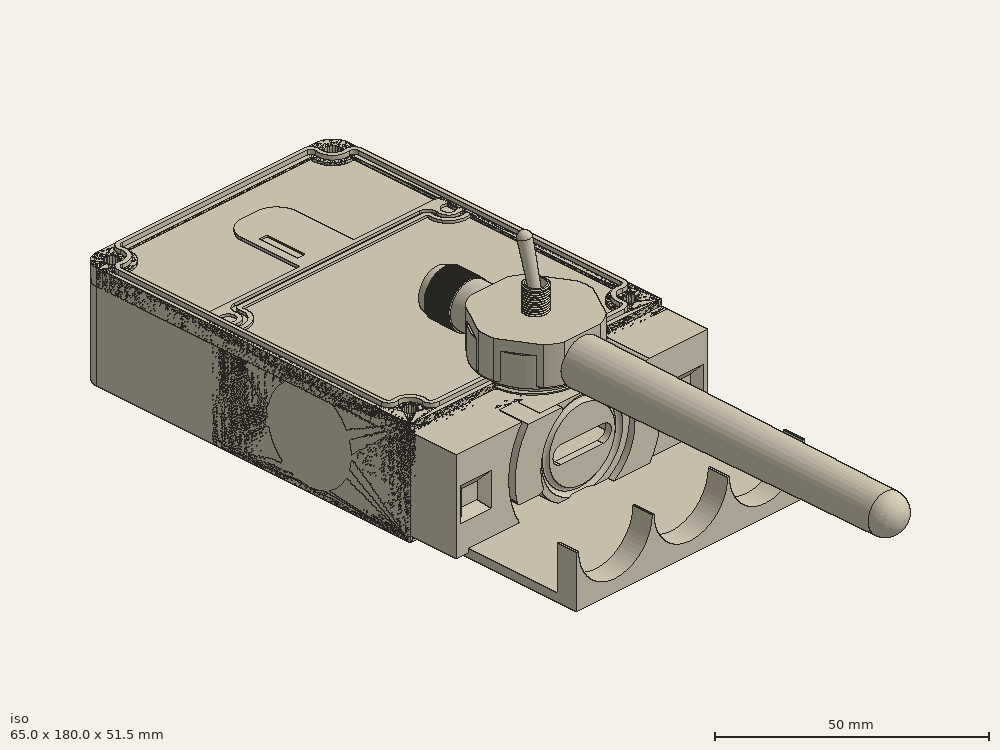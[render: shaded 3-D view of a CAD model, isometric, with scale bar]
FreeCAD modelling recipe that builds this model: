
FCSTD DOCUMENT  (FreeCAD 1.1R40006 (Git))
Label: NomadShell_0.1
License: All rights reserved
LicenseURL: https://en.wikipedia.org/wiki/All_rights_reserved
objects: Sketcher::SketchObject×62, App::FeaturePython×43, App::Point×31, Part::Feature×30, PartDesign::Pocket×26, PartDesign::Pad×24, App::Link×23, App::Part×15, PartDesign::Body×15, PartDesign::SubtractivePipe×6, PartDesign::Fillet×6, PartDesign::SubShapeBinder×5, PartDesign::Revolution×3, Part::FeaturePython×2, PartDesign::Boolean×2, PartDesign::Hole×2, App::DocumentObjectGroup×2, PartDesign::AdditivePipe×2, App::VarSet×1, PartDesign::Chamfer×1, +8 more types
note: 402 computed .brp shape members not serialized (recipe doc carries the construction recipe); baked Part::Feature solids carry a one-line shape summary decoded from their .brp

FEATURE [Part::Feature] Part__Feature064  label="18650 v1"
  Placement = pos=(-6,-63,0) rot=(0,0,1;3.14159rad)
  shape: bbox 19.48 x 65 x 19.48 mm, 40 faces (baked)
FEATURE [App::Point] Origin105
  Role = Origin
FEATURE [App::VarSet] VarSet
  Base_base_lenght = 55
  Base_battery_lenght = 85
  Base_case_thickness = 3
  Base_connecot_lug_multipl = 2
  Base_connector_bounting_box_height = 22
  Base_connector_clip = 8
  Base_connector_clip_height = 1.6
  Base_connector_external_lug = 19
  Base_connector_height_lug = 12
  Base_connector_internal_lug = 12
  Base_connector_lug_offset = 0.1
  Base_connector_lug_remaining_key = 6
  Base_connector_oring_cross_section = 2
  Base_connector_oring_offset = 0.2
  Base_connector_oring_outside_diameter = 21
  Base_gasket_height = 2
  Base_gasket_width = 1
  Base_gps_antenna_height = 5
  Base_gps_antenna_lenght = 15
  Base_gps_antenna_width = 15
  Base_lid_thickness = 5
  Base_m3_insert = 3.2
  Base_pogopin_cutout_height = 1.5
  Base_pogopin_outside = 21
  Base_pogoping_lenght = 15.1
  Base_pogopins_r = 2.1
  Base_usb_cover_main_diameter = 18
  base_width = 65
  case_height = 25
FEATURE [App::Point] Origin111
  Role = Origin
FEATURE [App::Point] Origin113
  Role = Origin
FEATURE [App::Link] base  label="base001"
  LinkedObject = -> Part
FEATURE [App::FeaturePython] GroundedJoint  # Assembly grounded joint (typed FeaturePython)
  ObjectToGround = -> base
FEATURE [Part::Feature] PCB_solid  label="RAK19003_carrier"
  shape: bbox 35.78 x 30 x 9.401 mm, 8397 faces (baked)
FEATURE [App::Link] RAK19003__Solid_  label="RAK19003 (Solid)001"
  LinkPlacement = pos=(-8.5,9,-15.9902) rot=(0,0,1;0rad)
  LinkedObject = -> PCB_solid
  Placement = pos=(-8.5,9,-15.9902) rot=(0,0,1;0rad)
FEATURE [App::Point] Origin115
  Role = Origin
FEATURE [App::Point] Origin117
  Role = Origin
FEATURE [Sketcher::SketchObject] Sketch006  label="battery_body001"
  ArcFitTolerance = 1e-06
  AttachmentSupport = -> [XY_Plane058]
  ExternalTypes = [0]
  FullyConstrained = true
  MakeInternals = false
  MapMode = 5
  expr: Constraints[13] = VarSet.base_width
  expr: Constraints[14] = VarSet.Base_battery_lenght
  expr: Constraints[30] = VarSet.Base_m3_insert
  expr: Constraints[44] = VarSet.Base_case_thickness
  expr: Constraints[47] = VarSet.Base_case_thickness + VarSet.Base_m3_insert / 2
  expr: Constraints[48] = VarSet.Base_case_thickness + VarSet.Base_m3_insert / 2
  expr: Constraints[67] = VarSet.Base_case_thickness / 2
  expr: Constraints[84] = VarSet.Base_case_thickness
  expr: Constraints[85] = VarSet.Base_case_thickness
  expr: Constraints[92] = VarSet.Base_case_thickness / 2
  sketch-geometry (40):
    g0: LineSegment StartX=-32.5 StartY=0 StartZ=0 EndX=32.5 EndY=0 EndZ=0
    g1: LineSegment StartX=32.5 StartY=0 StartZ=0 EndX=32.5 EndY=81 EndZ=0
    g2: LineSegment StartX=28.5 StartY=85 StartZ=0 EndX=-28.5 EndY=85 EndZ=0
    g3: LineSegment StartX=-32.5 StartY=81 StartZ=0 EndX=-32.5 EndY=0 EndZ=0
    g4: GeomPoint [constr] X=-32.5 Y=85 Z=0
    g5: ArcOfCircle CenterX=28.5 CenterY=81 CenterZ=0 NormalX=0 NormalY=0 NormalZ=1 AngleXU=0 Radius=4 StartAngle=1e-15 EndAngle=1.5708
    g6: GeomPoint [constr] X=32.5 Y=85 Z=0
    g7: Circle CenterX=-28.5 CenterY=4 CenterZ=0 NormalX=0 NormalY=0 NormalZ=1 AngleXU=0 Radius=1.6
    g8: Circle CenterX=28.5 CenterY=4 CenterZ=0 NormalX=0 NormalY=0 NormalZ=1 AngleXU=0 Radius=1.6
    g9: Circle CenterX=28.5 CenterY=81 CenterZ=0 NormalX=0 NormalY=0 NormalZ=1 AngleXU=0 Radius=1.6
    g10: Circle CenterX=-28.5 CenterY=81 CenterZ=0 NormalX=0 NormalY=0 NormalZ=1 AngleXU=0 Radius=1.6
    g11: LineSegment [constr] StartX=-28.5 StartY=81 StartZ=0 EndX=-28.5 EndY=4 EndZ=0
    g12: LineSegment [constr] StartX=-28.5 StartY=4 StartZ=0 EndX=28.5 EndY=4 EndZ=0
    g13: LineSegment [constr] StartX=28.5 StartY=4 StartZ=0 EndX=28.5 EndY=81 EndZ=0
    g14: LineSegment [constr] StartX=28.5 StartY=81 StartZ=0 EndX=-28.5 EndY=81 EndZ=0
    g15: LineSegment StartX=-24.01 StartY=82 StartZ=0 EndX=23.9076 EndY=82 EndZ=0
    g16: LineSegment StartX=29.5 StartY=76.4076 StartZ=0 EndX=29.5 EndY=8.48999 EndZ=0
    g17: LineSegment StartX=24.01 StartY=3 StartZ=0 EndX=-24.01 EndY=3 EndZ=0
    g18: LineSegment StartX=-29.5 StartY=8.48999 StartZ=0 EndX=-29.5 EndY=76.51 EndZ=0
    g19: ArcOfCircle CenterX=-28.5 CenterY=4 CenterZ=0 NormalX=0 NormalY=0 NormalZ=1 AngleXU=0 Radius=4.6 StartAngle=6.06404 EndAngle=8.07312
    g20: ArcOfCircle CenterX=-28.5 CenterY=81 CenterZ=0 NormalX=0 NormalY=0 NormalZ=1 AngleXU=0 Radius=4.6 StartAngle=4.49325 EndAngle=6.50233
    g21: ArcOfCircle CenterX=28.5 CenterY=81 CenterZ=0 NormalX=0 NormalY=0 NormalZ=1 AngleXU=0 Radius=4.7 StartAngle=2.92719 EndAngle=4.92679
    g22: ArcOfCircle CenterX=28.5 CenterY=4 CenterZ=0 NormalX=0 NormalY=0 NormalZ=1 AngleXU=0 Radius=4.6 StartAngle=1.35166 EndAngle=3.36073
    g23: ArcOfCircle CenterX=28.5 CenterY=4 CenterZ=0 NormalX=0 NormalY=0 NormalZ=1 AngleXU=0 Radius=3.1 StartAngle=1.35166 EndAngle=3.36073
    g24: ArcOfCircle CenterX=24.01 CenterY=3 CenterZ=0 NormalX=0 NormalY=0 NormalZ=1 AngleXU=-3.14159 Radius=1.5 StartAngle=1.5708 EndAngle=3.36073
    g25: LineSegment StartX=24.01 StartY=1.5 StartZ=0 EndX=-24.01 EndY=1.5 EndZ=0
    g26: ArcOfCircle CenterX=-24.01 CenterY=3 CenterZ=0 NormalX=0 NormalY=0 NormalZ=1 AngleXU=1.55119 Radius=1.5 StartAngle=1.37126 EndAngle=3.1612
    g27: ArcOfCircle CenterX=-28.5 CenterY=4 CenterZ=0 NormalX=0 NormalY=0 NormalZ=1 AngleXU=0 Radius=3.1 StartAngle=6.06404 EndAngle=8.07312
    g28: ArcOfCircle CenterX=-29.5 CenterY=8.48999 CenterZ=0 NormalX=0 NormalY=0 NormalZ=1 AngleXU=1.5708 Radius=1.5 StartAngle=1.5708 EndAngle=3.36073
    g29: LineSegment StartX=-31 StartY=8.48999 StartZ=0 EndX=-31 EndY=76.51 EndZ=0
    g30: ArcOfCircle CenterX=-29.5 CenterY=76.51 CenterZ=0 NormalX=0 NormalY=0 NormalZ=1 AngleXU=-0.0196091 Radius=1.5 StartAngle=1.37126 EndAngle=3.1612
    g31: ArcOfCircle CenterX=-28.5 CenterY=81 CenterZ=0 NormalX=0 NormalY=0 NormalZ=1 AngleXU=0 Radius=3.1 StartAngle=4.49325 EndAngle=6.50233
    g32: ArcOfCircle CenterX=-24.01 CenterY=82 CenterZ=0 NormalX=0 NormalY=0 NormalZ=1 AngleXU=0 Radius=1.5 StartAngle=1.5708 EndAngle=3.36073
    g33: LineSegment StartX=-24.01 StartY=83.5 StartZ=0 EndX=23.9076 EndY=83.5 EndZ=0
    g34: ArcOfCircle CenterX=23.9076 CenterY=82 CenterZ=0 NormalX=0 NormalY=0 NormalZ=1 AngleXU=-1.5708 Radius=1.5 StartAngle=1.35639 EndAngle=3.14159
    g35: ArcOfCircle CenterX=28.5 CenterY=81 CenterZ=0 NormalX=0 NormalY=0 NormalZ=1 AngleXU=0 Radius=3.2 StartAngle=2.92719 EndAngle=4.92679
    g36: ArcOfCircle CenterX=29.5 CenterY=76.4076 CenterZ=0 NormalX=0 NormalY=0 NormalZ=1 AngleXU=-1.5708 Radius=1.5 StartAngle=1.5708 EndAngle=3.356
    g37: LineSegment StartX=31 StartY=76.4076 StartZ=0 EndX=31 EndY=8.48999 EndZ=0
    g38: ArcOfCircle CenterX=29.5 CenterY=8.48999 CenterZ=0 NormalX=0 NormalY=0 NormalZ=1 AngleXU=3.12198 Radius=1.5 StartAngle=1.37126 EndAngle=3.1612
    g39: ArcOfCircle CenterX=-28.5 CenterY=81 CenterZ=0 NormalX=0 NormalY=0 NormalZ=1 AngleXU=0 Radius=4 StartAngle=1.5708 EndAngle=3.14159
  constraints (94):
    c: Coincident(g0,g1)
    c: Coincident(g3,g0)
    c: Horizontal(g2)
    c: Vertical(g1)
    c: Vertical(g3)
    c: PointOnObject(g0,g-1)
    c: Symmetric(g0,g0,g-2)
    c: PointOnObject(g4,g3)
    c: PointOnObject(g4,g2)
    c: PointOnObject(g6,g1)
    c: PointOnObject(g6,g2)
    c: Tangent(g1,g5) = -1.5708
    c: Tangent(g2,g5) = -1.5708
    c: DistanceX(g4,g6) = 65
    c: DistanceY(g0,g4) = 85
    c: Coincident(g11,g12)
    c: Coincident(g12,g13)
    c: Coincident(g13,g14)
    c: Coincident(g14,g11)
    c: Vertical(g11)
    c: Vertical(g13)
    c: Horizontal(g12)
    c: Coincident(g11,g10)
    c: Coincident(g12,g8)
    c: Coincident(g7,g11)
    c: Coincident(g13,g9)
    c: Symmetric(g10,g9,g-2)
    c: Equal(g10,g9)
    c: Equal(g9,g8)
    c: Equal(g8,g7)
    c: Diameter(g10) = 3.2
    c: Distance(g7,g0) = 2.4
    c: Horizontal(g15)
    c: Vertical(g16)
    c: Horizontal(g17)
    c: Vertical(g18)
    c: Coincident(g19,g18)
    c: Coincident(g19,g17)
    c: Coincident(g20,g18)
    c: Coincident(g20,g15)
    c: Coincident(g21,g15)
    c: Coincident(g21,g16)
    c: Coincident(g22,g16)
    c: Coincident(g22,g17)
    c: Distance(g17,g0) = 3
    c: Coincident(g22,g8)
    c: Coincident(g19,g7)
    c: Radius(g19) = 4.6
    c: Radius(g20) = 4.6
    c: Coincident(g10,g20)
    c: Coincident(g21,g5)
    c: Tangent(g23,g24) = 1.5708
    c: Tangent(g23,g38) = 1.5708
    c: Tangent(g24,g25) = 1.5708
    c: Tangent(g25,g26) = 1.5708
    c: Tangent(g26,g27) = 1.5708
    c: Tangent(g27,g28) = 1.5708
    c: Tangent(g28,g29) = 1.5708
    c: Tangent(g29,g30) = 1.5708
    c: Tangent(g30,g31) = 1.5708
    c: Tangent(g31,g32) = 1.5708
    c: Tangent(g32,g33) = 1.5708
    c: Tangent(g33,g34) = 1.5708
    c: Tangent(g34,g35) = 1.5708
    c: Tangent(g35,g36) = 1.5708
    c: Tangent(g36,g37) = 1.5708
    c: Tangent(g37,g38) = 1.5708
    c: Distance(g17,g25) = 1.5
    c: Coincident(g32,g15)
    c: Coincident(g30,g18)
    c: Coincident(g36,g16)
    c: Coincident(g24,g17)
    c: Coincident(g26,g17)
    c: Coincident(g28,g18)
    c: Coincident(g27,g7)
    c: Coincident(g23,g8)
    c: Coincident(g9,g35)
    c: Coincident(g34,g15)
    c: Coincident(g38,g16)
    c: Coincident(g39,g10)
    c: Coincident(g39,g2)
    c: Coincident(g39,g3)
    c: Coincident(g31,g10)
    c: Coincident(g5,g9)
    c: Distance(g1,g16) = 3
    c: Distance(g18,g3) = 3
    c: Parallel(g25,g-1)
    c: Parallel(g29,g-2)
    c: Parallel(g33,g-1)
    c: Equal(g27,g23)
    c: Distance(g10,g2) = 2.4
    c: Radius(g39) = 4
    c: Distance(g33,g2) = 1.5
    c: Radius(g35) = 3.2
FEATURE [PartDesign::Pad] Pad004
  Direction = (0,0,1)
  Length = 25
  Length2 = 10
  Profile = -> Sketch006 [Edge1,Edge6,Edge5,Edge4,Edge3,Edge2]
  ReferenceAxis = -> Sketch006 [N_Axis]
  Refine = true
  Reversed = true
  Suppressed = false
  Type = 0
  expr: Length = VarSet.case_height
FEATURE [PartDesign::Pocket] Pocket005  label="pocket"
  BaseFeature = -> Pad004
  Direction = (0,0,-1)
  Length = 22
  Length2 = 5
  Profile = -> Sketch006 [Edge15,Edge16,Edge17,Edge18,Edge11,Edge12,Edge13,Edge14]
  ReferenceAxis = -> Sketch006 [N_Axis]
  Refine = true
  Suppressed = false
  Type = 0
  expr: Length = VarSet.case_height - VarSet.Base_case_thickness
FEATURE [PartDesign::Pocket] Pocket006  label="screw001"
  BaseFeature = -> Pocket005
  Direction = (0,0,-1)
  Length = 5
  Length2 = 5
  Midplane = true
  Profile = -> Sketch006 [Edge10,Edge9,Edge8,Edge7]
  ReferenceAxis = -> Sketch006 [N_Axis]
  Refine = true
  Suppressed = false
  Type = 1
FEATURE [App::Link] battery  label="battery001"
  LinkPlacement = pos=(0.216708,-33.5,0.15511) rot=(0,0,1;3.14159rad)
  LinkedObject = -> Part002
  Placement = pos=(0.216708,-33.5,0.15511) rot=(0,0,1;3.14159rad)
FEATURE [Sketcher::SketchObject] Sketch007  label="18650_battery_holder"
  ArcFitTolerance = 1e-06
  AttachmentOffset = pos=(0,0,-21) rot=(0,0,1;0rad)
  AttachmentSupport = -> [XZ_Plane058]
  ExternalGeometry = -> [Pocket006]
  ExternalTypes = [0,0,0]
  FullyConstrained = true
  MakeInternals = false
  MapMode = 5
  Placement = pos=(0,21,-4.7e-15) rot=(1,0,0;1.5708rad)
  expr: .AttachmentOffset.Base.z = -7 * VarSet.Base_case_thickness
  sketch-geometry (12):
    g0: ArcOfCircle CenterX=-19.4 CenterY=-12 CenterZ=0 NormalX=0 NormalY=0 NormalZ=1 AngleXU=0 Radius=9.5 StartAngle=3.14159 EndAngle=6.28319
    g1: LineSegment StartX=-28.9 StartY=-12 StartZ=0 EndX=-29.4 EndY=-12 EndZ=0
    g2: LineSegment StartX=-29.4 StartY=-12 StartZ=0 EndX=-29.4 EndY=-22 EndZ=0
    g3: LineSegment StartX=-29.4 StartY=-22 StartZ=0 EndX=29.5 EndY=-22 EndZ=0
    g4: LineSegment StartX=-9.4 StartY=-12 StartZ=0 EndX=-9.9 EndY=-12 EndZ=0
    g5: LineSegment [constr] StartX=-29.4 StartY=-12 StartZ=0 EndX=29.5 EndY=-12 EndZ=0
    g6: LineSegment [constr] StartX=29.5 StartY=0 StartZ=0 EndX=29.5 EndY=-12 EndZ=0
    g7: ArcOfCircle CenterX=0.1 CenterY=-12 CenterZ=0 NormalX=0 NormalY=0 NormalZ=1 AngleXU=0 Radius=9.5 StartAngle=3.14159 EndAngle=6.28319
    g8: LineSegment StartX=9.6 StartY=-12 StartZ=0 EndX=10.1 EndY=-12 EndZ=0
    g9: ArcOfCircle CenterX=19.6 CenterY=-12 CenterZ=0 NormalX=0 NormalY=0 NormalZ=1 AngleXU=0 Radius=9.5 StartAngle=3.14159 EndAngle=6.28319
    g10: LineSegment StartX=29.1 StartY=-12 StartZ=0 EndX=29.5 EndY=-12 EndZ=0
    g11: LineSegment StartX=29.5 StartY=-22 StartZ=0 EndX=29.5 EndY=-12 EndZ=0
  constraints (37):
    c: Coincident(g1,g2)
    c: Vertical(g2)
    c: Coincident(g2,g3)
    c: Horizontal(g3)
    c: Coincident(g0,g1)
    c: Radius(g0) = 9.5
    c: DistanceY(g2,g1) = 10
    c: PointOnObject(g3,g-3)
    c: DistanceX(g1,g0) = 0.5
    c: DistanceX(g-5,g1) = 0.1
    c: Coincident(g4,g0)
    c: Horizontal(g4)
    c: Coincident(g5,g1)
    c: Horizontal(g5)
    c: Coincident(g6,g-4)
    c: Coincident(g6,g5)
    c: Vertical(g6)
    c: PointOnObject(g7,g5)
    c: Coincident(g7,g4)
    c: PointOnObject(g7,g5)
    c: Coincident(g7,g8)
    c: PointOnObject(g8,g5)
    c: PointOnObject(g0,g5)
    c: PointOnObject(g0,g5)
    c: PointOnObject(g0,g5)
    c: PointOnObject(g9,g5)
    c: Coincident(g9,g8)
    c: PointOnObject(g9,g5)
    c: Coincident(g10,g9)
    c: Coincident(g11,g3)
    c: Coincident(g11,g10)
    c: Perpendicular(g11,g3)
    c: Equal(g1,g4)
    c: Equal(g4,g8)
    c: Equal(g0,g7)
    c: Equal(g7,g9)
    c: Coincident(g10,g5)
FEATURE [PartDesign::Pad] Pad005  label="18650_battery_holder001"
  BaseFeature = -> Pocket006
  Direction = (0,-1,2e-16)
  Length = 5
  Length2 = 10
  Midplane = true
  Profile = -> Sketch007
  ReferenceAxis = -> Sketch007 [N_Axis]
  Refine = true
  Suppressed = false
  Type = 0
FEATURE [App::Link] _8650_v1  label="18650 v002"
  LinkPlacement = pos=(0.116708,-107.966,-11.8449) rot=(0,-1,0;1.5708rad)
  LinkedObject = -> Part__Feature064
  Placement = pos=(0.116708,-107.966,-11.8449) rot=(0,-1,0;1.5708rad)
FEATURE [Part::Feature] Part__Feature066  label="ant"
  Placement = pos=(3.7e-15,4.99733,5.00169) rot=(1,0,0;1.5708rad)
  shape: bbox 11.02 x 100 x 11.02 mm, 30 faces, 3 solids (baked)
FEATURE [Part::Feature] Part__Feature067  label="conn_body"
  Placement = pos=(-0.0138346,-0.00267039,0.00168873) rot=(0,0,1;0rad)
  shape: bbox 11.61 x 29.27 x 11.28 mm, 560 faces (baked)
FEATURE [Part::Feature] Part__Feature068  label="SMA_threads"
  Placement = pos=(-0.0138346,-0.00267039,0.00168873) rot=(0,0,1;0rad)
  shape: bbox 8 x 3 x 8 mm, 4 faces (baked)
FEATURE [Part::Feature] Part__Feature069  label="socket"
  Placement = pos=(-0.0138346,-0.28267,0.00168873) rot=(0,0,1;0rad)
  shape: bbox 1.27 x 5.64 x 1.27 mm, 5 faces (baked)
FEATURE [App::Part] antenna_WiFi_RP_SMA_conn_v2  label="antenna_WiFi_RP-SMA_conn v2"
  Group = -> [Part__Feature066,Part__Feature067,Part__Feature068,Part__Feature069]
  Origin = -> Origin118
FEATURE [App::Point] Origin119
  Role = Origin
FEATURE [Part::Feature] Part__Feature070  label="sma"
  Placement = pos=(0,0,-13) rot=(0,0,1;0rad)
  shape: bbox 10.21 x 10.21 x 16.97 mm, 172 faces (baked)
FEATURE [Part::Feature] Part__Feature071  label="70205K69_Cover for 0.5 Deep x 0.12 Diameter Toggle Switch"
  shape: bbox 8.382 x 1.91 x 8.382 mm, 13 faces (baked)
FEATURE [Part::Feature] Part__Feature072  label="70205K69_Cover for 0.5 Deep x 0.12 Diameter Toggle Switch001"
  shape: bbox 10.37 x 17.02 x 11.04 mm, 82 faces (baked)
FEATURE [App::Part] _0205K69_Cover_for_0_5_Deep_x_0_12_Diameter_Toggle_Switch  label="switch_cover"
  Group = -> [Part__Feature071,Part__Feature072]
  Origin = -> Origin120
  Placement = pos=(0,0,34) rot=(1,0,0;3.14159rad)
FEATURE [App::Point] Origin121
  Role = Origin
FEATURE [Part::Feature] Part__Feature073  label="Plastic_corpuse"
  shape: bbox 7.85 x 12.96 x 9.7 mm, 55 faces (baked)
FEATURE [Part::Feature] Part__Feature074  label="Contacts"
  shape: bbox 3.88 x 0.8 x 4.2 mm, 14 faces (baked)
FEATURE [Part::Feature] Part__Feature075  label="Contacts001"
  Placement = pos=(0,-4.43,0) rot=(0,0,1;0rad)
  shape: bbox 3.88 x 0.8 x 4.2 mm, 14 faces (baked)
FEATURE [Part::Feature] Part__Feature076  label="Metal_scoba"
  shape: bbox 7.9 x 13 x 6 mm, 255 faces (baked)
FEATURE [Part::Feature] Part__Feature077  label="Rezba"
  Placement = pos=(0.0336891,-0.0345067,0.0256431) rot=(0,0,1;0rad)
  shape: bbox 6.314 x 6.357 x 7.676 mm, 70 faces (baked)
FEATURE [Part::Feature] Part__Feature078  label="Tumbler"
  Placement = pos=(0,-3.72699,0.490668) rot=(-1,0,0;0.261799rad)
  shape: bbox 3 x 5.772 x 13.55 mm, 3 faces (baked)
FEATURE [App::Part] TSM102A1_v5  label="on_off_switch"
  Group = -> [Part__Feature073,Part__Feature074,Part__Feature075,Part__Feature076,Part__Feature077,Part__Feature078]
  Origin = -> Origin122
  Placement = pos=(0,0,43) rot=(1,0,0;1.5708rad)
FEATURE [App::Point] Origin123
  Role = Origin
FEATURE [App::Point] Origin125
  Role = Origin
FEATURE [App::Point] Origin127
  Role = Origin
FEATURE [Sketcher::SketchObject] Sketch008  label="main_usb_cover"
  ArcFitTolerance = 1e-06
  AttachmentSupport = -> [XZ_Plane063]
  ExternalTypes = [0]
  FullyConstrained = true
  MakeInternals = false
  MapMode = 5
  Placement = pos=(0,0,0) rot=(1,0,0;1.5708rad)
  expr: Constraints[12] = VarSet.Base_case_thickness / 2
  expr: Constraints[14] = VarSet.Base_usb_cover_main_diameter * 1.2 / 2
  expr: Constraints[15] = VarSet.Base_usb_cover_main_diameter / 2
  sketch-geometry (6):
    g0: LineSegment StartX=-9 StartY=0 StartZ=0 EndX=-10.8 EndY=0 EndZ=0
    g1: LineSegment StartX=-10.8 StartY=0 StartZ=0 EndX=-10.8 EndY=1.5 EndZ=0
    g2: LineSegment StartX=-10.8 StartY=1.5 StartZ=0 EndX=-10.4 EndY=1.5 EndZ=0
    g3: LineSegment StartX=-10.4 StartY=1.5 StartZ=0 EndX=-10.4 EndY=7.5 EndZ=0
    g4: LineSegment StartX=-10.4 StartY=7.5 StartZ=0 EndX=-9 EndY=7.5 EndZ=0
    g5: LineSegment StartX=-9 StartY=7.5 StartZ=0 EndX=-9 EndY=0 EndZ=0
  constraints (18):
    c: PointOnObject(g0,g-1)
    c: PointOnObject(g0,g-1)
    c: Coincident(g0,g1)
    c: Coincident(g1,g2)
    c: Horizontal(g2)
    c: Coincident(g2,g3)
    c: Coincident(g3,g4)
    c: Coincident(g4,g5)
    c: Coincident(g5,g0)
    c: Parallel(g5,g-2)
    c: Parallel(g4,g-1)
    c: Parallel(g1,g-2)
    c: DistanceY(g0,g1) = 1.5
    c: Parallel(g3,g5)
    c: DistanceX(g0,g-1) = 10.8
    c: DistanceX(g0,g-1) = 9
    c: DistanceY(g2,g3) = 6
    c: Distance(g4,g4) = 1.4
FEATURE [PartDesign::Revolution] Revolution
  Angle = 360
  Angle2 = 60
  Axis = (0,2e-16,1)
  Base = (0,0,0)
  Placement = pos=(0,0,0) rot=(1,0,0;1.5708rad)
  Profile = -> Sketch008
  ReferenceAxis = -> Sketch008 [V_Axis]
  Refine = true
  Suppressed = false
  Type = 0
FEATURE [App::Link] usb_cover_base  label="usb_cover_base001"
  LinkPlacement = pos=(-31,26,-13) rot=(0.57735,-0.57735,-0.57735;2.0944rad)
  LinkedObject = -> Part003
  Placement = pos=(-31,26,-13) rot=(0.57735,-0.57735,-0.57735;2.0944rad)
FEATURE [App::Link] on_off_switch  label="on_off_switch002"
  LinkPlacement = pos=(1.00889,42.9,-9.4) rot=(-0.57735,0.57735,0.57735;2.0944rad)
  LinkedObject = -> TSM102A1_v5
  Placement = pos=(1.00889,42.9,-9.4) rot=(-0.57735,0.57735,0.57735;2.0944rad)
FEATURE [App::Link] switch_cover  label="switch_cover001"
  LinkPlacement = pos=(1.00889,63.509,-9.4) rot=(0,1,0;1.5708rad)
  LinkedObject = -> _0205K69_Cover_for_0_5_Deep_x_0_12_Diameter_Toggle_Switch
  Placement = pos=(1.00889,63.509,-9.4) rot=(0,1,0;1.5708rad)
FEATURE [App::Link] antenna_WiFi_RP_SMA_conn_v003  label="antenna_WiFi_RP-SMA_conn v003"
  LinkPlacement = pos=(17.0138,86.4273,-10.9983) rot=(1,0,0;3.14159rad)
  LinkedObject = -> antenna_WiFi_RP_SMA_conn_v2
  Placement = pos=(17.0138,86.4273,-10.9983) rot=(1,0,0;3.14159rad)
FEATURE [Part::Feature] PCB_solid001  label="RAK4631 (Solid)"
  shape: bbox 20 x 30 x 4.403 mm, 2955 faces (baked)
FEATURE [App::Link] RAK4631__Solid_  label="RAK4631 (Solid)001"
  LinkPlacement = pos=(29.458,29.4471,-14.4384) rot=(-0.447342,0,0.894685;0rad)
  LinkedObject = -> PCB_solid001
  Placement = pos=(29.458,29.4471,-14.4384) rot=(-0.447342,0,0.894685;0rad)
FEATURE [Part::FeaturePython] ScrewDie  label="21x7-ScrewDie"  # WARN: FeaturePython — macro-defined, semantics opaque (R4)
  Diameter = 29
  DiameterCustom = 21
  Invert = false
  LeftHanded = false
  Length = 7
  MatchOuter = false
  OffsetAngle = 0
  PitchCustom = 2
  Placement = pos=(0,0,8.5) rot=(0,0,1;0rad)
  Thread = true
  Type = 0
FEATURE [App::Point] Origin128
  Role = Origin
FEATURE [App::Point] Origin130
  Role = Origin
FEATURE [Sketcher::SketchObject] Sketch009  label="main_screw"
  ArcFitTolerance = 1e-06
  AttachmentSupport = -> [XZ_Plane064]
  ExternalTypes = [0]
  FullyConstrained = true
  MakeInternals = false
  MapMode = 5
  Placement = pos=(0,0,0) rot=(1,0,0;1.5708rad)
  expr: Constraints[15] = VarSet.Base_usb_cover_main_diameter / 2
  sketch-geometry (6):
    g0: LineSegment StartX=0 StartY=9 StartZ=0 EndX=0 EndY=11 EndZ=0
    g1: LineSegment StartX=0 StartY=11 StartZ=0 EndX=-13 EndY=11 EndZ=0
    g2: LineSegment StartX=-13 StartY=11 StartZ=0 EndX=-13 EndY=2 EndZ=0
    g3: LineSegment StartX=-13 StartY=2 StartZ=0 EndX=-9 EndY=2 EndZ=0
    g4: LineSegment StartX=-9 StartY=2 StartZ=0 EndX=-9 EndY=9 EndZ=0
    g5: LineSegment StartX=-9 StartY=9 StartZ=0 EndX=0 EndY=9 EndZ=0
  constraints (18):
    c: PointOnObject(g0,g-2)
    c: PointOnObject(g0,g-2)
    c: Coincident(g0,g1)
    c: Horizontal(g1)
    c: Coincident(g1,g2)
    c: Vertical(g2)
    c: Coincident(g2,g3)
    c: Horizontal(g3)
    c: Coincident(g3,g4)
    c: Vertical(g4)
    c: Coincident(g4,g5)
    c: Coincident(g5,g0)
    c: Horizontal(g5)
    c: Distance(g0,g0) = 2
    c: DistanceX(g1,g4) = 4
    c: DistanceX(g4,g0) = 9
    c: DistanceY(g2,g2) = 9
    c: DistanceY(g-1,g0) = 9
FEATURE [PartDesign::Revolution] Revolution001
  Angle = 360
  Angle2 = 60
  Axis = (0,2e-16,1)
  Base = (0,0,0)
  Placement = pos=(0,0,0) rot=(1,0,0;1.5708rad)
  Profile = -> Sketch009
  ReferenceAxis = -> Sketch009 [V_Axis]
  Refine = true
  Suppressed = false
  Type = 0
FEATURE [Sketcher::SketchObject] Sketch010  label="cutout"
  ArcFitTolerance = 1e-06
  AttachmentSupport = -> [XY_Plane064]
  ExternalGeometry = -> [Revolution001]
  ExternalTypes = [0]
  FullyConstrained = true
  MakeInternals = false
  MapMode = 5
  sketch-geometry (7):
    g0: LineSegment StartX=14 StartY=0 StartZ=0 EndX=7 EndY=12.1244 EndZ=0
    g1: LineSegment StartX=7 StartY=12.1244 StartZ=0 EndX=-7 EndY=12.1244 EndZ=0
    g2: LineSegment StartX=-7 StartY=12.1244 StartZ=0 EndX=-14 EndY=-2.1849e-12 EndZ=0
    g3: LineSegment StartX=-14 StartY=-2.1849e-12 StartZ=0 EndX=-7 EndY=-12.1244 EndZ=0
    g4: LineSegment StartX=-7 StartY=-12.1244 StartZ=0 EndX=7 EndY=-12.1244 EndZ=0
    g5: LineSegment StartX=7 StartY=-12.1244 StartZ=0 EndX=14 EndY=0 EndZ=0
    g6: Circle [constr] CenterX=0 CenterY=0 CenterZ=0 NormalX=0 NormalY=0 NormalZ=1 AngleXU=0 Radius=14
  constraints (16):
    c: Coincident(g0,g1)
    c: Coincident(g1,g2)
    c: Coincident(g2,g3)
    c: Coincident(g3,g4)
    c: Coincident(g4,g5)
    c: Coincident(g5,g0)
    c: Equal(g0, g1-g5) x5
    c: PointOnObject(g0,g6)
    c: PointOnObject(g1,g6)
    c: PointOnObject(g2,g6)
    c: PointOnObject(g3,g6)
    c: PointOnObject(g4,g6)
    c: PointOnObject(g5,g6)
    c: Coincident(g6,g-1)
    c: PointOnObject(g5,g-1)
    c: Diameter(g6) = 28
FEATURE [PartDesign::Pocket] Pocket011
  BaseFeature = -> Revolution001
  Direction = (0,0,-1)
  Length = 5
  Length2 = 5
  Placement = pos=(0,0,0) rot=(1,0,0;1.5708rad)
  Profile = -> Sketch010
  ReferenceAxis = -> Sketch010 [N_Axis]
  Refine = true
  Reversed = true
  Suppressed = false
  Type = 1
FEATURE [Part::FeaturePython] ScrewTap  label="21.4x10-ScrewTap"  # WARN: FeaturePython — macro-defined, semantics opaque (R4)
  Diameter = 29
  DiameterCustom = 21.4
  Invert = false
  LeftHanded = false
  Length = 10
  MatchOuter = false
  OffsetAngle = 0
  PitchCustom = 2
  Placement = pos=(0,0,9) rot=(0,0,1;0rad)
  Thread = true
  Type = 2
FEATURE [PartDesign::Boolean] Boolean001
  BaseFeature = -> Pocket011
  Group = -> [ScrewTap]
  Refine = true
  Suppressed = false
  Type = 1
  UsePlacement = true
FEATURE [PartDesign::Body] Body004  label="usb_screw002"
  AllowCompound = false
  Group = -> [Sketch009,Revolution001,Sketch010,Pocket011,Boolean001]
  Origin = -> Origin129
  Tip = -> Boolean001
FEATURE [App::Part] Part004  label="usb_screw"
  Group = -> [Body004]
  Origin = -> Origin
  Placement = pos=(0,0,21) rot=(0,0,1;0rad)
FEATURE [PartDesign::Boolean] Boolean
  BaseFeature = -> Revolution
  Group = -> [ScrewDie]
  Refine = true
  Suppressed = false
  Type = 1
  UsePlacement = true
FEATURE [PartDesign::Body] Body003  label="usb_cover_base002"
  AllowCompound = false
  Group = -> [Sketch008,Revolution,Boolean]
  Origin = -> Origin126
  Tip = -> Boolean
FEATURE [App::Part] Part003  label="usb_cover_base"
  Group = -> [Body003]
  Origin = -> Origin124
FEATURE [App::Link] usb_screw  label="usb_screw001"
  LinkPlacement = pos=(-30.75,26.5888,-13) rot=(0.57735,0.57735,-0.57735;4.18879rad)
  LinkedObject = -> Part004
  Placement = pos=(-30.75,26.5888,-13) rot=(0.57735,0.57735,-0.57735;4.18879rad)
FEATURE [App::Point] Origin132
  Role = Origin
FEATURE [Sketcher::SketchObject] Sketch011  label="main_lunges"
  ArcFitTolerance = 1e-06
  AttachmentSupport = -> [XZ_Plane065]
  ExternalTypes = [0]
  FullyConstrained = true
  MakeInternals = false
  MapMode = 5
  Placement = pos=(0,0,0) rot=(1,0,0;1.5708rad)
  expr: Constraints[10] = VarSet.case_height
  expr: Constraints[12] = VarSet.case_height / 2
  expr: Constraints[17] = VarSet.Base_connector_bounting_box_height
  expr: Constraints[36] = VarSet.Base_connector_lug_remaining_key
  expr: Constraints[37] = VarSet.Base_connector_lug_remaining_key
  expr: Constraints[40] = VarSet.Base_connector_external_lug - VarSet.Base_connector_lug_offset
  expr: Constraints[42] = VarSet.Base_connector_internal_lug + VarSet.Base_connector_lug_offset
  expr: Constraints[46] = VarSet.Base_connector_internal_lug + VarSet.Base_connecot_lug_multipl * VarSet.Base_connector_lug_offset
  expr: Constraints[47] = VarSet.Base_connector_external_lug - VarSet.Base_connecot_lug_multipl * VarSet.Base_connector_lug_offset
  expr: Constraints[9] = VarSet.base_width
  sketch-geometry (24):
    g0: LineSegment [constr] StartX=-32.5 StartY=0 StartZ=0 EndX=-32.5 EndY=-25 EndZ=0
    g1: LineSegment [constr] StartX=-32.5 StartY=-25 StartZ=0 EndX=32.5 EndY=-25 EndZ=0
    g2: LineSegment [constr] StartX=32.5 StartY=-25 StartZ=0 EndX=32.5 EndY=0 EndZ=0
    g3: LineSegment [constr] StartX=32.5 StartY=0 StartZ=0 EndX=-32.5 EndY=0 EndZ=0
    g4: GeomPoint X=0 Y=-12.5 Z=0
    g5: LineSegment [constr] StartX=-32.5 StartY=-1.5 StartZ=0 EndX=32.5 EndY=-1.5 EndZ=0
    g6: LineSegment [constr] StartX=-32.5 StartY=-23.5 StartZ=0 EndX=32.5 EndY=-23.5 EndZ=0
    g7: LineSegment [constr] StartX=-32.5 StartY=-1.5 StartZ=0 EndX=32.5 EndY=-23.5 EndZ=0
    g8: LineSegment StartX=5.04083 StartY=-23.5 StartZ=0 EndX=15.3691 EndY=-23.5 EndZ=0
    g9: LineSegment StartX=11.1283 StartY=-7.5 StartZ=0 EndX=18.1229 EndY=-7.5 EndZ=0
    g10: LineSegment StartX=-15.3691 StartY=-1.5 StartZ=0 EndX=-5.04083 EndY=-1.5 EndZ=0
    g11: LineSegment StartX=-18.1229 StartY=-17.5 StartZ=0 EndX=-11.1283 EndY=-17.5 EndZ=0
    g12: LineSegment StartX=-32.5 StartY=-1.5 StartZ=0 EndX=-32.5 EndY=-23.5 EndZ=0
    g13: LineSegment StartX=-32.5 StartY=-23.5 StartZ=0 EndX=32.5 EndY=-23.5 EndZ=0
    g14: LineSegment StartX=32.5 StartY=-23.5 StartZ=0 EndX=32.5 EndY=-1.5 EndZ=0
    g15: LineSegment StartX=32.5 StartY=-1.5 StartZ=0 EndX=-32.5 EndY=-1.5 EndZ=0
    g16: Circle [constr] CenterX=0 CenterY=-12.5 CenterZ=0 NormalX=0 NormalY=0 NormalZ=1 AngleXU=0 Radius=18.9
    g17: Circle [constr] CenterX=0 CenterY=-12.5 CenterZ=0 NormalX=0 NormalY=0 NormalZ=1 AngleXU=0 Radius=12.1
    g18: Circle [constr] CenterX=0 CenterY=-12.5 CenterZ=0 NormalX=0 NormalY=0 NormalZ=1 AngleXU=0 Radius=12.2
    g19: Circle [constr] CenterX=0 CenterY=-12.5 CenterZ=0 NormalX=0 NormalY=0 NormalZ=1 AngleXU=0 Radius=18.8
    g20: ArcOfCircle CenterX=0.262977 CenterY=-12.4274 CenterZ=0 NormalX=0 NormalY=0 NormalZ=1 AngleXU=0 Radius=19.0728 StartAngle=2.53151 EndAngle=3.41079
    g21: ArcOfCircle CenterX=0.216708 CenterY=-12.6551 CenterZ=0 NormalX=0 NormalY=0 NormalZ=1 AngleXU=0 Radius=18.6335 StartAngle=5.66199 EndAngle=6.5635
    g22: ArcOfCircle CenterX=0 CenterY=-12.5759 CenterZ=0 NormalX=0 NormalY=0 NormalZ=1 AngleXU=0 Radius=12.1691 StartAngle=1.9979 EndAngle=3.55817
    g23: ArcOfCircle CenterX=0 CenterY=-12.4241 CenterZ=0 NormalX=0 NormalY=0 NormalZ=1 AngleXU=0 Radius=12.1691 StartAngle=5.13949 EndAngle=6.69977
  constraints (68):
    c: Coincident(g0,g1)
    c: Coincident(g1,g2)
    c: Coincident(g2,g3)
    c: Coincident(g3,g0)
    c: Vertical(g0)
    c: Vertical(g2)
    c: Horizontal(g1)
    c: PointOnObject(g0,g-1)
    c: Symmetric(g0,g2,g-2)
    c: DistanceX(g0,g2) = 65
    c: DistanceY(g0,g-1) = 25
    c: PointOnObject(g4,g-2)
    c: DistanceY(g4,g-1) = 12.5
    c: PointOnObject(g6,g0)
    c: Horizontal(g6)
    c: PointOnObject(g6,g2)
    c: PointOnObject(g5,g2)
    c: DistanceY(g6,g5) = 22
    c: PointOnObject(g5,g0)
    c: Parallel(g5,g3)
    c: Coincident(g7,g5)
    c: Coincident(g7,g6)
    c: PointOnObject(g4,g7)
    c: Parallel(g9,g3)
    c: Parallel(g11,g5)
    c: Coincident(g12,g13)
    c: Coincident(g13,g14)
    c: Coincident(g14,g15)
    c: Coincident(g15,g12)
    c: Vertical(g12)
    c: Horizontal(g13)
    c: Symmetric(g12,g14,g-2)
    c: Parallel(g10,g3)
    c: Parallel(g8,g6)
    c: Coincident(g12,g5)
    c: PointOnObject(g8,g13)
    c: Distance(g9,g15) = 6
    c: Distance(g11,g13) = 6
    c: Coincident(g16,g4)
    c: PointOnObject(g10,g16)
    c: Radius(g16) = 18.9
    c: Coincident(g17,g4)
    c: Radius(g17) = 12.1
    c: PointOnObject(g8,g16)
    c: Coincident(g18,g4)
    c: Coincident(g19,g4)
    c: Radius(g18) = 12.2
    c: Radius(g19) = 18.8
    c: PointOnObject(g11,g19)
    c: PointOnObject(g9,g19)
    c: Coincident(g20,g10)
    c: Coincident(g20,g11)
    c: Tangent(g20,g19)
    c: Coincident(g21,g9)
    c: Coincident(g21,g8)
    c: Tangent(g21,g16)
    c: Coincident(g13,g6)
    c: Coincident(g22,g10)
    c: Coincident(g22,g11)
    c: PointOnObject(g22,g-2)
    c: PointOnObject(g8,g17)
    c: PointOnObject(g9,g18)
    c: Coincident(g23,g8)
    c: Coincident(g23,g9)
    c: PointOnObject(g23,g-2)
    c: PointOnObject(g10,g15)
    c: PointOnObject(g10,g17)
    c: PointOnObject(g11,g18)
FEATURE [PartDesign::Pad] Pad008
  Direction = (0,-1,2e-16)
  Length = 1.5
  Length2 = 10
  Placement = pos=(0,0,0) rot=(1,0,0;1.5708rad)
  Profile = -> Sketch011 [Edge9,Edge12,Edge10,Edge11]
  ReferenceAxis = -> Sketch011 [N_Axis]
  Refine = true
  Reversed = true
  Suppressed = false
  Type = 0
  expr: Length = VarSet.Base_pogopin_cutout_height
FEATURE [PartDesign::Pad] Pad009
  BaseFeature = -> Pad008
  Direction = (0,-1,2e-16)
  Length = 12
  Length2 = 10
  Placement = pos=(0,0,0) rot=(1,0,0;1.5708rad)
  Profile = -> Sketch011 [Edge1,Edge4,Edge3,Edge2,Edge8,Edge7,Edge6,Edge5]
  ReferenceAxis = -> Sketch011 [N_Axis]
  Refine = true
  Suppressed = false
  Type = 0
  expr: Length = VarSet.Base_connector_height_lug
FEATURE [Sketcher::SketchObject] Sketch012  label="luges_cutting"
  ArcFitTolerance = 1e-06
  AttachmentSupport = -> [XZ_Plane065]
  ExternalTypes = [0]
  FullyConstrained = true
  MakeInternals = false
  MapMode = 5
  Placement = pos=(0,0,0) rot=(1,0,0;1.5708rad)
  expr: Constraints[11] = VarSet.Base_connector_bounting_box_height
  expr: Constraints[21] = VarSet.Base_connector_lug_remaining_key - VarSet.Base_connector_lug_offset
  expr: Constraints[22] = VarSet.Base_connector_lug_remaining_key - VarSet.Base_connector_lug_offset
  expr: Constraints[26] = (VarSet.Base_connector_external_lug + VarSet.Base_connector_internal_lug) / 2 + VarSet.Base_connector_lug_offset
  expr: Constraints[27] = (VarSet.Base_connector_external_lug + VarSet.Base_connector_internal_lug) / 2 - VarSet.Base_connecot_lug_multipl * VarSet.Base_connector_lug_offset
  expr: Constraints[28] = VarSet.Base_connector_internal_lug - VarSet.Base_connecot_lug_multipl * VarSet.Base_connector_lug_offset
  expr: Constraints[3] = VarSet.base_width
  expr: Constraints[6] = VarSet.case_height / 2
  sketch-geometry (17):
    g0: LineSegment [constr] StartX=-32.5 StartY=-1.5 StartZ=0 EndX=-32.5 EndY=-23.5 EndZ=0
    g1: LineSegment [constr] StartX=-32.5 StartY=-23.5 StartZ=0 EndX=32.5 EndY=-23.5 EndZ=0
    g2: LineSegment [constr] StartX=32.5 StartY=-23.5 StartZ=0 EndX=32.5 EndY=-1.5 EndZ=0
    g3: GeomPoint X=0 Y=-12.5 Z=0
    g4: LineSegment [constr] StartX=-32.5 StartY=-12.5 StartZ=0 EndX=32.5 EndY=-12.5 EndZ=0
    g5: LineSegment StartX=10.641 StartY=-17.6 StartZ=0 EndX=14.425 EndY=-17.6 EndZ=0
    g6: LineSegment [constr] StartX=-32.5 StartY=-1.5 StartZ=0 EndX=32.5 EndY=-1.5 EndZ=0
    g7: LineSegment StartX=-14.425 StartY=-7.4 StartZ=0 EndX=-10.641 EndY=-7.4 EndZ=0
    g8: LineSegment StartX=-4.27083 StartY=-23.5 StartZ=0 EndX=-11.0616 EndY=-23.5 EndZ=0
    g9: LineSegment StartX=4.27083 StartY=-1.5 StartZ=0 EndX=11.0616 EndY=-1.5 EndZ=0
    g10: Circle [constr] CenterX=0 CenterY=-12.5 CenterZ=0 NormalX=0 NormalY=0 NormalZ=1 AngleXU=0 Radius=15.3
    g11: Circle [constr] CenterX=0 CenterY=-12.5 CenterZ=0 NormalX=0 NormalY=0 NormalZ=1 AngleXU=0 Radius=11.8
    g12: Circle [constr] CenterX=0 CenterY=-12.5 CenterZ=0 NormalX=0 NormalY=0 NormalZ=1 AngleXU=0 Radius=15.6
    g13: ArcOfCircle CenterX=0 CenterY=-12.5 CenterZ=0 NormalX=0 NormalY=0 NormalZ=1 AngleXU=0 Radius=11.8 StartAngle=5.83625 EndAngle=7.48364
    g14: ArcOfCircle CenterX=0 CenterY=-12.2121 CenterZ=0 NormalX=0 NormalY=0 NormalZ=1 AngleXU=0 Radius=15.3984 StartAngle=5.92572 EndAngle=7.05253
    g15: ArcOfCircle CenterX=0 CenterY=-12.5 CenterZ=0 NormalX=0 NormalY=0 NormalZ=1 AngleXU=0 Radius=11.8 StartAngle=2.69466 EndAngle=4.34205
    g16: ArcOfCircle CenterX=0 CenterY=-12.7879 CenterZ=0 NormalX=0 NormalY=0 NormalZ=1 AngleXU=0 Radius=15.3984 StartAngle=2.78413 EndAngle=3.91094
  constraints (49):
    c: Vertical(g0)
    c: Vertical(g2)
    c: Horizontal(g1)
    c: DistanceX(g0,g2) = 65
    c: Symmetric(g0,g2,g-2)
    c: PointOnObject(g3,g-2)
    c: DistanceY(g3,g-1) = 12.5
    c: Symmetric(g0,g0,g4)
    c: Symmetric(g2,g2,g4)
    c: Coincident(g1,g2)
    c: Coincident(g1,g0)
    c: DistanceY(g1,g2) = 22
    c: Coincident(g6,g0)
    c: Coincident(g6,g2)
    c: PointOnObject(g3,g4)
    c: PointOnObject(g9,g6)
    c: PointOnObject(g8,g1)
    c: PointOnObject(g8,g1)
    c: PointOnObject(g9,g6)
    c: Parallel(g7,g6)
    c: Parallel(g1,g5)
    c: Distance(g7,g6) = 5.9
    c: Distance(g5,g1) = 5.9
    c: Coincident(g10,g3)
    c: Coincident(g11,g3)
    c: Coincident(g12,g3)
    c: Radius(g12) = 15.6
    c: Radius(g10) = 15.3
    c: Radius(g11) = 11.8
    c: PointOnObject(g8,g12)
    c: PointOnObject(g8,g11)
    c: PointOnObject(g9,g12)
    c: PointOnObject(g9,g11)
    c: PointOnObject(g5,g10)
    c: Coincident(g13,g9)
    c: Coincident(g13,g5)
    c: PointOnObject(g13,g-2)
    c: Coincident(g14,g9)
    c: Coincident(g14,g5)
    c: PointOnObject(g14,g-2)
    c: PointOnObject(g7,g10)
    c: Coincident(g15,g8)
    c: Coincident(g15,g7)
    c: Coincident(g16,g7)
    c: Coincident(g16,g8)
    c: PointOnObject(g16,g-2)
    c: PointOnObject(g15,g-2)
    c: PointOnObject(g7,g11)
    c: PointOnObject(g5,g11)
FEATURE [PartDesign::Pocket] Pocket012
  BaseFeature = -> Pad009
  Direction = (0,1,-2e-16)
  Length = 6.7
  Length2 = 5
  Placement = pos=(0,0,0) rot=(1,0,0;1.5708rad)
  Profile = -> Sketch012
  ReferenceAxis = -> Sketch012 [N_Axis]
  Refine = true
  Reversed = true
  Suppressed = false
  Type = 0
  expr: Length = VarSet.Base_connector_height_lug / 2 + 5 * VarSet.Base_connector_lug_offset + VarSet.Base_connector_oring_offset
FEATURE [App::Point] Origin134
  Role = Origin
FEATURE [Sketcher::SketchObject] Sketch013  label="main_luge"
  ArcFitTolerance = 1e-06
  AttachmentSupport = -> [XZ_Plane066]
  ExternalTypes = [0]
  FullyConstrained = true
  MakeInternals = false
  MapMode = 5
  Placement = pos=(0,0,0) rot=(1,0,0;1.5708rad)
  expr: Constraints[10] = VarSet.case_height
  expr: Constraints[12] = VarSet.case_height / 2
  expr: Constraints[17] = VarSet.Base_connector_bounting_box_height
  expr: Constraints[29] = VarSet.Base_connector_external_lug
  expr: Constraints[34] = VarSet.Base_connector_external_lug
  expr: Constraints[48] = VarSet.Base_connector_internal_lug
  expr: Constraints[50] = VarSet.Base_connector_internal_lug
  expr: Constraints[52] = VarSet.Base_connector_lug_remaining_key
  expr: Constraints[53] = VarSet.Base_connector_lug_remaining_key
  expr: Constraints[9] = VarSet.base_width
  sketch-geometry (20):
    g0: LineSegment [constr] StartX=-32.5 StartY=0 StartZ=0 EndX=-32.5 EndY=-25 EndZ=0
    g1: LineSegment [constr] StartX=-32.5 StartY=-25 StartZ=0 EndX=32.5 EndY=-25 EndZ=0
    g2: LineSegment [constr] StartX=32.5 StartY=-25 StartZ=0 EndX=32.5 EndY=0 EndZ=0
    g3: LineSegment [constr] StartX=32.5 StartY=0 StartZ=0 EndX=-32.5 EndY=0 EndZ=0
    g4: GeomPoint X=0 Y=-12.5 Z=0
    g5: LineSegment [constr] StartX=-32.5 StartY=-1.5 StartZ=0 EndX=32.5 EndY=-1.5 EndZ=0
    g6: LineSegment [constr] StartX=-32.5 StartY=-23.5 StartZ=0 EndX=32.5 EndY=-23.5 EndZ=0
    g7: LineSegment [constr] StartX=-32.5 StartY=-1.5 StartZ=0 EndX=32.5 EndY=-23.5 EndZ=0
    g8: ArcOfCircle CenterX=0 CenterY=-12.5 CenterZ=0 NormalX=0 NormalY=0 NormalZ=1 AngleXU=0 Radius=12 StartAngle=5.85341 EndAngle=7.44284
    g9: ArcOfCircle CenterX=0 CenterY=-12.5 CenterZ=0 NormalX=0 NormalY=0 NormalZ=1 AngleXU=0 Radius=19 StartAngle=6.01689 EndAngle=6.90062
    g10: LineSegment StartX=10.9087 StartY=-17.5 StartZ=0 EndX=18.3303 EndY=-17.5 EndZ=0
    g11: LineSegment StartX=4.79583 StartY=-1.5 StartZ=0 EndX=15.4919 EndY=-1.5 EndZ=0
    g12: ArcOfCircle CenterX=0 CenterY=-12.5 CenterZ=0 NormalX=0 NormalY=0 NormalZ=1 AngleXU=0 Radius=12 StartAngle=2.71182 EndAngle=4.30125
    g13: ArcOfCircle CenterX=0 CenterY=-12.5 CenterZ=0 NormalX=0 NormalY=0 NormalZ=1 AngleXU=0 Radius=19 StartAngle=2.8753 EndAngle=3.75903
    g14: LineSegment StartX=-18.3303 StartY=-7.5 StartZ=0 EndX=-10.9087 EndY=-7.5 EndZ=0
    g15: LineSegment StartX=-15.4919 StartY=-23.5 StartZ=0 EndX=-4.79583 EndY=-23.5 EndZ=0
    g16: LineSegment StartX=-32.5 StartY=-1.5 StartZ=0 EndX=-32.5 EndY=-23.5 EndZ=0
    g17: LineSegment StartX=-32.5 StartY=-23.5 StartZ=0 EndX=32.5 EndY=-23.5 EndZ=0
    g18: LineSegment StartX=32.5 StartY=-23.5 StartZ=0 EndX=32.5 EndY=-1.5 EndZ=0
    g19: LineSegment StartX=32.5 StartY=-1.5 StartZ=0 EndX=-32.5 EndY=-1.5 EndZ=0
  constraints (56):
    c: Coincident(g0,g1)
    c: Coincident(g1,g2)
    c: Coincident(g2,g3)
    c: Coincident(g3,g0)
    c: Vertical(g0)
    c: Vertical(g2)
    c: Horizontal(g1)
    c: PointOnObject(g0,g-1)
    c: Symmetric(g0,g2,g-2)
    c: DistanceX(g0,g2) = 65
    c: DistanceY(g0,g-1) = 25
    c: PointOnObject(g4,g-2)
    c: DistanceY(g4,g-1) = 12.5
    c: PointOnObject(g6,g0)
    c: Horizontal(g6)
    c: PointOnObject(g6,g2)
    c: PointOnObject(g5,g2)
    c: DistanceY(g6,g5) = 22
    c: PointOnObject(g5,g0)
    c: Parallel(g5,g3)
    c: Coincident(g7,g5)
    c: Coincident(g7,g6)
    c: PointOnObject(g4,g7)
    c: Coincident(g8,g4)
    c: Coincident(g9,g4)
    c: Coincident(g10,g8)
    c: Coincident(g10,g9)
    c: Coincident(g9,g11)
    c: Parallel(g11,g3)
    c: Radius(g9) = 19
    c: Coincident(g12,g4)
    c: Coincident(g13,g4)
    c: Coincident(g14,g13)
    c: Coincident(g14,g12)
    c: Radius(g13) = 19
    c: Coincident(g15,g13)
    c: Parallel(g15,g5)
    c: Coincident(g16,g17)
    c: Coincident(g17,g18)
    c: Coincident(g18,g19)
    c: Coincident(g19,g16)
    c: Vertical(g16)
    c: Horizontal(g17)
    c: Symmetric(g16,g18,g-2)
    c: Parallel(g10,g5)
    c: Parallel(g14,g5)
    c: Coincident(g16,g5)
    c: Coincident(g17,g6)
    c: Radius(g12) = 12
    c: PointOnObject(g12,g6)
    c: Radius(g8) = 12
    c: PointOnObject(g8,g5)
    c: Distance(g9,g17) = 6
    c: Distance(g12,g19) = 6
    c: Coincident(g11,g8)
    c: Coincident(g15,g12)
FEATURE [Sketcher::SketchObject] Sketch014
  ArcFitTolerance = 1e-06
  AttachmentSupport = -> [XZ_Plane066]
  ExternalTypes = [0]
  FullyConstrained = true
  MakeInternals = false
  MapMode = 5
  Placement = pos=(0,0,0) rot=(1,0,0;1.5708rad)
  expr: Constraints[11] = VarSet.Base_connector_bounting_box_height
  expr: Constraints[18] = (VarSet.Base_connector_external_lug + VarSet.Base_connector_internal_lug) / 2
  expr: Constraints[19] = (VarSet.Base_connector_external_lug + VarSet.Base_connector_internal_lug) / 2
  expr: Constraints[24] = VarSet.Base_connector_internal_lug
  expr: Constraints[28] = VarSet.Base_connector_internal_lug
  expr: Constraints[36] = VarSet.Base_connector_bounting_box_height - VarSet.Base_connector_height_lug
  expr: Constraints[38] = VarSet.Base_connector_bounting_box_height - VarSet.Base_connector_height_lug
  expr: Constraints[3] = VarSet.base_width
  expr: Constraints[6] = VarSet.case_height / 2
  sketch-geometry (14):
    g0: LineSegment [constr] StartX=-32.5 StartY=-1.5 StartZ=0 EndX=-32.5 EndY=-23.5 EndZ=0
    g1: LineSegment [constr] StartX=-32.5 StartY=-23.5 StartZ=0 EndX=32.5 EndY=-23.5 EndZ=0
    g2: LineSegment [constr] StartX=32.5 StartY=-23.5 StartZ=0 EndX=32.5 EndY=-1.5 EndZ=0
    g3: GeomPoint X=0 Y=-12.5 Z=0
    g4: LineSegment [constr] StartX=-32.5 StartY=-12.5 StartZ=0 EndX=32.5 EndY=-12.5 EndZ=0
    g5: LineSegment StartX=11.9583 StartY=-13.5 StartZ=0 EndX=15.4677 EndY=-13.5 EndZ=0
    g6: LineSegment [constr] StartX=-32.5 StartY=-1.5 StartZ=0 EndX=32.5 EndY=-1.5 EndZ=0
    g7: ArcOfCircle CenterX=0 CenterY=-12.5 CenterZ=0 NormalX=0 NormalY=0 NormalZ=1 AngleXU=0 Radius=15.5 StartAngle=6.21862 EndAngle=7.07223
    g8: ArcOfCircle CenterX=-1.6e-15 CenterY=-12.5 CenterZ=0 NormalX=0 NormalY=0 NormalZ=1 AngleXU=0 Radius=15.5 StartAngle=3.07703 EndAngle=3.93063
    g9: LineSegment StartX=-15.4677 StartY=-11.5 StartZ=0 EndX=-11.9583 EndY=-11.5 EndZ=0
    g10: ArcOfCircle CenterX=-1.6e-15 CenterY=-12.5 CenterZ=0 NormalX=0 NormalY=0 NormalZ=1 AngleXU=0 Radius=12 StartAngle=3.05816 EndAngle=4.30125
    g11: LineSegment StartX=-4.79583 StartY=-23.5 StartZ=0 EndX=-10.9202 EndY=-23.5 EndZ=0
    g12: ArcOfCircle CenterX=0 CenterY=-12.5 CenterZ=0 NormalX=0 NormalY=0 NormalZ=1 AngleXU=0 Radius=12 StartAngle=6.19976 EndAngle=7.44284
    g13: LineSegment StartX=4.79583 StartY=-1.5 StartZ=0 EndX=10.9202 EndY=-1.5 EndZ=0
  constraints (39):
    c: Vertical(g0)
    c: Vertical(g2)
    c: Horizontal(g1)
    c: DistanceX(g0,g2) = 65
    c: Symmetric(g0,g2,g-2)
    c: PointOnObject(g3,g-2)
    c: DistanceY(g3,g-1) = 12.5
    c: Symmetric(g0,g0,g4)
    c: Symmetric(g2,g2,g4)
    c: Coincident(g1,g2)
    c: Coincident(g1,g0)
    c: DistanceY(g1,g2) = 22
    c: Coincident(g6,g0)
    c: Coincident(g6,g2)
    c: PointOnObject(g3,g4)
    c: Coincident(g7,g3)
    c: Coincident(g7,g5)
    c: Symmetric(g4,g4,g8)
    c: Radius(g7) = 15.5
    c: Radius(g8) = 15.5
    c: Coincident(g8,g9)
    c: Coincident(g10,g8)
    c: Coincident(g10,g9)
    c: Coincident(g11,g10)
    c: Radius(g10) = 12
    c: Coincident(g8,g11)
    c: Coincident(g12,g3)
    c: Coincident(g12,g5)
    c: Radius(g12) = 12
    c: Coincident(g13,g12)
    c: Coincident(g13,g7)
    c: Parallel(g9,g6)
    c: Parallel(g1,g5)
    c: Parallel(g11,g1)
    c: Parallel(g13,g1)
    c: PointOnObject(g10,g1)
    c: Distance(g8,g6) = 10
    c: PointOnObject(g7,g6)
    c: Distance(g5,g1) = 10
FEATURE [Part::Feature] Part__Feature  label="Magnetic Pogo Connector 3 Pin (Type 1)"
  shape: bbox 15 x 4 x 4 mm, 35 faces (baked)
FEATURE [Part::Feature] Part__Feature079  label="Magnetic Pogo Connector 3 Pin (Type 1)001"
  shape: bbox 1.624 x 5.754 x 1.624 mm, 8 faces (baked)
FEATURE [Part::Feature] Part__Feature080  label="Magnetic Pogo Connector 3 Pin (Type 1)002"
  shape: bbox 3.247 x 4 x 3.247 mm, 16 faces (baked)
FEATURE [Part::Feature] Part__Feature081  label="Magnetic Pogo Connector 3 Pin (Type 1)003"
  shape: bbox 3.247 x 4 x 3.247 mm, 22 faces (baked)
FEATURE [Part::Feature] Part__Feature082  label="Magnetic Pogo Connector 3 Pin (Type 1)004"
  shape: bbox 1.624 x 5.754 x 1.624 mm, 8 faces (baked)
FEATURE [Part::Feature] Part__Feature083  label="Magnetic Pogo Connector 3 Pin (Type 1)005"
  shape: bbox 1.624 x 5.754 x 1.624 mm, 8 faces (baked)
FEATURE [App::Part] Magnetic_Pogo_Connector_3_Pin__Type_1_  label="Magnetic Pogo Connector 3 Pin (Type 1)006"
  Group = -> [Part__Feature,Part__Feature079,Part__Feature080,Part__Feature081,Part__Feature082,Part__Feature083]
  Origin = -> Origin135
  Placement = pos=(0,-5,-12.5) rot=(0,0,1;0rad)
FEATURE [App::Point] Origin136
  Role = Origin
FEATURE [Part::Feature] Part__Feature085  label="Magnetic Pogo Connector 3 Pin (Type 2)001"
  shape: bbox 1.5 x 6.65 x 1.5 mm, 9 faces (baked)
FEATURE [Part::Feature] Part__Feature086  label="Magnetic Pogo Connector 3 Pin (Type 2)002"
  shape: bbox 3.247 x 4 x 3.247 mm, 16 faces (baked)
FEATURE [Part::Feature] Part__Feature087  label="Magnetic Pogo Connector 3 Pin (Type 2)003"
  shape: bbox 3.247 x 4 x 3.247 mm, 22 faces (baked)
FEATURE [Part::Feature] Part__Feature088  label="Magnetic Pogo Connector 3 Pin (Type 2)004"
  shape: bbox 1.5 x 6.65 x 1.5 mm, 9 faces (baked)
FEATURE [Part::Feature] Part__Feature089  label="Magnetic Pogo Connector 3 Pin (Type 2)005"
  shape: bbox 1.5 x 6.65 x 1.5 mm, 9 faces (baked)
FEATURE [App::Point] Origin138
  Role = Origin
FEATURE [Sketcher::SketchObject] Sketch018  label="pogopins_case001"
  ArcFitTolerance = 1e-06
  AttachmentSupport = -> [XZ_Plane065]
  ExternalTypes = [0]
  FullyConstrained = true
  MakeInternals = false
  MapMode = 5
  Placement = pos=(0,0,0) rot=(1,0,0;1.5708rad)
  expr: Constraints[12] = VarSet.Base_pogopins_r
  expr: Constraints[1] = VarSet.case_height / 2
  expr: Constraints[25] = VarSet.Base_pogoping_lenght
  sketch-geometry (11):
    g0: GeomPoint X=0 Y=-12.5 Z=0
    g1: ArcOfCircle CenterX=-5.45 CenterY=-12.5 CenterZ=0 NormalX=0 NormalY=0 NormalZ=1 AngleXU=0 Radius=2.1 StartAngle=1.5708 EndAngle=4.71239
    g2: ArcOfCircle CenterX=5.45 CenterY=-12.5 CenterZ=0 NormalX=0 NormalY=0 NormalZ=1 AngleXU=0 Radius=2.1 StartAngle=4.71239 EndAngle=7.85398
    g3: LineSegment StartX=-5.45 StartY=-10.4 StartZ=0 EndX=5.45 EndY=-10.4 EndZ=0
    g4: LineSegment StartX=-5.45 StartY=-14.6 StartZ=0 EndX=5.45 EndY=-14.6 EndZ=0
    g5: LineSegment [constr] StartX=-5.45 StartY=-12.5 StartZ=0 EndX=5.45 EndY=-12.5 EndZ=0
    g6: GeomPoint [constr] X=0 Y=-12.5 Z=0
    g7: LineSegment [constr] StartX=-7.55 StartY=-10.4 StartZ=0 EndX=-7.55 EndY=-14.6 EndZ=0
    g8: LineSegment [constr] StartX=-7.55 StartY=-14.6 StartZ=0 EndX=7.55 EndY=-14.6 EndZ=0
    g9: LineSegment [constr] StartX=7.55 StartY=-14.6 StartZ=0 EndX=7.55 EndY=-10.4 EndZ=0
    g10: LineSegment [constr] StartX=7.55 StartY=-10.4 StartZ=0 EndX=-7.55 EndY=-10.4 EndZ=0
  constraints (26):
    c: PointOnObject(g0,g-2)
    c: Distance(g0,g-1) = 12.5
    c: Tangent(g1,g3) = 1.5708
    c: Tangent(g1,g4) = -1.5708
    c: Tangent(g2,g3) = 1.5708
    c: Tangent(g2,g4) = -1.5708
    c: Equal(g1,g2)
    c: Horizontal(g3)
    c: Coincident(g5,g1)
    c: Coincident(g5,g2)
    c: Symmetric(g5,g5,g6)
    c: Coincident(g0,g6)
    c: Radius(g1) = 2.1
    c: Coincident(g7,g8)
    c: Coincident(g8,g9)
    c: Coincident(g9,g10)
    c: Coincident(g10,g7)
    c: Vertical(g7)
    c: Vertical(g9)
    c: Horizontal(g8)
    c: Horizontal(g10)
    c: PointOnObject(g2,g10)
    c: PointOnObject(g2,g8)
    c: Tangent(g2,g9)
    c: Tangent(g7,g1)
    c: DistanceX(g7,g9) = 15.1
FEATURE [PartDesign::Pocket] Pocket016  label="pogopins"
  BaseFeature = -> Pocket012
  Direction = (0,1,-2e-16)
  Length = 12
  Length2 = 5
  Midplane = true
  Placement = pos=(0,0,0) rot=(1,0,0;1.5708rad)
  Profile = -> Sketch018
  ReferenceAxis = -> Sketch018 [N_Axis]
  Refine = true
  Suppressed = false
  Type = 0
  expr: Length = VarSet.Base_connector_height_lug
FEATURE [Sketcher::SketchObject] Sketch022  label="pogopins_outside"
  ArcFitTolerance = 1e-06
  ExternalTypes = [0]
  FullyConstrained = true
  MakeInternals = false
  MapMode = 5
  Placement = pos=(0,3,0) rot=(0,0.707107,0.707107;3.14159rad)
  expr: Constraints[11] = VarSet.case_height / 2
  expr: Constraints[12] = VarSet.Base_pogopin_outside
  expr: Constraints[13] = 3 * VarSet.Base_pogopins_r
  sketch-geometry (6):
    g0: GeomPoint X=0 Y=-12.5 Z=0
    g1: LineSegment StartX=-10.5 StartY=-9.35 StartZ=0 EndX=-10.5 EndY=-15.65 EndZ=0
    g2: LineSegment StartX=-10.5 StartY=-15.65 StartZ=0 EndX=10.5 EndY=-15.65 EndZ=0
    g3: LineSegment StartX=10.5 StartY=-15.65 StartZ=0 EndX=10.5 EndY=-9.35 EndZ=0
    g4: LineSegment StartX=10.5 StartY=-9.35 StartZ=0 EndX=-10.5 EndY=-9.35 EndZ=0
    g5: GeomPoint [constr] X=0 Y=-12.5 Z=0
  constraints (14):
    c: PointOnObject(g0,g-2)
    c: Coincident(g1,g2)
    c: Coincident(g2,g3)
    c: Coincident(g3,g4)
    c: Coincident(g4,g1)
    c: Vertical(g1)
    c: Vertical(g3)
    c: Horizontal(g2)
    c: Horizontal(g4)
    c: Symmetric(g3,g1,g5)
    c: Coincident(g5,g0)
    c: DistanceY(g0,g-1) = 12.5
    c: DistanceX(g1,g3) = 21
    c: DistanceY(g2,g3) = 6.3
FEATURE [PartDesign::Pocket] Pocket020
  BaseFeature = -> Pad005
  Direction = (-1e-16,-1,2e-16)
  Length = 3
  Length2 = 5
  Profile = -> Sketch022
  ReferenceAxis = -> Sketch022 [N_Axis]
  Refine = true
  Suppressed = false
  Type = 0
  expr: Length = VarSet.Base_case_thickness
FEATURE [App::Link] Magnetic_Pogo_Connector_3_Pin__Type_2_006  label="Magnetic Pogo Connector 3 Pin (Type 2)007"
  LinkPlacement = pos=(0.05,-8.7,-12.5) rot=(0,0,1;3.14159rad)
  LinkedObject = -> Magnetic_Pogo_Connector_3_Pin__Type_2_
  Placement = pos=(0.05,-8.7,-12.5) rot=(0,0,1;3.14159rad)
FEATURE [App::Link] Magnetic_Pogo_Connector_3_Pin__Type_1_006  label="Magnetic Pogo Connector 3 Pin (Type 1)007"
  LinkPlacement = pos=(0.166708,-35.55,-12.3449) rot=(0,1,0;3.14159rad)
  LinkedObject = -> Magnetic_Pogo_Connector_3_Pin__Type_1_
  Placement = pos=(0.166708,-35.55,-12.3449) rot=(0,1,0;3.14159rad)
FEATURE [PartDesign::Pad] Pad010
  Direction = (0,-1,2e-16)
  Length = 12
  Length2 = 10
  Placement = pos=(0,0,0) rot=(1,0,0;1.5708rad)
  Profile = -> Sketch013 [Edge9,Edge12,Edge10,Edge11]
  ReferenceAxis = -> Sketch013 [N_Axis]
  Refine = true
  Suppressed = false
  Type = 0
  expr: Length = VarSet.Base_connector_height_lug
FEATURE [PartDesign::Pocket] Pocket021
  BaseFeature = -> Pad010
  Direction = (0,1,-2e-16)
  Length = 6.2
  Length2 = 5
  Placement = pos=(0,0,0) rot=(1,0,0;1.5708rad)
  Profile = -> Sketch013 [Edge7,Edge8,Edge6,Edge5,Edge3,Edge2,Edge4,Edge1]
  ReferenceAxis = -> Sketch013 [N_Axis]
  Refine = true
  Reversed = true
  Suppressed = false
  Type = 0
  expr: Length = VarSet.Base_connector_height_lug / 2 + VarSet.Base_connector_oring_offset
FEATURE [Sketcher::SketchObject] Sketch016
  ArcFitTolerance = 1e-06
  AttachmentSupport = -> [Pocket021]
  ExternalTypes = [0]
  FullyConstrained = false
  MakeInternals = false
  MapMode = 5
  Placement = pos=(0,-12,0) rot=(1,0,0;1.5708rad)
  expr: Constraints[11] = VarSet.Base_connector_bounting_box_height
  expr: Constraints[17] = VarSet.Base_connector_external_lug
  expr: Constraints[18] = 19
  expr: Constraints[20] = VarSet.Base_connector_internal_lug
  expr: Constraints[28] = (VarSet.Base_connector_external_lug + VarSet.Base_connector_internal_lug) / 2
  expr: Constraints[39] = VarSet.Base_connector_lug_remaining_key
  expr: Constraints[3] = VarSet.base_width
  expr: Constraints[47] = (VarSet.Base_connector_external_lug + VarSet.Base_connector_internal_lug) / 2
  expr: Constraints[48] = VarSet.Base_connector_internal_lug
  expr: Constraints[54] = VarSet.Base_connector_lug_remaining_key
  expr: Constraints[6] = VarSet.case_height / 2
  sketch-geometry (20):
    g0: LineSegment [constr] StartX=-32.5 StartY=-1.5 StartZ=0 EndX=-32.5 EndY=-23.5 EndZ=0
    g1: LineSegment [constr] StartX=-32.5 StartY=-23.5 StartZ=0 EndX=32.5 EndY=-23.5 EndZ=0
    g2: LineSegment [constr] StartX=32.5 StartY=-23.5 StartZ=0 EndX=32.5 EndY=-1.5 EndZ=0
    g3: GeomPoint X=0 Y=-12.5 Z=0
    g4: LineSegment [constr] StartX=-32.5 StartY=-12.5 StartZ=0 EndX=32.5 EndY=-12.5 EndZ=0
    g5: LineSegment [constr] StartX=-32.5 StartY=-1.5 StartZ=0 EndX=32.5 EndY=-1.5 EndZ=0
    g6: ArcOfCircle CenterX=0 CenterY=-12.5 CenterZ=0 NormalX=0 NormalY=0 NormalZ=1 AngleXU=0 Radius=19 StartAngle=5.66575 EndAngle=6.90062
    g7: ArcOfCircle CenterX=-3e-16 CenterY=-12.5 CenterZ=0 NormalX=0 NormalY=0 NormalZ=1 AngleXU=0 Radius=19 StartAngle=2.52416 EndAngle=3.75903
    g8: ArcOfCircle CenterX=0 CenterY=-12.5 CenterZ=0 NormalX=0 NormalY=0 NormalZ=1 AngleXU=0 Radius=12 StartAngle=0.429775 EndAngle=1.15966
    g9: ArcOfCircle CenterX=0 CenterY=-12.5 CenterZ=0 NormalX=0 NormalY=0 NormalZ=1 AngleXU=0 Radius=15.5 StartAngle=5.49415 EndAngle=6.61164
    g10: LineSegment [constr] StartX=-15.4919 StartY=-1.5 StartZ=0 EndX=-4.79582 EndY=-1.5 EndZ=0
    g11: LineSegment [constr] StartX=-13.0749 StartY=-23.5 StartZ=0 EndX=-4.79583 EndY=-23.5 EndZ=0
    g12: LineSegment StartX=15.4919 StartY=-1.5 StartZ=0 EndX=4.79583 EndY=-1.5 EndZ=0
    g13: LineSegment StartX=15.4919 StartY=-23.5 StartZ=0 EndX=10.9202 EndY=-23.5 EndZ=0
    g14: LineSegment StartX=14.6714 StartY=-7.5 StartZ=0 EndX=10.9087 EndY=-7.5 EndZ=0
    g15: LineSegment StartX=-15.4919 StartY=-23.5 StartZ=0 EndX=-4.79583 EndY=-23.5 EndZ=0
    g16: LineSegment StartX=-10.9202 StartY=-1.5 StartZ=0 EndX=-15.4919 EndY=-1.5 EndZ=0
    g17: LineSegment StartX=-14.6714 StartY=-17.5 StartZ=0 EndX=-10.9087 EndY=-17.5 EndZ=0
    g18: ArcOfCircle CenterX=-3e-16 CenterY=-12.5 CenterZ=0 NormalX=0 NormalY=0 NormalZ=1 AngleXU=0 Radius=15.5 StartAngle=2.35255 EndAngle=3.47005
    g19: ArcOfCircle CenterX=0 CenterY=-12.5 CenterZ=0 NormalX=0 NormalY=0 NormalZ=1 AngleXU=0 Radius=12 StartAngle=3.57137 EndAngle=4.30125
  constraints (55):
    c: Vertical(g0)
    c: Vertical(g2)
    c: Horizontal(g1)
    c: DistanceX(g0,g2) = 65
    c: Symmetric(g0,g2,g-2)
    c: PointOnObject(g3,g-2)
    c: DistanceY(g3,g-1) = 12.5
    c: Symmetric(g0,g0,g4)
    c: Symmetric(g2,g2,g4)
    c: Coincident(g1,g2)
    c: Coincident(g1,g0)
    c: DistanceY(g1,g2) = 22
    c: Coincident(g5,g0)
    c: Coincident(g5,g2)
    c: PointOnObject(g3,g4)
    c: Coincident(g6,g3)
    c: Symmetric(g4,g4,g7)
    c: Radius(g6) = 19
    c: Radius(g7) = 19
    c: Coincident(g8,g3)
    c: Radius(g8) = 12
    c: Coincident(g9,g3)
    c: PointOnObject(g8,g5)
    c: PointOnObject(g10,g5)
    c: PointOnObject(g11,g1)
    c: PointOnObject(g7,g5)
    c: Coincident(g10,g7)
    c: PointOnObject(g11,g1)
    c: Radius(g9) = 15.5
    c: PointOnObject(g6,g5)
    c: Coincident(g12,g6)
    c: Coincident(g12,g8)
    c: PointOnObject(g6,g1)
    c: Coincident(g13,g9)
    c: Horizontal(g13)
    c: Coincident(g14,g9)
    c: Parallel(g14,g5)
    c: Coincident(g14,g8)
    c: Coincident(g13,g6)
    c: Distance(g8,g5) = 6
    c: Coincident(g16,g7)
    c: Horizontal(g17)
    c: PointOnObject(g16,g5)
    c: Coincident(g18,g7)
    c: Coincident(g18,g16)
    c: Coincident(g19,g3)
    c: Coincident(g19,g15)
    c: Radius(g18) = 15.5
    c: Radius(g19) = 12
    c: Coincident(g17,g19)
    c: Coincident(g17,g18)
    c: Coincident(g7,g15)
    c: PointOnObject(g7,g1)
    c: PointOnObject(g15,g1)
    c: Distance(g7,g17) = 6
FEATURE [PartDesign::Pocket] Pocket022
  BaseFeature = -> Pocket021
  Direction = (0,1,-2e-16)
  Length = 6
  Length2 = 5
  Placement = pos=(0,0,0) rot=(1,0,0;1.5708rad)
  Profile = -> Sketch016
  ReferenceAxis = -> Sketch016 [N_Axis]
  Refine = true
  Suppressed = false
  Type = 0
  expr: Length = VarSet.Base_connector_height_lug / 2
FEATURE [Sketcher::SketchObject] Sketch017  label="pogo_pins001"
  ArcFitTolerance = 1e-06
  AttachmentSupport = -> [Pocket022]
  ExternalTypes = [0]
  FullyConstrained = true
  MakeInternals = false
  MapMode = 5
  Placement = pos=(0,-12,0) rot=(1,0,0;1.5708rad)
  expr: Constraints[12] = VarSet.Base_pogopins_r
  expr: Constraints[1] = VarSet.case_height / 2
  expr: Constraints[25] = VarSet.Base_pogoping_lenght
  sketch-geometry (11):
    g0: GeomPoint X=0 Y=-12.5 Z=0
    g1: ArcOfCircle CenterX=-5.45 CenterY=-12.5 CenterZ=0 NormalX=0 NormalY=0 NormalZ=1 AngleXU=0 Radius=2.1 StartAngle=1.5708 EndAngle=4.71239
    g2: ArcOfCircle CenterX=5.45 CenterY=-12.5 CenterZ=0 NormalX=0 NormalY=0 NormalZ=1 AngleXU=0 Radius=2.1 StartAngle=4.71239 EndAngle=7.85398
    g3: LineSegment StartX=-5.45 StartY=-10.4 StartZ=0 EndX=5.45 EndY=-10.4 EndZ=0
    g4: LineSegment StartX=-5.45 StartY=-14.6 StartZ=0 EndX=5.45 EndY=-14.6 EndZ=0
    g5: LineSegment [constr] StartX=-5.45 StartY=-12.5 StartZ=0 EndX=5.45 EndY=-12.5 EndZ=0
    g6: GeomPoint [constr] X=0 Y=-12.5 Z=0
    g7: LineSegment [constr] StartX=-7.55 StartY=-10.4 StartZ=0 EndX=-7.55 EndY=-14.6 EndZ=0
    g8: LineSegment [constr] StartX=-7.55 StartY=-14.6 StartZ=0 EndX=7.55 EndY=-14.6 EndZ=0
    g9: LineSegment [constr] StartX=7.55 StartY=-14.6 StartZ=0 EndX=7.55 EndY=-10.4 EndZ=0
    g10: LineSegment [constr] StartX=7.55 StartY=-10.4 StartZ=0 EndX=-7.55 EndY=-10.4 EndZ=0
  constraints (26):
    c: PointOnObject(g0,g-2)
    c: Distance(g0,g-1) = 12.5
    c: Tangent(g1,g3) = 1.5708
    c: Tangent(g1,g4) = -1.5708
    c: Tangent(g2,g3) = 1.5708
    c: Tangent(g2,g4) = -1.5708
    c: Equal(g1,g2)
    c: Horizontal(g3)
    c: Coincident(g5,g1)
    c: Coincident(g5,g2)
    c: Symmetric(g5,g5,g6)
    c: Coincident(g0,g6)
    c: Radius(g1) = 2.1
    c: Coincident(g7,g8)
    c: Coincident(g8,g9)
    c: Coincident(g9,g10)
    c: Coincident(g10,g7)
    c: Vertical(g7)
    c: Vertical(g9)
    c: Horizontal(g8)
    c: Horizontal(g10)
    c: PointOnObject(g2,g10)
    c: PointOnObject(g2,g8)
    c: Tangent(g2,g9)
    c: Tangent(g7,g1)
    c: DistanceX(g7,g9) = 15.1
FEATURE [App::FeaturePython] Joint  label="battery_main"  # Assembly joint (typed FeaturePython)
  Activated = true
  AngleMax = 0
  AngleMin = 0
  Detach1 = false
  Detach2 = false
  Distance = 0
  Distance2 = 0
  EnableAngleMax = false
  EnableAngleMin = false
  EnableLengthMax = false
  EnableLengthMin = false
  JointType = 0 (Fixed)
  LengthMax = 0
  LengthMin = 0
  Offset2 = pos=(0,0,20) rot=(0,0,1;3.14159rad)
  Placement1 = pos=(6e-16,0,-12.5) rot=(1,0,0;1.5708rad)
  Placement2 = pos=(0.216708,-32,-12.6551) rot=(0,-0.707107,0.707107;3.14159rad)
  Reference1 = -> Assembly [base.Body.Face10,base.Body.Face10]
  Reference2 = -> Assembly [battery.Body005.Edge99,battery.Body005.Edge99]
FEATURE [PartDesign::Pocket] Pocket023  label="pogo_pins002"
  BaseFeature = -> Pocket022
  Direction = (0,1,-2e-16)
  Length = 1.5
  Length2 = 5
  Placement = pos=(0,0,0) rot=(1,0,0;1.5708rad)
  Profile = -> Sketch017
  ReferenceAxis = -> Sketch017 [N_Axis]
  Refine = true
  Suppressed = false
  Type = 0
  expr: Length = VarSet.Base_pogopin_cutout_height
FEATURE [Sketcher::SketchObject] Sketch023  label="pogo_pins_outside"
  ArcFitTolerance = 1e-06
  AttachmentSupport = -> [XZ_Plane066]
  ExternalTypes = [0]
  FullyConstrained = true
  MakeInternals = false
  MapMode = 5
  Placement = pos=(0,0,0) rot=(1,0,0;1.5708rad)
  expr: Constraints[12] = VarSet.Base_pogopin_outside
  expr: Constraints[13] = VarSet.Base_pogopins_r * 3
  expr: Constraints[1] = VarSet.case_height / 2
  sketch-geometry (6):
    g0: GeomPoint X=0 Y=-12.5 Z=0
    g1: LineSegment StartX=-10.5 StartY=-9.35 StartZ=0 EndX=-10.5 EndY=-15.65 EndZ=0
    g2: LineSegment StartX=-10.5 StartY=-15.65 StartZ=0 EndX=10.5 EndY=-15.65 EndZ=0
    g3: LineSegment StartX=10.5 StartY=-15.65 StartZ=0 EndX=10.5 EndY=-9.35 EndZ=0
    g4: LineSegment StartX=10.5 StartY=-9.35 StartZ=0 EndX=-10.5 EndY=-9.35 EndZ=0
    g5: GeomPoint [constr] X=0 Y=-12.5 Z=0
  constraints (14):
    c: PointOnObject(g0,g-2)
    c: DistanceY(g0,g-1) = 12.5
    c: Coincident(g1,g2)
    c: Coincident(g2,g3)
    c: Coincident(g3,g4)
    c: Coincident(g4,g1)
    c: Vertical(g1)
    c: Vertical(g3)
    c: Horizontal(g2)
    c: Horizontal(g4)
    c: Symmetric(g3,g1,g5)
    c: Coincident(g5,g0)
    c: Distance(g1,g3) = 21
    c: DistanceY(g2,g3) = 6.3
FEATURE [PartDesign::Pocket] Pocket024  label="pogo_pins_outside001"
  BaseFeature = -> Pocket023
  Direction = (0,1,-2e-16)
  Length = 10.5
  Length2 = 5
  Placement = pos=(0,0,0) rot=(1,0,0;1.5708rad)
  Profile = -> Sketch023
  ReferenceAxis = -> Sketch023 [N_Axis]
  Refine = true
  Reversed = true
  Suppressed = false
  Type = 0
  expr: Length = VarSet.Base_connector_height_lug - VarSet.Base_pogopin_cutout_height
FEATURE [App::Link] _8650_v002  label="18650 v003"
  LinkPlacement = pos=(19.6167,-108.966,-11.8449) rot=(0,-1,0;1.5708rad)
  LinkedObject = -> Part__Feature064
  Placement = pos=(19.6167,-108.966,-11.8449) rot=(0,-1,0;1.5708rad)
FEATURE [App::FeaturePython] Joint003  label="18650_battery"  # Assembly joint (typed FeaturePython)
  Activated = true
  AngleMax = 0
  AngleMin = 0
  Detach1 = false
  Detach2 = false
  Distance = 0
  Distance2 = 0
  EnableAngleMax = false
  EnableAngleMin = false
  EnableLengthMax = false
  EnableLengthMin = false
  JointType = 0 (Fixed)
  LengthMax = 0
  LengthMin = 0
  Offset2 = pos=(0,0,5) rot=(0,0,1;0rad)
  Placement1 = pos=(0,34.4664,0) rot=(0.57735,0.57735,0.57735;4.18879rad)
  Placement2 = pos=(-19.4,41,-12) rot=(1,0,0;1.5708rad)
  Reference1 = -> Assembly [_8650_v002.Face34,_8650_v002.Face34]
  Reference2 = -> Assembly [battery.Body002.Face106,battery.Body002.Face106]
FEATURE [App::FeaturePython] Joint004  label="18650_battery_2"  # Assembly joint (typed FeaturePython)
  Activated = true
  AngleMax = 0
  AngleMin = 0
  Detach1 = false
  Detach2 = false
  Distance = 0
  Distance2 = 0
  EnableAngleMax = false
  EnableAngleMin = false
  EnableLengthMax = false
  EnableLengthMin = false
  JointType = 0 (Fixed)
  LengthMax = 0
  LengthMin = 0
  Offset2 = pos=(0,0,6) rot=(0,0,1;0rad)
  Placement1 = pos=(0,34.4664,0) rot=(0.57735,0.57735,0.57735;4.18879rad)
  Placement2 = pos=(0.1,40,-12) rot=(1,0,0;1.5708rad)
  Reference1 = -> Assembly [_8650_v1.Face34,_8650_v1.Face34]
  Reference2 = -> Assembly [battery.Body002.Face108,battery.Body002.Face108]
FEATURE [App::FeaturePython] Joint005  label="RAK19003_main"  # Assembly joint (typed FeaturePython)
  Activated = true
  AngleMax = 0
  AngleMin = 0
  Detach1 = false
  Detach2 = false
  Distance = 0
  Distance2 = 0
  EnableAngleMax = false
  EnableAngleMin = false
  EnableLengthMax = false
  EnableLengthMin = false
  JointType = 0 (Fixed)
  LengthMax = 0
  LengthMin = 0
  Offset2 = pos=(0,0,-1) rot=(0,0,1;0rad)
  Placement1 = pos=(-15,26,-1.0098) rot=(0,0,1;0rad)
  Placement2 = pos=(-23.5,35,-17) rot=(1,0,0;3.14159rad)
  Reference1 = -> Assembly [RAK19003__Solid_.Edge111,RAK19003__Solid_.Edge111]
  Reference2 = -> Assembly [base.Body.Edge495,base.Body.Edge495]
FEATURE [App::FeaturePython] Joint006  label="RAK19003_RAK4631"  # Assembly joint (typed FeaturePython)
  Activated = true
  AngleMax = 0
  AngleMin = 0
  Detach1 = false
  Detach2 = false
  Distance = 0
  Distance2 = 0
  EnableAngleMax = false
  EnableAngleMin = false
  EnableLengthMax = false
  EnableLengthMin = false
  JointType = 0 (Fixed)
  LengthMax = 0
  LengthMin = 0
  Offset2 = pos=(0,0,0) rot=(0,0,-1;1.5708rad)
  Placement1 = pos=(-34.958,7.753,-0.89184) rot=(0,0,1.00029;1.5708rad)
  Placement2 = pos=(3,28.2001,0.66) rot=(0.707107,0.707107,0;3.14159rad)
  Reference1 = -> Assembly [RAK4631__Solid_.Face663,RAK4631__Solid_.Face663]
  Reference2 = -> Assembly [RAK19003__Solid_.Face5856,RAK19003__Solid_.Face5856]
FEATURE [App::FeaturePython] Joint009  label="onoff_main"  # Assembly joint (typed FeaturePython)
  Activated = true
  AngleMax = 0
  AngleMin = 0
  Detach1 = false
  Detach2 = false
  Distance = 0
  Distance2 = 0
  EnableAngleMax = false
  EnableAngleMin = false
  EnableLengthMax = false
  EnableLengthMin = false
  JointType = 0 (Fixed)
  LengthMax = 0
  LengthMin = 0
  Offset2 = pos=(0,0,0) rot=(0,0,1;1.5708rad)
  Placement1 = pos=(0,0,9.7) rot=(0,1,0;3.14159rad)
  Placement2 = pos=(1.00889,52.6,-9.4) rot=(0.57735,0.57735,0.57735;4.18879rad)
  Reference1 = -> Assembly [on_off_switch.Part__Feature076.Edge648,on_off_switch.Part__Feature076.Edge648]
  Reference2 = -> Assembly [base.Body.Edge221,base.Body.Edge221]
FEATURE [App::FeaturePython] Joint010  label="onoff_cover"  # Assembly joint (typed FeaturePython)
  Activated = true
  AngleMax = 0
  AngleMin = 0
  Detach1 = false
  Detach2 = false
  Distance = 0
  Distance2 = 0
  EnableAngleMax = false
  EnableAngleMin = false
  EnableLengthMax = false
  EnableLengthMin = false
  JointType = 0 (Fixed)
  LengthMax = 0
  LengthMin = 0
  Placement1 = pos=(7.7e-15,-8.509,0) rot=(-0.57735,-0.57735,0.57735;4.18879rad)
  Placement2 = pos=(1.00889,55,-9.4) rot=(0,0.707107,0.707107;3.14159rad)
  Reference1 = -> Assembly [switch_cover.Part__Feature072.Edge179,switch_cover.Part__Feature072.Edge179]
  Reference2 = -> Assembly [base.Body.Edge80,base.Body.Edge80]
FEATURE [App::FeaturePython] Joint011  label="usb_cover_main"  # Assembly joint (typed FeaturePython)
  Activated = true
  AngleMax = 0
  AngleMin = 0
  Detach1 = false
  Detach2 = false
  Distance = 0
  Distance2 = 0
  EnableAngleMax = false
  EnableAngleMin = false
  EnableLengthMax = false
  EnableLengthMin = false
  JointType = 0 (Fixed)
  LengthMax = 0
  LengthMin = 0
  Placement1 = pos=(0,0,0) rot=(0,0,1;3.14159rad)
  Placement2 = pos=(-31,26,-13) rot=(-0.57735,0.57735,0.57735;4.18879rad)
  Reference1 = -> Assembly [usb_cover_base.Body003.Edge10,usb_cover_base.Body003.Edge10]
  Reference2 = -> Assembly [base.Body.Edge223,base.Body.Edge223]
FEATURE [App::Point] Origin140
  Role = Origin
FEATURE [App::Point] Origin142
  Role = Origin
FEATURE [Sketcher::SketchObject] Sketch025
  ArcFitTolerance = 1e-06
  AttachmentSupport = -> [XY_Plane070]
  ExternalTypes = [0]
  FullyConstrained = true
  MakeInternals = false
  MapMode = 5
  expr: Constraints[7] = VarSet.base_width
  expr: Constraints[8] = VarSet.Base_base_lenght
  sketch-geometry (8):
    g0: LineSegment StartX=-32.5 StartY=51 StartZ=0 EndX=-32.5 EndY=0 EndZ=0
    g1: LineSegment StartX=-32.5 StartY=0 StartZ=0 EndX=32.5 EndY=0 EndZ=0
    g2: LineSegment StartX=32.5 StartY=0 StartZ=0 EndX=32.5 EndY=51 EndZ=0
    g3: LineSegment StartX=28.5 StartY=55 StartZ=0 EndX=-28.5 EndY=55 EndZ=0
    g4: ArcOfCircle CenterX=-28.5 CenterY=51 CenterZ=0 NormalX=0 NormalY=0 NormalZ=1 AngleXU=0 Radius=4 StartAngle=1.5708 EndAngle=3.14159
    g5: GeomPoint [constr] X=-32.5 Y=55 Z=0
    g6: ArcOfCircle CenterX=28.5 CenterY=51 CenterZ=0 NormalX=0 NormalY=0 NormalZ=1 AngleXU=0 Radius=4 StartAngle=4.17e-14 EndAngle=1.5708
    g7: GeomPoint [constr] X=32.5 Y=55 Z=0
  constraints (19):
    c: Coincident(g0,g1)
    c: Coincident(g1,g2)
    c: Vertical(g0)
    c: Vertical(g2)
    c: Horizontal(g1)
    c: PointOnObject(g1,g-1)
    c: Symmetric(g5,g7,g-2)
    c: DistanceX(g5,g7) = 65
    c: DistanceY(g1,g7) = 55
    c: PointOnObject(g5,g0)
    c: PointOnObject(g5,g3)
    c: Tangent(g0,g4) = -1.5708
    c: Tangent(g3,g4) = -1.5708
    c: PointOnObject(g7,g2)
    c: PointOnObject(g7,g3)
    c: Tangent(g2,g6) = -1.5708
    c: Tangent(g3,g6) = -1.5708
    c: Equal(g4,g6)
    c: Radius(g4) = 4
FEATURE [PartDesign::SubShapeBinder] Binder001
  BindCopyOnChange = 0
  BindMode = 0
  ClaimChildren = false
  Context = -> Body007 [Binder001.]
  Fuse = false
  MakeFace = true
  OffsetFill = false
  OffsetIntersection = false
  OffsetJoinType = 0
  OffsetOpenResult = false
  PartialLoad = false
  Refine = true
  Relative = true
  Support = -> [Part[Body.Sketch.]]
  _Version = 2
FEATURE [PartDesign::Pad] Pad011
  Direction = (0,0,1)
  Length = 5
  Length2 = 10
  Profile = -> Sketch025
  ReferenceAxis = -> Sketch025 [N_Axis]
  Refine = true
  Suppressed = false
  Type = 0
  expr: Length = VarSet.Base_lid_thickness
FEATURE [Sketcher::SketchObject] Sketch026
  ArcFitTolerance = 1e-06
  AttachmentSupport = -> [Pad011]
  ExternalGeometry = -> [Binder001]
  ExternalTypes = [0,0,0,0]
  FullyConstrained = false
  MakeInternals = false
  MapMode = 5
  Placement = pos=(0,0,5) rot=(0,0,1;0rad)
  sketch-geometry (4):
    g0: Circle CenterX=-28.5 CenterY=51 CenterZ=0 NormalX=0 NormalY=0 NormalZ=1 AngleXU=0 Radius=3.19333
    g1: Circle CenterX=28.5 CenterY=51 CenterZ=0 NormalX=0 NormalY=0 NormalZ=1 AngleXU=0 Radius=3.19333
    g2: Circle CenterX=28.5 CenterY=4 CenterZ=0 NormalX=0 NormalY=0 NormalZ=1 AngleXU=0 Radius=3.19333
    g3: Circle CenterX=-28.5 CenterY=4 CenterZ=0 NormalX=0 NormalY=0 NormalZ=1 AngleXU=0 Radius=3.19333
  constraints (7):
    c: Coincident(g0,g-3)
    c: Coincident(g1,g-4)
    c: Coincident(g2,g-5)
    c: Coincident(g3,g-6)
    c: Equal(g3,g2)
    c: Equal(g2,g1)
    c: Equal(g1,g0)
FEATURE [PartDesign::Hole] Hole
  BaseFeature = -> Pad011
  CustomThreadClearance = 0
  Depth = 25
  DepthType = 0
  Diameter = 3.4
  DrillForDepth = false
  DrillPoint = 1
  DrillPointAngle = 118
  HoleCutCountersinkAngle = 90
  HoleCutCustomValues = false
  HoleCutDepth = 0
  HoleCutDiameter = 6.7
  HoleCutType = 2
  ModelThread = false
  Profile = -> Sketch026
  Refine = true
  Suppressed = false
  Tapered = false
  TaperedAngle = 90
  ThreadClass = 0
  ThreadDepth = 25
  ThreadDepthType = 0
  ThreadDirection = 0
  ThreadFit = 0
  ThreadSize = 9
  ThreadType = 1
  Threaded = false
  UseCustomThreadClearance = false
FEATURE [PartDesign::SubShapeBinder] Binder
  BindCopyOnChange = 0
  BindMode = 0
  ClaimChildren = false
  Context = -> Body001 [Binder.]
  Fuse = false
  MakeFace = true
  OffsetFill = false
  OffsetIntersection = false
  OffsetJoinType = 0
  OffsetOpenResult = false
  PartialLoad = false
  Refine = true
  Relative = true
  Support = -> [Part[Body.Sketch.]]
  _Version = 2
FEATURE [Sketcher::SketchObject] Sketch027  label="center_line"
  ArcFitTolerance = 1e-06
  AttachmentSupport = -> [XY_Plane055]
  ExternalGeometry = -> [Binder]
  ExternalTypes = [0,0,0,0,0,0,0,0,0,0,0,0,0,0,0,0]
  FullyConstrained = true
  MakeInternals = false
  MapMode = 5
FEATURE [App::Point] Origin148
  Role = Origin
FEATURE [App::Point] Origin150
  Role = Origin
FEATURE [App::Point] Origin152
  Role = Origin
FEATURE [Sketcher::SketchObject] Sketch030
  ArcFitTolerance = 1e-06
  AttachmentSupport = -> [XY_Plane075]
  ExternalTypes = [0]
  FullyConstrained = true
  MakeInternals = false
  MapMode = 5
  expr: Constraints[7] = VarSet.base_width
  expr: Constraints[8] = VarSet.Base_battery_lenght
  sketch-geometry (8):
    g0: LineSegment StartX=-32.5 StartY=0 StartZ=0 EndX=32.5 EndY=0 EndZ=0
    g1: LineSegment StartX=32.5 StartY=0 StartZ=0 EndX=32.5 EndY=81 EndZ=0
    g2: LineSegment StartX=28.5 StartY=85 StartZ=0 EndX=-28.5 EndY=85 EndZ=0
    g3: LineSegment StartX=-32.5 StartY=81 StartZ=0 EndX=-32.5 EndY=0 EndZ=0
    g4: ArcOfCircle CenterX=-28.5 CenterY=81 CenterZ=0 NormalX=0 NormalY=0 NormalZ=1 AngleXU=0 Radius=4 StartAngle=1.5708 EndAngle=3.14159
    g5: GeomPoint [constr] X=-32.5 Y=85 Z=0
    g6: ArcOfCircle CenterX=28.5 CenterY=81 CenterZ=0 NormalX=0 NormalY=0 NormalZ=1 AngleXU=0 Radius=4 StartAngle=4.08e-14 EndAngle=1.5708
    g7: GeomPoint [constr] X=32.5 Y=85 Z=0
  constraints (19):
    c: Coincident(g0,g1)
    c: Coincident(g3,g0)
    c: Horizontal(g0)
    c: Vertical(g1)
    c: Vertical(g3)
    c: PointOnObject(g0,g-1)
    c: Symmetric(g5,g7,g-2)
    c: DistanceX(g5,g7) = 65
    c: DistanceY(g0,g7) = 85
    c: PointOnObject(g5,g3)
    c: PointOnObject(g5,g2)
    c: Tangent(g3,g4) = -1.5708
    c: Tangent(g2,g4) = -1.5708
    c: PointOnObject(g7,g2)
    c: PointOnObject(g7,g1)
    c: Tangent(g2,g6) = -1.5708
    c: Tangent(g1,g6) = -1.5708
    c: Equal(g4,g6)
    c: Radius(g4) = 4
FEATURE [PartDesign::SubShapeBinder] Binder003
  BindCopyOnChange = 0
  BindMode = 0
  ClaimChildren = false
  Context = -> Part006 [Body011.Binder003.]
  Fuse = false
  MakeFace = true
  OffsetFill = false
  OffsetIntersection = false
  OffsetJoinType = 0
  OffsetOpenResult = false
  PartialLoad = false
  Refine = true
  Relative = true
  Support = -> [Part002[Body002.Sketch006.]]
  _Version = 2
FEATURE [PartDesign::SubShapeBinder] Binder004
  BindCopyOnChange = 0
  BindMode = 0
  ClaimChildren = false
  Context = -> Part005 [Body010.Binder004.]
  Fuse = false
  MakeFace = true
  OffsetFill = false
  OffsetIntersection = false
  OffsetJoinType = 0
  OffsetOpenResult = false
  PartialLoad = false
  Refine = true
  Relative = true
  Support = -> [Part002[Body002.Sketch006.]]
  _Version = 2
FEATURE [Sketcher::SketchObject] Sketch033
  ArcFitTolerance = 1e-06
  AttachmentSupport = -> [YZ_Plane058]
  ExternalGeometry = -> [Sketch006]
  ExternalTypes = [0]
  FullyConstrained = true
  MakeInternals = false
  MapMode = 5
  Placement = pos=(0,0,0) rot=(0.57735,0.57735,0.57735;2.0944rad)
  expr: Constraints[10] = VarSet.Base_gasket_width
  expr: Constraints[11] = VarSet.Base_gasket_height
  sketch-geometry (5):
    g0: LineSegment StartX=1 StartY=1 StartZ=0 EndX=1 EndY=-1 EndZ=0
    g1: LineSegment StartX=1 StartY=-1 StartZ=0 EndX=2 EndY=-1 EndZ=0
    g2: LineSegment StartX=2 StartY=-1 StartZ=0 EndX=2 EndY=1 EndZ=0
    g3: LineSegment StartX=2 StartY=1 StartZ=0 EndX=1 EndY=1 EndZ=0
    g4: GeomPoint [constr] X=1.5 Y=0 Z=0
  constraints (12):
    c: Coincident(g0,g1)
    c: Coincident(g1,g2)
    c: Coincident(g2,g3)
    c: Coincident(g3,g0)
    c: Vertical(g0)
    c: Vertical(g2)
    c: Horizontal(g1)
    c: Horizontal(g3)
    c: Symmetric(g2,g0,g4)
    c: Coincident(g4,g-3)
    c: DistanceX(g0,g2) = 1
    c: DistanceY(g0,g0) = 2
FEATURE [PartDesign::SubtractivePipe] SubtractivePipe001  label="gasket_"
  AuxilleryCurvelinear = true
  AuxillerySpineTangent = false
  BaseFeature = -> Pocket020
  Binormal = (0,0,0)
  Mode = 0
  Profile = -> Sketch033
  Refine = true
  Spine = -> Sketch006 [Edge21,Edge20,Edge19,Edge34,Edge33,Edge32,Edge31,Edge30,Edge29,Edge28,Edge27,Edge26,Edge25,Edge24,Edge23,Edge22]
  SpineTangent = false
  Suppressed = false
  Transformation = 0
  Transition = 0
FEATURE [Sketcher::SketchObject] Sketch034  label="gasket"
  ArcFitTolerance = 1e-06
  AttachmentSupport = -> [XY_Plane070]
  ExternalGeometry = -> [Binder001]
  ExternalTypes = [0,0,0,0,0,0,0,0,0,0,0,0,0,0,0,0,0]
  FullyConstrained = true
  MakeInternals = false
  MapMode = 5
FEATURE [Sketcher::SketchObject] Sketch035
  ArcFitTolerance = 1e-06
  AttachmentSupport = -> [YZ_Plane070]
  ExternalGeometry = -> [Sketch034]
  ExternalTypes = [0]
  FullyConstrained = true
  MakeInternals = false
  MapMode = 5
  Placement = pos=(0,0,0) rot=(0.57735,0.57735,0.57735;2.0944rad)
  expr: Constraints[10] = VarSet.Base_gasket_width
  expr: Constraints[11] = VarSet.Base_gasket_height
  sketch-geometry (5):
    g0: LineSegment StartX=1 StartY=1 StartZ=0 EndX=1 EndY=-1 EndZ=0
    g1: LineSegment StartX=1 StartY=-1 StartZ=0 EndX=2 EndY=-1 EndZ=0
    g2: LineSegment StartX=2 StartY=-1 StartZ=0 EndX=2 EndY=1 EndZ=0
    g3: LineSegment StartX=2 StartY=1 StartZ=0 EndX=1 EndY=1 EndZ=0
    g4: GeomPoint [constr] X=1.5 Y=0 Z=0
  constraints (12):
    c: Coincident(g0,g1)
    c: Coincident(g1,g2)
    c: Coincident(g2,g3)
    c: Coincident(g3,g0)
    c: Vertical(g0)
    c: Vertical(g2)
    c: Horizontal(g1)
    c: Horizontal(g3)
    c: Symmetric(g2,g0,g4)
    c: Coincident(g4,g-3)
    c: DistanceX(g0,g2) = 1
    c: DistanceY(g0,g0) = 2
FEATURE [PartDesign::SubtractivePipe] SubtractivePipe002
  AuxilleryCurvelinear = true
  AuxillerySpineTangent = false
  BaseFeature = -> Hole
  Binormal = (0,0,0)
  Mode = 0
  Profile = -> Sketch035
  Refine = true
  Spine = -> Sketch034 [Edge13,Edge14,Edge15,Edge16,Edge1,Edge2,Edge3,Edge4,Edge5,Edge6,Edge7,Edge8,Edge9,Edge10,Edge11,Edge12]
  SpineTangent = false
  Suppressed = false
  Transformation = 0
  Transition = 0
FEATURE [PartDesign::Pad] Pad013
  Direction = (0,0,1)
  Length = 5
  Length2 = 10
  Profile = -> Sketch030
  ReferenceAxis = -> Sketch030 [N_Axis]
  Refine = true
  Reversed = true
  Suppressed = false
  Type = 0
  expr: Length = VarSet.Base_lid_thickness
FEATURE [Sketcher::SketchObject] Sketch036
  ArcFitTolerance = 1e-06
  AttachmentSupport = -> [Pad013]
  ExternalGeometry = -> [Binder003]
  ExternalTypes = [0,0,0,0]
  FullyConstrained = true
  MakeInternals = false
  MapMode = 5
  Placement = pos=(0,0,-5) rot=(1,0,0;3.14159rad)
FEATURE [PartDesign::Hole] Hole001
  BaseFeature = -> Pad013
  CustomThreadClearance = 0
  Depth = 25
  DepthType = 0
  Diameter = 3.2
  DrillForDepth = false
  DrillPoint = 1
  DrillPointAngle = 118
  HoleCutCountersinkAngle = 90
  HoleCutCustomValues = false
  HoleCutDepth = 0
  HoleCutDiameter = 6.1
  HoleCutType = 2
  ModelThread = false
  Profile = -> Sketch036
  Refine = true
  Suppressed = false
  Tapered = false
  TaperedAngle = 90
  ThreadClass = 0
  ThreadDepth = 25
  ThreadDepthType = 0
  ThreadDirection = 0
  ThreadFit = 1
  ThreadSize = 9
  ThreadType = 1
  Threaded = false
  UseCustomThreadClearance = false
FEATURE [Sketcher::SketchObject] Sketch037  label="grasket_outside"
  ArcFitTolerance = 1e-06
  AttachmentSupport = -> [XY_Plane075]
  ExternalGeometry = -> [Binder003]
  ExternalTypes = [0,0,0,0,0,0,0,0,0,0,0,0,0,0,0,0,0,0]
  FullyConstrained = true
  MakeInternals = false
  MapMode = 5
FEATURE [Sketcher::SketchObject] Sketch038
  ArcFitTolerance = 1e-06
  AttachmentSupport = -> [YZ_Plane075]
  ExternalGeometry = -> [Binder003]
  ExternalTypes = [0]
  FullyConstrained = true
  MakeInternals = false
  MapMode = 5
  Placement = pos=(0,0,0) rot=(0.57735,0.57735,0.57735;2.0944rad)
  expr: Constraints[10] = VarSet.Base_gasket_width
  expr: Constraints[11] = VarSet.Base_gasket_height
  sketch-geometry (5):
    g0: LineSegment StartX=1 StartY=1 StartZ=0 EndX=1 EndY=-1 EndZ=0
    g1: LineSegment StartX=1 StartY=-1 StartZ=0 EndX=2 EndY=-1 EndZ=0
    g2: LineSegment StartX=2 StartY=-1 StartZ=0 EndX=2 EndY=1 EndZ=0
    g3: LineSegment StartX=2 StartY=1 StartZ=0 EndX=1 EndY=1 EndZ=0
    g4: GeomPoint [constr] X=1.5 Y=0 Z=0
  constraints (12):
    c: Coincident(g0,g1)
    c: Coincident(g1,g2)
    c: Coincident(g2,g3)
    c: Coincident(g3,g0)
    c: Vertical(g0)
    c: Vertical(g2)
    c: Horizontal(g1)
    c: Horizontal(g3)
    c: Symmetric(g2,g0,g4)
    c: Coincident(g4,g-3)
    c: DistanceX(g0,g2) = 1
    c: DistanceY(g0,g0) = 2
FEATURE [Sketcher::SketchObject] Sketch039
  ArcFitTolerance = 1e-06
  AttachmentSupport = -> [XY_Plane075]
  ExternalGeometry = -> [Binder003]
  ExternalTypes = [0,0,0,0,0,0,0,0]
  FullyConstrained = true
  MakeInternals = false
  MapMode = 5
FEATURE [Sketcher::SketchObject] Sketch040  label="line"
  ArcFitTolerance = 1e-06
  AttachmentSupport = -> [XY_Plane073]
  ExternalGeometry = -> [Binder004]
  ExternalTypes = [0,0,0,0,0,0,0,0,0,0,0,0,0,0,0,0]
  FullyConstrained = true
  MakeInternals = false
  MapMode = 5
FEATURE [App::Link] gasket_main_body001  label="gasket_main_body003"
  LinkPlacement = pos=(2.7e-15,-1.42e-14,1.78e-14) rot=(0,0,1;0rad)
  LinkedObject = -> Body001
  Placement = pos=(2.7e-15,-1.42e-14,1.78e-14) rot=(0,0,1;0rad)
FEATURE [App::Link] battery_cover  label="battery_cover002"
  LinkPlacement = pos=(0.216708,-33.5,0.15511) rot=(1,0,0;3.14159rad)
  LinkedObject = -> Part006
  Placement = pos=(0.216708,-33.5,0.15511) rot=(1,0,0;3.14159rad)
FEATURE [App::Link] battery_cover_gasket  label="battery_cover_gasket002"
  LinkPlacement = pos=(0.216708,-33.5,0.15511) rot=(0,0,1;3.14159rad)
  LinkedObject = -> Part005
  Placement = pos=(0.216708,-33.5,0.15511) rot=(0,0,1;3.14159rad)
FEATURE [Part::Feature] Part__Feature084  label="Magnetic Pogo Connector 3 Pin (Type 2)"
  shape: bbox 15 x 4 x 4 mm, 35 faces (baked)
FEATURE [App::Part] Magnetic_Pogo_Connector_3_Pin__Type_2_  label="Magnetic Pogo Connector 3 Pin (Type 2)006"
  Group = -> [Part__Feature084,Part__Feature085,Part__Feature086,Part__Feature087,Part__Feature088,Part__Feature089]
  Origin = -> Origin137
  Placement = pos=(0,20,-3.9e-15) rot=(1,0,0;3.14159rad)
FEATURE [Part::Feature] PCB_solid002  label="RAK12500_GPS (Solid)"
  shape: bbox 10.15 x 23.15 x 2.906 mm, 2590 faces (baked)
FEATURE [App::Point] Origin154
  Role = Origin
FEATURE [App::Point] Origin156
  Role = Origin
FEATURE [Sketcher::SketchObject] Sketch042
  ArcFitTolerance = 1e-06
  AttachmentSupport = -> [XY_Plane077]
  ExternalTypes = [0]
  FullyConstrained = true
  MakeInternals = false
  MapMode = 5
  expr: Constraints[10] = VarSet.Base_gps_antenna_width
  expr: Constraints[11] = VarSet.Base_gps_antenna_lenght
  sketch-geometry (15):
    g0: LineSegment StartX=-7.5 StartY=7.5 StartZ=0 EndX=-7.5 EndY=-7.5 EndZ=0
    g1: LineSegment StartX=-7.5 StartY=-7.5 StartZ=0 EndX=7.5 EndY=-7.5 EndZ=0
    g2: LineSegment StartX=7.5 StartY=-7.5 StartZ=0 EndX=7.5 EndY=7.5 EndZ=0
    g3: LineSegment StartX=7.5 StartY=7.5 StartZ=0 EndX=-7.5 EndY=7.5 EndZ=0
    g4: GeomPoint [constr] X=0 Y=0 Z=0
    g5: LineSegment StartX=-6.5 StartY=-6.5 StartZ=0 EndX=6.5 EndY=-6.5 EndZ=0
    g6: LineSegment StartX=6.5 StartY=-6.5 StartZ=0 EndX=6.5 EndY=6.5 EndZ=0
    g7: LineSegment StartX=6.5 StartY=6.5 StartZ=0 EndX=-6.5 EndY=6.5 EndZ=0
    g8: LineSegment StartX=-6.5 StartY=6.5 StartZ=0 EndX=-6.5 EndY=-6.5 EndZ=0
    g9: GeomPoint [constr] X=0 Y=0 Z=0
    g10: LineSegment StartX=-6 StartY=-6 StartZ=0 EndX=6 EndY=-6 EndZ=0
    g11: LineSegment StartX=6 StartY=-6 StartZ=0 EndX=6 EndY=6 EndZ=0
    g12: LineSegment StartX=6 StartY=6 StartZ=0 EndX=-6 EndY=6 EndZ=0
    g13: LineSegment StartX=-6 StartY=6 StartZ=0 EndX=-6 EndY=-6 EndZ=0
    g14: GeomPoint [constr] X=0 Y=0 Z=0
  constraints (36):
    c: Coincident(g0,g1)
    c: Coincident(g1,g2)
    c: Coincident(g2,g3)
    c: Coincident(g3,g0)
    c: Vertical(g0)
    c: Vertical(g2)
    c: Horizontal(g1)
    c: Horizontal(g3)
    c: Symmetric(g2,g0,g4)
    c: Coincident(g4,g-1)
    c: DistanceX(g0,g2) = 15
    c: DistanceY(g0,g0) = 15
    c: Coincident(g5,g6)
    c: Coincident(g6,g7)
    c: Coincident(g7,g8)
    c: Coincident(g8,g5)
    c: Horizontal(g5)
    c: Horizontal(g7)
    c: Vertical(g6)
    c: Vertical(g8)
    c: Symmetric(g7,g5,g9)
    c: Distance(g6,g8) = 13
    c: Distance(g5,g7) = 13
    c: Coincident(g9,g4)
    c: Coincident(g10,g11)
    c: Coincident(g11,g12)
    c: Coincident(g12,g13)
    c: Coincident(g13,g10)
    c: Horizontal(g10)
    c: Horizontal(g12)
    c: Vertical(g11)
    c: Vertical(g13)
    c: Symmetric(g12,g10,g14)
    c: Distance(g11,g13) = 12
    c: Distance(g10,g12) = 12
    c: Coincident(g14,g4)
FEATURE [App::FeaturePython] Joint016  label="battery_cover003"  # Assembly joint (typed FeaturePython)
  Activated = true
  AngleMax = 0
  AngleMin = 0
  Detach1 = false
  Detach2 = false
  Distance = 0
  Distance2 = 0
  EnableAngleMax = false
  EnableAngleMin = false
  EnableLengthMax = false
  EnableLengthMin = false
  JointType = 0 (Fixed)
  LengthMax = 0
  LengthMin = 0
  Offset2 = pos=(0,0,0) rot=(0,0,1;3.14159rad)
  Placement1 = pos=(8.9e-15,1,-1) rot=(-0.707107,0,0.707107;3.14159rad)
  Placement2 = pos=(1.24e-14,1,1) rot=(0,1,0;4.71239rad)
  Reference1 = -> Assembly [battery_cover.Body011.Edge112,battery_cover.Body011.Edge112]
  Reference2 = -> Assembly [battery_cover_gasket.Body010.Edge1,battery_cover_gasket.Body010.Edge1]
FEATURE [Sketcher::SketchObject] Sketch043  label="cut_for_better_connection"
  ArcFitTolerance = 1e-06
  AttachmentSupport = -> [XZ_Plane065]
  ExternalTypes = [0]
  FullyConstrained = true
  MakeInternals = false
  MapMode = 5
  Placement = pos=(0,0,0) rot=(1,0,0;1.5708rad)
  expr: Constraints[10] = 2 * VarSet.Base_connector_bounting_box_height
  expr: Constraints[12] = VarSet.case_height / 2
  expr: Constraints[9] = VarSet.Base_connector_internal_lug + 10 * VarSet.Base_connector_lug_offset
  sketch-geometry (6):
    g0: LineSegment StartX=-6.5 StartY=9.5 StartZ=0 EndX=-6.5 EndY=-34.5 EndZ=0
    g1: LineSegment StartX=-6.5 StartY=-34.5 StartZ=0 EndX=6.5 EndY=-34.5 EndZ=0
    g2: LineSegment StartX=6.5 StartY=-34.5 StartZ=0 EndX=6.5 EndY=9.5 EndZ=0
    g3: LineSegment StartX=6.5 StartY=9.5 StartZ=0 EndX=-6.5 EndY=9.5 EndZ=0
    g4: GeomPoint [constr] X=0 Y=-12.5 Z=0
    g5: GeomPoint X=0 Y=-12.5 Z=0
  constraints (14):
    c: Coincident(g0,g1)
    c: Coincident(g1,g2)
    c: Coincident(g2,g3)
    c: Coincident(g3,g0)
    c: Vertical(g0)
    c: Vertical(g2)
    c: Horizontal(g1)
    c: Horizontal(g3)
    c: Symmetric(g2,g0,g4)
    c: DistanceX(g0,g2) = 13
    c: DistanceY(g0,g0) = 44
    c: PointOnObject(g5,g-2)
    c: DistanceY(g5,g-1) = 12.5
    c: Coincident(g4,g5)
FEATURE [PartDesign::Pocket] Pocket027
  BaseFeature = -> Pocket016
  Direction = (0,1,-2e-16)
  Length = 12
  Length2 = 5
  Placement = pos=(0,0,0) rot=(1,0,0;1.5708rad)
  Profile = -> Sketch043
  ReferenceAxis = -> Sketch043 [N_Axis]
  Refine = true
  Reversed = true
  Suppressed = false
  Type = 0
  expr: Length = VarSet.Base_connector_height_lug
FEATURE [PartDesign::Fillet] Fillet
  Base = -> Pocket024 [Edge5,Edge60]
  BaseFeature = -> Pocket024
  Placement = pos=(0,0,0) rot=(1,0,0;1.5708rad)
  Radius = 10
  Refine = true
  SupportTransform = false
  Suppressed = false
  UseAllEdges = false
FEATURE [PartDesign::Pad] Pad015
  Direction = (0,0,1)
  Length = 0.6
  Length2 = 10
  Profile = -> Sketch042 [Edge4,Edge3,Edge2,Edge1]
  ReferenceAxis = -> Sketch042 [N_Axis]
  Refine = true
  Suppressed = false
  Type = 0
FEATURE [PartDesign::Pad] Pad016
  BaseFeature = -> Pad015
  Direction = (0,0,1)
  Length = 5
  Length2 = 10
  Profile = -> Sketch042 [Edge5,Edge8,Edge7,Edge6]
  ReferenceAxis = -> Sketch042 [N_Axis]
  Refine = true
  Suppressed = false
  Type = 0
FEATURE [PartDesign::Pad] Pad017
  BaseFeature = -> Pad016
  Direction = (0,0,1)
  Length = 1.3
  Length2 = 10
  Profile = -> Sketch042 [Edge12,Edge9,Edge10,Edge11]
  ReferenceAxis = -> Sketch042 [N_Axis]
  Refine = true
  Reversed = true
  Suppressed = false
  Type = 0
FEATURE [Sketcher::SketchObject] Sketch044
  ArcFitTolerance = 1e-06
  ExternalTypes = [0]
  FullyConstrained = true
  MakeInternals = false
  MapMode = 5
  Placement = pos=(0,0,5) rot=(0,0,1;0rad)
  sketch-geometry (1):
    g0: Circle CenterX=0 CenterY=1.5 CenterZ=0 NormalX=0 NormalY=0 NormalZ=1 AngleXU=0 Radius=1
  constraints (3):
    c: PointOnObject(g0,g-2)
    c: Diameter(g0) = 2
    c: DistanceY(g-1,g0) = 1.5
FEATURE [PartDesign::Pad] Pad018
  BaseFeature = -> Pad017
  Direction = (0,0,1)
  Length = 1
  Length2 = 10
  Profile = -> Sketch044
  ReferenceAxis = -> Sketch044 [N_Axis]
  Refine = true
  Suppressed = false
  Type = 0
FEATURE [PartDesign::Chamfer] Chamfer
  Angle = 45
  Base = -> Pad018 [Edge21,Edge24,Edge26,Vertex18,Edge22]
  BaseFeature = -> Pad018
  ChamferType = 0
  FlipDirection = false
  Refine = true
  Size = 2
  Size2 = 1
  SupportTransform = false
  Suppressed = false
  UseAllEdges = false
FEATURE [Sketcher::SketchObject] Sketch045
  ArcFitTolerance = 1e-06
  AttachmentSupport = -> [Chamfer]
  ExternalTypes = [0]
  FullyConstrained = true
  MakeInternals = false
  MapMode = 5
  Placement = pos=(0,6,0) rot=(0,0.707107,0.707107;3.14159rad)
  sketch-geometry (1):
    g0: Circle CenterX=0 CenterY=-0.7 CenterZ=0 NormalX=0 NormalY=0 NormalZ=1 AngleXU=0 Radius=0.5
  constraints (3):
    c: PointOnObject(g0,g-2)
    c: Diameter(g0) = 1
    c: Distance(g0,g-1) = 0.7
FEATURE [PartDesign::Pad] Pad019
  BaseFeature = -> Chamfer
  Direction = (0,1,-2e-16)
  Length = 5
  Length2 = 10
  Profile = -> Sketch045
  ReferenceAxis = -> Sketch045 [N_Axis]
  Refine = true
  Suppressed = false
  Type = 0
FEATURE [PartDesign::Body] Body012  label="gps_antenna001"
  AllowCompound = false
  Group = -> [Sketch042,Pad015,Pad016,Pad017,Sketch044,Pad018,Chamfer,Sketch045,Pad019]
  Origin = -> Origin155
  Tip = -> Pad019
FEATURE [App::Part] Part007  label="gps_antenna"
  Group = -> [Body012]
  Origin = -> Origin153
FEATURE [App::Link] gps_antenna  label="gps_antenna002"
  LinkPlacement = pos=(-16,46,-13.5) rot=(0,0.707107,0.707107;3.14159rad)
  LinkedObject = -> Part007
  Placement = pos=(-16,46,-13.5) rot=(0,0.707107,0.707107;3.14159rad)
FEATURE [App::FeaturePython] Joint007  label="sma_main"  # Assembly joint (typed FeaturePython)
  Activated = true
  AngleMax = 0
  AngleMin = 0
  Detach1 = false
  Detach2 = false
  Distance = 0
  Distance2 = 0
  EnableAngleMax = false
  EnableAngleMin = false
  EnableLengthMax = false
  EnableLengthMin = false
  JointType = 0 (Fixed)
  LengthMax = 0
  LengthMin = 0
  Placement1 = pos=(3.6e-15,-3.6e-15,-11.43) rot=(-0.707107,0.707107,0;3.14159rad)
  Placement2 = pos=(17,52.6,-16) rot=(0,0.707107,0.707107;3.14159rad)
  Reference1 = -> Assembly [_053072_1.Edge309,_053072_1.Edge309]
  Reference2 = -> Assembly [base.Body.Edge219,base.Body.Edge219]
FEATURE [App::FeaturePython] Joint008  label="sma_anttenna"  # Assembly joint (typed FeaturePython)
  Activated = true
  AngleMax = 0
  AngleMin = 0
  Detach1 = false
  Detach2 = false
  Distance = 0
  Distance2 = 0
  EnableAngleMax = false
  EnableAngleMin = false
  EnableLengthMax = false
  EnableLengthMin = false
  JointType = 0 (Fixed)
  LengthMax = 0
  LengthMin = 0
  Placement1 = pos=(-6e-16,22.4,5) rot=(-1,0,0;1.5708rad)
  Placement2 = pos=(0,0,0) rot=(-0.707107,0.707107,0;3.14159rad)
  Reference1 = -> Assembly [antenna_WiFi_RP_SMA_conn_v003.Part__Feature067.Face549,antenna_WiFi_RP_SMA_conn_v003.Part__Feature067.Face549]
  Reference2 = -> Assembly [_053072_1.Face35,_053072_1.Face35]
FEATURE [App::Link] _053072_1  label="sma001"
  LinkPlacement = pos=(17,64.03,-16) rot=(-0.57735,-0.57735,-0.57735;2.0944rad)
  LinkedObject = -> Part__Feature070
  Placement = pos=(17,64.03,-16) rot=(-0.57735,-0.57735,-0.57735;2.0944rad)
FEATURE [App::DocumentObjectGroup] Group001  label="Group"
  Group = -> [Magnetic_Pogo_Connector_3_Pin__Type_2_006,Magnetic_Pogo_Connector_3_Pin__Type_1_006,_8650_v002,RAK4631__Solid_,_8650_v1,_053072_1,RAK19003__Solid_,antenna_WiFi_RP_SMA_conn_v003,on_off_switch,switch_cover,gps_antenna]
FEATURE [Sketcher::SketchObject] Sketch  label="main_diamention"
  ArcFitTolerance = 1e-06
  AttachmentSupport = -> [XY_Plane053]
  ExternalTypes = [0]
  FullyConstrained = true
  MakeInternals = false
  MapMode = 5
  expr: Constraints[13] = VarSet.base_width
  expr: Constraints[14] = VarSet.Base_base_lenght
  expr: Constraints[30] = VarSet.Base_m3_insert
  expr: Constraints[45] = VarSet.Base_case_thickness
  expr: Constraints[46] = VarSet.Base_case_thickness
  expr: Constraints[47] = VarSet.Base_case_thickness
  expr: Constraints[50] = VarSet.Base_case_thickness + VarSet.Base_m3_insert / 2
  expr: Constraints[51] = VarSet.Base_case_thickness + VarSet.Base_m3_insert / 2
  expr: Constraints[52] = VarSet.Base_case_thickness + VarSet.Base_m3_insert / 2
  expr: Constraints[71] = VarSet.Base_case_thickness / 2
  expr: Constraints[72] = VarSet.Base_case_thickness / 2
  expr: Constraints[73] = VarSet.Base_case_thickness / 2
  expr: Constraints[84] = VarSet.Base_case_thickness / 2
  expr: Constraints[86] = VarSet.Base_case_thickness + VarSet.Base_m3_insert / 2
  expr: Constraints[92] = VarSet.Base_case_thickness
  sketch-geometry (40):
    g0: LineSegment StartX=-32.5 StartY=0 StartZ=0 EndX=32.5 EndY=0 EndZ=0
    g1: LineSegment StartX=32.5 StartY=0 StartZ=0 EndX=32.5 EndY=51 EndZ=0
    g2: LineSegment StartX=28.5 StartY=55 StartZ=0 EndX=-28.5 EndY=55 EndZ=0
    g3: LineSegment StartX=-32.5 StartY=51 StartZ=0 EndX=-32.5 EndY=0 EndZ=0
    g4: GeomPoint [constr] X=-32.5 Y=55 Z=0
    g5: ArcOfCircle CenterX=28.5 CenterY=51 CenterZ=0 NormalX=0 NormalY=0 NormalZ=1 AngleXU=0 Radius=4 StartAngle=0 EndAngle=1.5708
    g6: GeomPoint [constr] X=32.5 Y=55 Z=0
    g7: Circle CenterX=-28.5 CenterY=4 CenterZ=0 NormalX=0 NormalY=0 NormalZ=1 AngleXU=0 Radius=1.6
    g8: Circle CenterX=28.5 CenterY=4 CenterZ=0 NormalX=0 NormalY=0 NormalZ=1 AngleXU=0 Radius=1.6
    g9: Circle CenterX=28.5 CenterY=51 CenterZ=0 NormalX=0 NormalY=0 NormalZ=1 AngleXU=0 Radius=1.6
    g10: Circle CenterX=-28.5 CenterY=51 CenterZ=0 NormalX=0 NormalY=0 NormalZ=1 AngleXU=0 Radius=1.6
    g11: LineSegment [constr] StartX=-28.5 StartY=51 StartZ=0 EndX=-28.5 EndY=4 EndZ=0
    g12: LineSegment [constr] StartX=-28.5 StartY=4 StartZ=0 EndX=28.5 EndY=4 EndZ=0
    g13: LineSegment [constr] StartX=28.5 StartY=4 StartZ=0 EndX=28.5 EndY=51 EndZ=0
    g14: LineSegment [constr] StartX=28.5 StartY=51 StartZ=0 EndX=-28.5 EndY=51 EndZ=0
    g15: LineSegment StartX=-24.01 StartY=52 StartZ=0 EndX=24.01 EndY=52 EndZ=0
    g16: LineSegment StartX=29.5 StartY=46.51 StartZ=0 EndX=29.5 EndY=8.48999 EndZ=0
    g17: LineSegment StartX=24.01 StartY=3 StartZ=0 EndX=-24.01 EndY=3 EndZ=0
    g18: LineSegment StartX=-29.5 StartY=8.48999 StartZ=0 EndX=-29.5 EndY=46.51 EndZ=0
    g19: ArcOfCircle CenterX=-28.5 CenterY=4 CenterZ=0 NormalX=0 NormalY=0 NormalZ=1 AngleXU=0 Radius=4.6 StartAngle=6.06404 EndAngle=8.07312
    g20: ArcOfCircle CenterX=-28.5 CenterY=51 CenterZ=0 NormalX=0 NormalY=0 NormalZ=1 AngleXU=0 Radius=4.6 StartAngle=4.49325 EndAngle=6.50233
    g21: ArcOfCircle CenterX=28.5 CenterY=51 CenterZ=0 NormalX=0 NormalY=0 NormalZ=1 AngleXU=0 Radius=4.6 StartAngle=2.92245 EndAngle=4.93153
    g22: ArcOfCircle CenterX=28.5 CenterY=4 CenterZ=0 NormalX=0 NormalY=0 NormalZ=1 AngleXU=0 Radius=4.6 StartAngle=1.35166 EndAngle=3.36073
    g23: ArcOfCircle CenterX=28.5 CenterY=4 CenterZ=0 NormalX=0 NormalY=0 NormalZ=1 AngleXU=0 Radius=3.1 StartAngle=1.35166 EndAngle=3.36073
    g24: ArcOfCircle CenterX=24.01 CenterY=3 CenterZ=0 NormalX=0 NormalY=0 NormalZ=1 AngleXU=-3.14159 Radius=1.5 StartAngle=1.5708 EndAngle=3.36073
    g25: LineSegment StartX=24.01 StartY=1.5 StartZ=0 EndX=-24.01 EndY=1.5 EndZ=0
    g26: ArcOfCircle CenterX=-24.01 CenterY=3 CenterZ=0 NormalX=0 NormalY=0 NormalZ=1 AngleXU=1.55119 Radius=1.5 StartAngle=1.37126 EndAngle=3.1612
    g27: ArcOfCircle CenterX=-28.5 CenterY=4 CenterZ=0 NormalX=0 NormalY=0 NormalZ=1 AngleXU=0 Radius=3.1 StartAngle=6.06404 EndAngle=8.07312
    g28: ArcOfCircle CenterX=-29.5 CenterY=8.48999 CenterZ=0 NormalX=0 NormalY=0 NormalZ=1 AngleXU=1.5708 Radius=1.5 StartAngle=1.5708 EndAngle=3.36073
    g29: LineSegment StartX=-31 StartY=8.48999 StartZ=0 EndX=-31 EndY=46.51 EndZ=0
    g30: ArcOfCircle CenterX=-29.5 CenterY=46.51 CenterZ=0 NormalX=0 NormalY=0 NormalZ=1 AngleXU=-0.0196091 Radius=1.5 StartAngle=1.37126 EndAngle=3.1612
    g31: ArcOfCircle CenterX=-28.5 CenterY=51 CenterZ=0 NormalX=0 NormalY=0 NormalZ=1 AngleXU=0 Radius=3.1 StartAngle=4.49325 EndAngle=6.50233
    g32: ArcOfCircle CenterX=-24.01 CenterY=52 CenterZ=0 NormalX=0 NormalY=0 NormalZ=1 AngleXU=0 Radius=1.5 StartAngle=1.5708 EndAngle=3.36073
    g33: LineSegment StartX=-24.01 StartY=53.5 StartZ=0 EndX=24.01 EndY=53.5 EndZ=0
    g34: ArcOfCircle CenterX=24.01 CenterY=52 CenterZ=0 NormalX=0 NormalY=0 NormalZ=1 AngleXU=-1.5708 Radius=1.5 StartAngle=1.35166 EndAngle=3.14159
    g35: ArcOfCircle CenterX=28.5 CenterY=51 CenterZ=0 NormalX=0 NormalY=0 NormalZ=1 AngleXU=0 Radius=3.1 StartAngle=2.92245 EndAngle=4.93153
    g36: ArcOfCircle CenterX=29.5 CenterY=46.51 CenterZ=0 NormalX=0 NormalY=0 NormalZ=1 AngleXU=-1.5708 Radius=1.5 StartAngle=1.5708 EndAngle=3.36073
    g37: LineSegment StartX=31 StartY=46.51 StartZ=0 EndX=31 EndY=8.48999 EndZ=0
    g38: ArcOfCircle CenterX=29.5 CenterY=8.48999 CenterZ=0 NormalX=0 NormalY=0 NormalZ=1 AngleXU=3.12198 Radius=1.5 StartAngle=1.37126 EndAngle=3.1612
    g39: ArcOfCircle CenterX=-28.5 CenterY=51 CenterZ=0 NormalX=0 NormalY=0 NormalZ=1 AngleXU=0 Radius=4 StartAngle=1.5708 EndAngle=3.14159
  constraints (94):
    c: Coincident(g0,g1)
    c: Coincident(g3,g0)
    c: Horizontal(g2)
    c: Vertical(g1)
    c: Vertical(g3)
    c: PointOnObject(g0,g-1)
    c: Symmetric(g0,g0,g-2)
    c: PointOnObject(g4,g3)
    c: PointOnObject(g4,g2)
    c: PointOnObject(g6,g1)
    c: PointOnObject(g6,g2)
    c: Tangent(g1,g5) = -1.5708
    c: Tangent(g2,g5) = -1.5708
    c: DistanceX(g4,g6) = 65
    c: DistanceY(g0,g4) = 55
    c: Coincident(g11,g12)
    c: Coincident(g12,g13)
    c: Coincident(g13,g14)
    c: Coincident(g14,g11)
    c: Vertical(g11)
    c: Vertical(g13)
    c: Horizontal(g12)
    c: Coincident(g11,g10)
    c: Coincident(g12,g8)
    c: Coincident(g7,g11)
    c: Coincident(g13,g9)
    c: Symmetric(g10,g9,g-2)
    c: Equal(g10,g9)
    c: Equal(g9,g8)
    c: Equal(g8,g7)
    c: Diameter(g10) = 3.2
    c: Distance(g10,g2) = 2.4
    c: Distance(g7,g0) = 2.4
    c: Horizontal(g15)
    c: Vertical(g16)
    c: Horizontal(g17)
    c: Vertical(g18)
    c: Coincident(g19,g18)
    c: Coincident(g19,g17)
    c: Coincident(g20,g18)
    c: Coincident(g20,g15)
    c: Coincident(g21,g15)
    c: Coincident(g21,g16)
    c: Coincident(g22,g16)
    c: Coincident(g22,g17)
    c: Distance(g2,g15) = 3
    c: Distance(g17,g0) = 3
    c: Distance(g1,g16) = 3
    c: Coincident(g22,g8)
    c: Coincident(g19,g7)
    c: Radius(g19) = 4.6
    c: Radius(g20) = 4.6
    c: Radius(g21) = 4.6
    c: Coincident(g10,g20)
    c: Coincident(g21,g5)
    c: Tangent(g23,g24) = 1.5708
    c: Tangent(g23,g38) = 1.5708
    c: Tangent(g24,g25) = 1.5708
    c: Tangent(g25,g26) = 1.5708
    c: Tangent(g26,g27) = 1.5708
    c: Tangent(g27,g28) = 1.5708
    c: Tangent(g28,g29) = 1.5708
    c: Tangent(g29,g30) = 1.5708
    c: Tangent(g30,g31) = 1.5708
    c: Tangent(g31,g32) = 1.5708
    c: Tangent(g32,g33) = 1.5708
    c: Tangent(g33,g34) = 1.5708
    c: Tangent(g34,g35) = 1.5708
    c: Tangent(g35,g36) = 1.5708
    c: Tangent(g36,g37) = 1.5708
    c: Tangent(g37,g38) = 1.5708
    c: Distance(g17,g25) = 1.5
    c: Distance(g37,g16) = 1.5
    c: Distance(g33,g15) = 1.5
    c: Coincident(g32,g15)
    c: Coincident(g30,g18)
    c: Coincident(g36,g16)
    c: Coincident(g24,g17)
    c: Coincident(g26,g17)
    c: Coincident(g28,g18)
    c: Coincident(g27,g7)
    c: Coincident(g23,g8)
    c: Coincident(g9,g35)
    c: Coincident(g34,g15)
    c: Distance(g27,g19) = 1.5
    c: Coincident(g38,g16)
    c: Radius(g22) = 4.6
    c: Coincident(g39,g10)
    c: Coincident(g39,g3)
    c: Tangent(g39,g2) = -1.5708
    c: Coincident(g31,g10)
    c: Coincident(g5,g9)
    c: Distance(g18,g3) = 3
    c: Distance(g7,g3) = 4
FEATURE [PartDesign::Pad] Pad
  Direction = (0,0,1)
  Length = 25
  Length2 = 10
  Profile = -> Sketch [Edge1,Edge6,Edge5,Edge4,Edge3,Edge2]
  ReferenceAxis = -> Sketch [N_Axis]
  Refine = true
  Reversed = true
  Suppressed = false
  Type = 0
  expr: Length = VarSet.case_height
FEATURE [PartDesign::Pocket] Pocket  label="body_inside"
  BaseFeature = -> Pad
  Direction = (0,0,-1)
  Length = 22
  Length2 = 5
  Profile = -> Sketch [Edge15,Edge16,Edge17,Edge18,Edge11,Edge12,Edge13,Edge14]
  ReferenceAxis = -> Sketch [N_Axis]
  Refine = true
  Suppressed = false
  Type = 0
  expr: Length = VarSet.case_height - VarSet.Base_case_thickness
FEATURE [PartDesign::Pocket] Pocket001  label="screw"
  BaseFeature = -> Pocket
  Direction = (0,0,-1)
  Length = 5
  Length2 = 5
  Midplane = true
  Profile = -> Sketch [Edge10,Edge9,Edge8,Edge7]
  ReferenceAxis = -> Sketch [N_Axis]
  Refine = true
  Suppressed = false
  Type = 1
FEATURE [Sketcher::SketchObject] Sketch003  label="pcb_standoff001"
  ArcFitTolerance = 1e-06
  AttachmentSupport = -> [Pocket001]
  ExternalGeometry = -> [Sketch]
  ExternalTypes = [0,0,0,0]
  FullyConstrained = true
  MakeInternals = false
  MapMode = 5
  Placement = pos=(0,0,-22) rot=(0,0,1;0rad)
  sketch-geometry (10):
    g0: Circle CenterX=-23.5 CenterY=35 CenterZ=0 NormalX=0 NormalY=0 NormalZ=1 AngleXU=0 Radius=2.5
    g1: Circle CenterX=-23.5 CenterY=35 CenterZ=0 NormalX=0 NormalY=0 NormalZ=1 AngleXU=0 Radius=1.3
    g2: Circle CenterX=-23.5 CenterY=13 CenterZ=0 NormalX=0 NormalY=0 NormalZ=1 AngleXU=0 Radius=1.3
    g3: Circle CenterX=-23.5 CenterY=13 CenterZ=0 NormalX=0 NormalY=0 NormalZ=1 AngleXU=0 Radius=2.5
    g4: Circle CenterX=7.5 CenterY=24 CenterZ=0 NormalX=0 NormalY=0 NormalZ=1 AngleXU=0 Radius=3
    g5: Circle CenterX=7.5 CenterY=24 CenterZ=0 NormalX=0 NormalY=0 NormalZ=1 AngleXU=0 Radius=1.3
    g6: LineSegment [constr] StartX=-23.5 StartY=35 StartZ=0 EndX=-23.5 EndY=13 EndZ=0
    g7: LineSegment [constr] StartX=-23.5 StartY=13 StartZ=0 EndX=7.5 EndY=13 EndZ=0
    g8: LineSegment [constr] StartX=7.5 StartY=13 StartZ=0 EndX=7.5 EndY=35 EndZ=0
    g9: LineSegment [constr] StartX=7.5 StartY=35 StartZ=0 EndX=-23.5 EndY=35 EndZ=0
  constraints (25):
    c: Coincident(g1,g0)
    c: Coincident(g3,g2)
    c: Coincident(g5,g4)
    c: Equal(g2,g1)
    c: Equal(g1,g5)
    c: Diameter(g1) = 2.6
    c: Equal(g3,g0)
    c: Diameter(g0) = 5
    c: Diameter(g4) = 6
    c: Coincident(g6,g7)
    c: Coincident(g7,g8)
    c: Coincident(g8,g9)
    c: Coincident(g9,g6)
    c: Vertical(g6)
    c: Vertical(g8)
    c: Horizontal(g7)
    c: Horizontal(g9)
    c: Coincident(g2,g6)
    c: Coincident(g0,g6)
    c: Symmetric(g7,g8,g4)
    c: DistanceY(g2,g0) = 22
    c: DistanceX(g2,g7) = 31
    c: Distance(g2,g-5) = 6
    c: Distance(g-3,g-3) = 48.02
    c: DistanceY(g-4,g2) = 10
FEATURE [PartDesign::Pad] Pad002  label="pcb_standoff"
  BaseFeature = -> Pocket001
  Direction = (0,0,1)
  Length = 4
  Length2 = 10
  Profile = -> Sketch003 [Edge1,Edge5,Edge4]
  ReferenceAxis = -> Sketch003 [N_Axis]
  Refine = true
  Suppressed = false
  Type = 0
FEATURE [PartDesign::Pocket] Pocket002  label="pcb_standoff_pocket"
  BaseFeature = -> Pad002
  Direction = (0,0,-1)
  Length = 5
  Length2 = 5
  Profile = -> Sketch003 [Edge3,Edge2,Edge6]
  ReferenceAxis = -> Sketch003 [N_Axis]
  Refine = true
  Reversed = true
  Suppressed = false
  Type = 1
FEATURE [Sketcher::SketchObject] Sketch004  label="usb_cap"
  ArcFitTolerance = 1e-06
  AttachmentSupport = -> [Pocket002]
  ExternalGeometry = -> [Pocket002]
  ExternalTypes = [0,0]
  FullyConstrained = true
  MakeInternals = false
  MapMode = 5
  Placement = pos=(-32.5,0,0) rot=(0.57735,-0.57735,-0.57735;2.0944rad)
  expr: Constraints[0] = VarSet.Base_usb_cover_main_diameter * 1.2
  expr: Constraints[4] = VarSet.Base_usb_cover_main_diameter
  sketch-geometry (2):
    g0: Circle CenterX=-26 CenterY=-13 CenterZ=0 NormalX=0 NormalY=0 NormalZ=1 AngleXU=0 Radius=10.8
    g1: Circle CenterX=-26 CenterY=-13 CenterZ=0 NormalX=0 NormalY=0 NormalZ=1 AngleXU=0 Radius=9
  constraints (5):
    c: Diameter(g0) = 21.6
    c: Distance(g0,g-2) = 26
    c: DistanceY(g0,g-1) = 13
    c: Coincident(g1,g0)
    c: Diameter(g1) = 18
FEATURE [Sketcher::SketchObject] Sketch005  label="switch_antennas"
  ArcFitTolerance = 1e-06
  ExternalTypes = [0]
  FullyConstrained = true
  MakeInternals = false
  MapMode = 2
  Placement = pos=(0,55,0) rot=(0,0.707107,0.707107;3.14159rad)
  expr: .Placement.Base.y = VarSet.Base_base_lenght
  expr: Constraints[17] = VarSet.base_width
  expr: Constraints[18] = VarSet.case_height
  sketch-geometry (21):
    g0: Circle CenterX=-17 CenterY=-16 CenterZ=0 NormalX=0 NormalY=0 NormalZ=1 AngleXU=0 Radius=3.25
    g1: GeomPoint [constr] X=-17 Y=-16 Z=0
    g2: Circle CenterX=-17 CenterY=-16 CenterZ=0 NormalX=0 NormalY=0 NormalZ=1 AngleXU=0 Radius=7
    g3: Circle CenterX=-17 CenterY=-16 CenterZ=0 NormalX=0 NormalY=0 NormalZ=1 AngleXU=0 Radius=8
    g4: LineSegment [constr] StartX=32.5 StartY=0 StartZ=0 EndX=-32.5 EndY=0 EndZ=0
    g5: LineSegment [constr] StartX=-32.5 StartY=0 StartZ=0 EndX=-32.5 EndY=-25 EndZ=0
    g6: LineSegment [constr] StartX=-32.5 StartY=-25 StartZ=0 EndX=32.5 EndY=-25 EndZ=0
    g7: LineSegment [constr] StartX=32.5 StartY=-25 StartZ=0 EndX=32.5 EndY=0 EndZ=0
    g8: LineSegment StartX=-8.00889 StartY=-18.8 StartZ=0 EndX=5.99111 EndY=-18.8 EndZ=0
    g9: LineSegment StartX=5.99111 StartY=-18.8 StartZ=0 EndX=5.99111 EndY=-16.4 EndZ=0
    g10: LineSegment StartX=5.99111 StartY=-16.4 StartZ=0 EndX=-8.00889 EndY=-16.4 EndZ=0
    g11: LineSegment StartX=-8.00889 StartY=-16.4 StartZ=0 EndX=-8.00889 EndY=-18.8 EndZ=0
    g12: GeomPoint [constr] X=-1.00889 Y=-17.6 Z=0
    g13: LineSegment StartX=-8.00889 StartY=-2.4 StartZ=0 EndX=5.99111 EndY=-2.4 EndZ=0
    g14: LineSegment StartX=5.99111 StartY=-2.4 StartZ=0 EndX=5.99111 EndY=0 EndZ=0
    g15: LineSegment StartX=5.99111 StartY=0 StartZ=0 EndX=-8.00889 EndY=0 EndZ=0
    g16: LineSegment StartX=-8.00889 StartY=0 StartZ=0 EndX=-8.00889 EndY=-2.4 EndZ=0
    g17: GeomPoint [constr] X=-1.00889 Y=-1.2 Z=0
    g18: Circle CenterX=-1.00889 CenterY=-9.4 CenterZ=0 NormalX=0 NormalY=0 NormalZ=1 AngleXU=0 Radius=3
    g19: LineSegment [constr] StartX=-1.00889 StartY=-17.6 StartZ=0 EndX=-1.00889 EndY=-1.2 EndZ=0
    g20: GeomPoint [constr] X=-1.00889 Y=-9.4 Z=0
  constraints (51):
    c: Diameter(g0) = 6.5
    c: Coincident(g0,g1)
    c: Coincident(g2,g0)
    c: Coincident(g3,g0)
    c: Diameter(g2) = 14
    c: Diameter(g3) = 16
    c: DistanceX(g0,g-1) = 17
    c: DistanceY(g0,g-1) = 16
    c: Coincident(g4,g5)
    c: Coincident(g5,g6)
    c: Coincident(g6,g7)
    c: Coincident(g7,g4)
    c: Horizontal(g4)
    c: Vertical(g5)
    c: Vertical(g7)
    c: PointOnObject(g4,g-1)
    c: Symmetric(g5,g6,g-2)
    c: DistanceX(g6,g6) = 65
    c: DistanceY(g6,g-1) = 25
    c: Coincident(g8,g9)
    c: Coincident(g9,g10)
    c: Coincident(g10,g11)
    c: Coincident(g11,g8)
    c: Symmetric(g10,g8,g12)
    c: Coincident(g13,g14)
    c: Coincident(g14,g15)
    c: Coincident(g15,g16)
    c: Coincident(g16,g13)
    c: Symmetric(g15,g13,g17)
    c: Equal(g11,g16)
    c: Equal(g10,g13)
    c: Diameter(g18) = 6
    c: Coincident(g19,g12)
    c: Coincident(g19,g17)
    c: Symmetric(g19,g19,g20)
    c: Coincident(g18,g20)
    c: Distance(g18,g13) = 4
    c: Perpendicular(g9,g8)
    c: Perpendicular(g11,g10)
    c: Perpendicular(g14,g13)
    c: Perpendicular(g16,g15)
    c: Parallel(g10,g13)
    c: Parallel(g8,g15)
    c: Perpendicular(g10,g19)
    c: Perpendicular(g14,g15)
    c: Parallel(g15,g4)
    c: DistanceY(g8,g9) = 2.4
    c: PointOnObject(g15,g4)
    c: DistanceY(g9,g13) = 14
    c: DistanceX(g10,g9) = 14
    c: Distance(g10,g3) = 1
FEATURE [PartDesign::Pocket] Pocket007  label="usb_cap_inside"
  BaseFeature = -> Pocket002
  Direction = (1,0,0)
  Length = 5
  Length2 = 5
  Profile = -> Sketch004 [Edge2]
  ReferenceAxis = -> Sketch004 [N_Axis]
  Refine = true
  Suppressed = false
  Type = 0
FEATURE [PartDesign::Pocket] Pocket008  label="usb_cap_outside"
  BaseFeature = -> Pocket007
  Direction = (1,0,0)
  Length = 1.5
  Length2 = 5
  Profile = -> Sketch004 [Edge1]
  ReferenceAxis = -> Sketch004 [N_Axis]
  Refine = true
  Suppressed = false
  Type = 0
  expr: Length = VarSet.Base_case_thickness / 2
FEATURE [PartDesign::Pocket] Pocket010
  BaseFeature = -> Pocket008
  Direction = (-1e-16,-1,2e-16)
  Length = 3
  Length2 = 5
  Profile = -> Sketch005 [Edge1]
  ReferenceAxis = -> Sketch005 [N_Axis]
  Refine = true
  Suppressed = false
  Type = 0
  expr: Length = VarSet.Base_case_thickness
FEATURE [PartDesign::Pad] Pad007  label="antenna_"
  BaseFeature = -> Pocket010
  Direction = (1e-16,1,-2e-16)
  Length = 10
  Length2 = 10
  Profile = -> Sketch005 [Edge3,Edge2]
  ReferenceAxis = -> Sketch005 [N_Axis]
  Refine = true
  Suppressed = false
  Type = 0
FEATURE [Sketcher::SketchObject] Sketch019  label="pogopins_case002"
  ArcFitTolerance = 1e-06
  AttachmentSupport = -> [XZ_Plane053]
  ExternalTypes = [0]
  FullyConstrained = true
  MakeInternals = false
  MapMode = 5
  Placement = pos=(0,0,0) rot=(1,0,0;1.5708rad)
  expr: Constraints[12] = VarSet.Base_pogopins_r
  expr: Constraints[1] = VarSet.case_height / 2
  expr: Constraints[25] = VarSet.Base_pogoping_lenght
  sketch-geometry (11):
    g0: GeomPoint X=0 Y=-12.5 Z=0
    g1: ArcOfCircle CenterX=-5.45 CenterY=-12.5 CenterZ=0 NormalX=0 NormalY=0 NormalZ=1 AngleXU=0 Radius=2.1 StartAngle=1.5708 EndAngle=4.71239
    g2: ArcOfCircle CenterX=5.45 CenterY=-12.5 CenterZ=0 NormalX=0 NormalY=0 NormalZ=1 AngleXU=0 Radius=2.1 StartAngle=4.71239 EndAngle=7.85398
    g3: LineSegment StartX=-5.45 StartY=-10.4 StartZ=0 EndX=5.45 EndY=-10.4 EndZ=0
    g4: LineSegment StartX=-5.45 StartY=-14.6 StartZ=0 EndX=5.45 EndY=-14.6 EndZ=0
    g5: LineSegment [constr] StartX=-5.45 StartY=-12.5 StartZ=0 EndX=5.45 EndY=-12.5 EndZ=0
    g6: GeomPoint [constr] X=0 Y=-12.5 Z=0
    g7: LineSegment [constr] StartX=-7.55 StartY=-10.4 StartZ=0 EndX=-7.55 EndY=-14.6 EndZ=0
    g8: LineSegment [constr] StartX=-7.55 StartY=-14.6 StartZ=0 EndX=7.55 EndY=-14.6 EndZ=0
    g9: LineSegment [constr] StartX=7.55 StartY=-14.6 StartZ=0 EndX=7.55 EndY=-10.4 EndZ=0
    g10: LineSegment [constr] StartX=7.55 StartY=-10.4 StartZ=0 EndX=-7.55 EndY=-10.4 EndZ=0
  constraints (26):
    c: PointOnObject(g0,g-2)
    c: Distance(g0,g-1) = 12.5
    c: Tangent(g1,g3) = 1.5708
    c: Tangent(g1,g4) = -1.5708
    c: Tangent(g2,g3) = 1.5708
    c: Tangent(g2,g4) = -1.5708
    c: Equal(g1,g2)
    c: Horizontal(g3)
    c: Coincident(g5,g1)
    c: Coincident(g5,g2)
    c: Symmetric(g5,g5,g6)
    c: Coincident(g0,g6)
    c: Radius(g1) = 2.1
    c: Coincident(g7,g8)
    c: Coincident(g8,g9)
    c: Coincident(g9,g10)
    c: Coincident(g10,g7)
    c: Vertical(g7)
    c: Vertical(g9)
    c: Horizontal(g8)
    c: Horizontal(g10)
    c: PointOnObject(g2,g10)
    c: PointOnObject(g2,g8)
    c: Tangent(g2,g9)
    c: Tangent(g7,g1)
    c: DistanceX(g7,g9) = 15.1
FEATURE [Sketcher::SketchObject] Sketch020  label="pogoPins_outside"
  ArcFitTolerance = 1e-06
  ExternalTypes = [0]
  FullyConstrained = true
  MakeInternals = false
  MapMode = 5
  Placement = pos=(0,3,0) rot=(0,0.707107,0.707107;3.14159rad)
  expr: Constraints[11] = VarSet.case_height / 2
  expr: Constraints[12] = VarSet.Base_pogopin_outside
  expr: Constraints[13] = 3 * VarSet.Base_pogopins_r
  sketch-geometry (6):
    g0: GeomPoint [constr] X=0 Y=-12.5 Z=0
    g1: LineSegment StartX=-10.5 StartY=-15.65 StartZ=0 EndX=-10.5 EndY=-9.35 EndZ=0
    g2: LineSegment StartX=-10.5 StartY=-9.35 StartZ=0 EndX=10.5 EndY=-9.35 EndZ=0
    g3: LineSegment StartX=10.5 StartY=-9.35 StartZ=0 EndX=10.5 EndY=-15.65 EndZ=0
    g4: LineSegment StartX=10.5 StartY=-15.65 StartZ=0 EndX=-10.5 EndY=-15.65 EndZ=0
    g5: GeomPoint [constr] X=0 Y=-12.5 Z=0
  constraints (14):
    c: PointOnObject(g0,g-2)
    c: Coincident(g1,g2)
    c: Coincident(g2,g3)
    c: Coincident(g3,g4)
    c: Coincident(g4,g1)
    c: Vertical(g1)
    c: Vertical(g3)
    c: Horizontal(g2)
    c: Horizontal(g4)
    c: Symmetric(g3,g1,g5)
    c: Coincident(g5,g0)
    c: DistanceY(g0,g-1) = 12.5
    c: DistanceX(g1,g2) = 21
    c: DistanceY(g3,g2) = 6.3
FEATURE [PartDesign::Pocket] Pocket018  label="pogoPins_outside001"
  BaseFeature = -> Pad007
  Direction = (-1e-16,-1,2e-16)
  Length = 3
  Length2 = 5
  Profile = -> Sketch020
  ReferenceAxis = -> Sketch020 [N_Axis]
  Refine = true
  Suppressed = false
  Type = 0
  expr: Length = VarSet.Base_case_thickness
FEATURE [Sketcher::SketchObject] Sketch024  label="nuts"
  ArcFitTolerance = 1e-06
  AttachmentSupport = -> [Pocket018]
  ExternalGeometry = -> [Pocket018]
  ExternalTypes = [0,0,0,0]
  FullyConstrained = true
  MakeInternals = false
  MapMode = 5
  Placement = pos=(0,0,-25) rot=(1,0,0;3.14159rad)
  sketch-geometry (28):
    g0: LineSegment StartX=-27.0566 StartY=-6.5 StartZ=0 EndX=-25.6132 EndY=-4 EndZ=0
    g1: LineSegment StartX=-25.6132 StartY=-4 StartZ=0 EndX=-27.0566 EndY=-1.5 EndZ=0
    g2: LineSegment StartX=-27.0566 StartY=-1.5 StartZ=0 EndX=-29.9434 EndY=-1.5 EndZ=0
    g3: LineSegment StartX=-29.9434 StartY=-1.5 StartZ=0 EndX=-31.3868 EndY=-4 EndZ=0
    g4: LineSegment StartX=-31.3868 StartY=-4 StartZ=0 EndX=-29.9434 EndY=-6.5 EndZ=0
    g5: LineSegment StartX=-29.9434 StartY=-6.5 StartZ=0 EndX=-27.0566 EndY=-6.5 EndZ=0
    g6: Circle [constr] CenterX=-28.5 CenterY=-4 CenterZ=0 NormalX=0 NormalY=0 NormalZ=1 AngleXU=0 Radius=2.88675
    g7: LineSegment StartX=25.6132 StartY=-4 StartZ=0 EndX=27.0566 EndY=-6.5 EndZ=0
    g8: LineSegment StartX=27.0566 StartY=-6.5 StartZ=0 EndX=29.9434 EndY=-6.5 EndZ=0
    g9: LineSegment StartX=29.9434 StartY=-6.5 StartZ=0 EndX=31.3868 EndY=-4 EndZ=0
    g10: LineSegment StartX=31.3868 StartY=-4 StartZ=0 EndX=29.9434 EndY=-1.5 EndZ=0
    g11: LineSegment StartX=29.9434 StartY=-1.5 StartZ=0 EndX=27.0566 EndY=-1.5 EndZ=0
    g12: LineSegment StartX=27.0566 StartY=-1.5 StartZ=0 EndX=25.6132 EndY=-4 EndZ=0
    g13: Circle [constr] CenterX=28.5 CenterY=-4 CenterZ=0 NormalX=0 NormalY=0 NormalZ=1 AngleXU=0 Radius=2.88675
    g14: LineSegment StartX=27.0566 StartY=-48.5 StartZ=0 EndX=25.6132 EndY=-51 EndZ=0
    g15: LineSegment StartX=25.6132 StartY=-51 StartZ=0 EndX=27.0566 EndY=-53.5 EndZ=0
    g16: LineSegment StartX=27.0566 StartY=-53.5 StartZ=0 EndX=29.9434 EndY=-53.5 EndZ=0
    g17: LineSegment StartX=29.9434 StartY=-53.5 StartZ=0 EndX=31.3868 EndY=-51 EndZ=0
    g18: LineSegment StartX=31.3868 StartY=-51 StartZ=0 EndX=29.9434 EndY=-48.5 EndZ=0
    g19: LineSegment StartX=29.9434 StartY=-48.5 StartZ=0 EndX=27.0566 EndY=-48.5 EndZ=0
    g20: Circle [constr] CenterX=28.5 CenterY=-51 CenterZ=0 NormalX=0 NormalY=0 NormalZ=1 AngleXU=0 Radius=2.88675
    g21: LineSegment StartX=-25.6132 StartY=-51 StartZ=0 EndX=-27.0566 EndY=-48.5 EndZ=0
    g22: LineSegment StartX=-27.0566 StartY=-48.5 StartZ=0 EndX=-29.9434 EndY=-48.5 EndZ=0
    g23: LineSegment StartX=-29.9434 StartY=-48.5 StartZ=0 EndX=-31.3868 EndY=-51 EndZ=0
    g24: LineSegment StartX=-31.3868 StartY=-51 StartZ=0 EndX=-29.9434 EndY=-53.5 EndZ=0
    g25: LineSegment StartX=-29.9434 StartY=-53.5 StartZ=0 EndX=-27.0566 EndY=-53.5 EndZ=0
    g26: LineSegment StartX=-27.0566 StartY=-53.5 StartZ=0 EndX=-25.6132 EndY=-51 EndZ=0
    g27: Circle [constr] CenterX=-28.5 CenterY=-51 CenterZ=0 NormalX=0 NormalY=0 NormalZ=1 AngleXU=0 Radius=2.88675
  constraints (64):
    c: Coincident(g0,g1)
    c: Coincident(g1,g2)
    c: Coincident(g2,g3)
    c: Coincident(g3,g4)
    c: Coincident(g4,g5)
    c: Coincident(g5,g0)
    c: Equal(g0, g1-g5) x5
    c: PointOnObject(g0,g6)
    c: PointOnObject(g1,g6)
    c: PointOnObject(g2,g6)
    c: PointOnObject(g3,g6)
    c: PointOnObject(g4,g6)
    c: PointOnObject(g5,g6)
    c: Coincident(g6,g-3)
    c: Coincident(g7,g8)
    c: Coincident(g8,g9)
    c: Coincident(g9,g10)
    c: Coincident(g10,g11)
    c: Coincident(g11,g12)
    c: Coincident(g12,g7)
    c: Equal(g7, g8-g12) x5
    c: PointOnObject(g7,g13)
    c: PointOnObject(g8,g13)
    c: PointOnObject(g9,g13)
    c: PointOnObject(g10,g13)
    c: PointOnObject(g11,g13)
    c: PointOnObject(g12,g13)
    c: Coincident(g13,g-4)
    c: Coincident(g14,g15)
    c: Coincident(g15,g16)
    c: Coincident(g16,g17)
    c: Coincident(g17,g18)
    c: Coincident(g18,g19)
    c: Coincident(g19,g14)
    c: Equal(g14, g15-g19) x5
    c: PointOnObject(g14,g20)
    c: PointOnObject(g15,g20)
    c: PointOnObject(g16,g20)
    c: PointOnObject(g17,g20)
    c: PointOnObject(g18,g20)
    c: PointOnObject(g19,g20)
    c: Coincident(g20,g-5)
    c: Coincident(g21,g22)
    c: Coincident(g22,g23)
    c: Coincident(g23,g24)
    c: Coincident(g24,g25)
    c: Coincident(g25,g26)
    c: Coincident(g26,g21)
    c: Equal(g21, g22-g26) x5
    c: PointOnObject(g21,g27)
    c: PointOnObject(g22,g27)
    c: PointOnObject(g23,g27)
    c: PointOnObject(g24,g27)
    c: PointOnObject(g25,g27)
    c: PointOnObject(g26,g27)
    c: Coincident(g27,g-6)
    c: Parallel(g22,g-1)
    c: Parallel(g2,g-1)
    c: Parallel(g-1,g11)
    c: Parallel(g19,g-1)
    c: Equal(g27,g20)
    c: Equal(g20,g13)
    c: Equal(g13,g6)
    c: Distance(g2,g5) = 5
FEATURE [PartDesign::Pocket] Pocket025  label="nuts002"
  BaseFeature = -> Pocket018
  Direction = (0,0,1)
  Length = 20
  Length2 = 5
  Profile = -> Sketch024
  ReferenceAxis = -> Sketch024 [N_Axis]
  Refine = true
  Suppressed = false
  Type = 0
  expr: Length = VarSet.case_height * 0.8
FEATURE [Sketcher::SketchObject] Sketch032  label="gasket001"
  ArcFitTolerance = 1e-06
  AttachmentSupport = -> [YZ_Plane053]
  ExternalGeometry = -> [Sketch]
  ExternalTypes = [0]
  FullyConstrained = true
  MakeInternals = false
  MapMode = 5
  Placement = pos=(0,0,0) rot=(0.57735,0.57735,0.57735;2.0944rad)
  expr: Constraints[10] = VarSet.Base_gasket_width
  expr: Constraints[11] = VarSet.Base_gasket_height
  sketch-geometry (5):
    g0: LineSegment StartX=1 StartY=1 StartZ=0 EndX=1 EndY=-1 EndZ=0
    g1: LineSegment StartX=1 StartY=-1 StartZ=0 EndX=2 EndY=-1 EndZ=0
    g2: LineSegment StartX=2 StartY=-1 StartZ=0 EndX=2 EndY=1 EndZ=0
    g3: LineSegment StartX=2 StartY=1 StartZ=0 EndX=1 EndY=1 EndZ=0
    g4: GeomPoint [constr] X=1.5 Y=0 Z=0
  constraints (12):
    c: Coincident(g0,g1)
    c: Coincident(g1,g2)
    c: Coincident(g2,g3)
    c: Coincident(g3,g0)
    c: Vertical(g0)
    c: Vertical(g2)
    c: Horizontal(g1)
    c: Horizontal(g3)
    c: Symmetric(g2,g0,g4)
    c: Coincident(g4,g-3)
    c: DistanceX(g0,g2) = 1
    c: DistanceY(g0,g0) = 2
FEATURE [PartDesign::SubtractivePipe] SubtractivePipe
  AuxilleryCurvelinear = true
  AuxillerySpineTangent = false
  BaseFeature = -> Pocket025
  Binormal = (0,0,0)
  Mode = 0
  Profile = -> Sketch032
  Refine = true
  Spine = -> Sketch [Edge21,Edge20,Edge19,Edge34,Edge33,Edge32,Edge31,Edge30,Edge29,Edge28,Edge27,Edge26,Edge25,Edge24,Edge23,Edge22]
  SpineTangent = false
  Suppressed = false
  Transformation = 0
  Transition = 0
FEATURE [PartDesign::Pocket] Pocket028  label="onoff_"
  BaseFeature = -> SubtractivePipe
  Direction = (-1e-16,-1,2e-16)
  Length = 3
  Length2 = 5
  Profile = -> Sketch005 [Edge12]
  ReferenceAxis = -> Sketch005 [N_Axis]
  Refine = true
  Suppressed = false
  Type = 0
  expr: Length = VarSet.Base_case_thickness
FEATURE [App::Point] Origin107
  Role = Origin
FEATURE [PartDesign::Pad] Pad020
  BaseFeature = -> Pocket028
  Direction = (1e-16,1,-2e-16)
  Length = 20
  Length2 = 10
  Profile = -> Sketch005 [Edge10,Edge9,Edge8,Edge11,Edge6,Edge7,Edge4,Edge5]
  ReferenceAxis = -> Sketch005 [N_Axis]
  Refine = true
  Suppressed = false
  Type = 0
FEATURE [Sketcher::SketchObject] Sketch046  label="gps_mount"
  ArcFitTolerance = 1e-06
  AttachmentOffset = pos=(0,0,-5) rot=(0,0,1;0rad)
  AttachmentSupport = -> [XY_Plane053]
  ExternalTypes = [0]
  FullyConstrained = true
  MakeInternals = false
  MapMode = 5
  Placement = pos=(0,0,-5) rot=(0,0,1;0rad)
  expr: Constraints[10] = 50 mm
  expr: Constraints[8] = VarSet.Base_base_lenght - VarSet.Base_case_thickness
  sketch-geometry (16):
    g0: LineSegment [constr] StartX=-25 StartY=0 StartZ=0 EndX=25 EndY=0 EndZ=0
    g1: LineSegment [constr] StartX=25 StartY=0 StartZ=0 EndX=25 EndY=52 EndZ=0
    g2: LineSegment [constr] StartX=25 StartY=52 StartZ=0 EndX=-25 EndY=52 EndZ=0
    g3: LineSegment [constr] StartX=-25 StartY=52 StartZ=0 EndX=-25 EndY=0 EndZ=0
    g4: LineSegment StartX=-25 StartY=52 StartZ=0 EndX=-25 EndY=44.8 EndZ=0
    g5: LineSegment StartX=-23.5 StartY=46 StartZ=0 EndX=-23.5 EndY=52 EndZ=0
    g6: LineSegment StartX=-23.5 StartY=52 StartZ=0 EndX=-25 EndY=52 EndZ=0
    g7: LineSegment StartX=-23.5 StartY=46 StartZ=0 EndX=-22.5 EndY=46 EndZ=0
    g8: LineSegment StartX=-22.5 StartY=46 StartZ=0 EndX=-22.5 EndY=44.8 EndZ=0
    g9: LineSegment StartX=-22.5 StartY=44.8 StartZ=0 EndX=-25 EndY=44.8 EndZ=0
    g10: LineSegment StartX=-6.9 StartY=52 StartZ=0 EndX=-8.4 EndY=52 EndZ=0
    g11: LineSegment StartX=-6.9 StartY=44.8 StartZ=0 EndX=-9.4 EndY=44.8 EndZ=0
    g12: LineSegment StartX=-9.4 StartY=46 StartZ=0 EndX=-8.4 EndY=46 EndZ=0
    g13: LineSegment StartX=-8.4 StartY=46 StartZ=0 EndX=-8.4 EndY=52 EndZ=0
    g14: LineSegment StartX=-6.9 StartY=52 StartZ=0 EndX=-6.9 EndY=44.8 EndZ=0
    g15: LineSegment StartX=-9.4 StartY=44.8 StartZ=0 EndX=-9.4 EndY=46 EndZ=0
  constraints (46):
    c: Coincident(g0,g1)
    c: Coincident(g1,g2)
    c: Coincident(g2,g3)
    c: Coincident(g3,g0)
    c: Horizontal(g0)
    c: Vertical(g1)
    c: Vertical(g3)
    c: PointOnObject(g0,g-1)
    c: DistanceY(g0,g2) = 52
    c: Symmetric(g2,g1,g-2)
    c: DistanceX(g2,g1) = 50
    c: Coincident(g2,g4)
    c: PointOnObject(g4,g3)
    c: PointOnObject(g5,g2)
    c: Vertical(g5)
    c: Coincident(g5,g6)
    c: Coincident(g6,g4)
    c: Distance(g2,g5) = 1.5
    c: Coincident(g5,g7)
    c: Horizontal(g7)
    c: Coincident(g7,g8)
    c: Vertical(g8)
    c: Coincident(g9,g8)
    c: Coincident(g9,g4)
    c: Horizontal(g9)
    c: Distance(g5,g7) = 1
    c: Distance(g5,g6) = 6
    c: DistanceY(g8,g7) = 1.2
    c: PointOnObject(g10,g2)
    c: PointOnObject(g10,g2)
    c: Equal(g6,g10)
    c: Horizontal(g11)
    c: Coincident(g12,g13)
    c: Coincident(g13,g10)
    c: Perpendicular(g13,g12)
    c: Equal(g9,g11)
    c: Equal(g7,g12)
    c: Equal(g5,g13)
    c: DistanceX(g5,g12) = 15.1
    c: Coincident(g14,g10)
    c: Coincident(g14,g11)
    c: Vertical(g14)
    c: Coincident(g15,g11)
    c: Coincident(g15,g12)
    c: Vertical(g15)
    c: Equal(g8,g15)
FEATURE [PartDesign::Pad] Pad021  label="gps_mount001"
  BaseFeature = -> Pad020
  Direction = (0,0,1)
  Length = 18
  Length2 = 10
  Profile = -> Sketch046
  ReferenceAxis = -> Sketch046 [N_Axis]
  Refine = true
  Reversed = true
  Suppressed = false
  Type = 0
FEATURE [App::FeaturePython] Joint017  label="gps"  # Assembly joint (typed FeaturePython)
  Activated = true
  AngleMax = 0
  AngleMin = 0
  Detach1 = false
  Detach2 = false
  Distance = 0
  Distance2 = 0
  EnableAngleMax = false
  EnableAngleMin = false
  EnableLengthMax = false
  EnableLengthMin = false
  JointType = 0 (Fixed)
  LengthMax = 0
  LengthMin = 0
  Offset2 = pos=(0,0,0) rot=(0,0,1;1.5708rad)
  Placement1 = pos=(7.5,0,0) rot=(0.57735,0.57735,0.57735;4.18879rad)
  Placement2 = pos=(-23.5,46,-13.5) rot=(0.707107,0.707107,0;3.14159rad)
  Reference1 = -> Assembly [gps_antenna.Body012.Edge10,gps_antenna.Body012.Edge10]
  Reference2 = -> Assembly [base.Body.Edge456,base.Body.Edge456]
FEATURE [Part::Feature] root_solid  label="usb_c_male"
  shape: bbox 12.41 x 38.4 x 7.414 mm, 56 faces (baked)
FEATURE [App::DocumentObjectGroup] Group  label="misc"
  Group = -> [PCB_solid001,_0205K69_Cover_for_0_5_Deep_x_0_12_Diameter_Toggle_Switch,TSM102A1_v5,antenna_WiFi_RP_SMA_conn_v2,Part__Feature070,PCB_solid,Part__Feature064,Part007,PCB_solid002,root_solid,Magnetic_Pogo_Connector_3_Pin__Type_1_,Magnetic_Pogo_Connector_3_Pin__Type_2_]
FEATURE [App::Link] usb_c_male  label="usb_c_male001"
  LinkPlacement = pos=(-65.75,27.3832,-10.9675) rot=(0.707107,-0.707107,0;3.14159rad)
  LinkedObject = -> root_solid
  Placement = pos=(-65.75,27.3832,-10.9675) rot=(0.707107,-0.707107,0;3.14159rad)
FEATURE [App::FeaturePython] Joint018  label="usb_c_test"  # Assembly joint (typed FeaturePython)
  Activated = true
  AngleMax = 0
  AngleMin = 0
  Detach1 = false
  Detach2 = false
  Distance = 0
  Distance2 = 0
  EnableAngleMax = false
  EnableAngleMin = false
  EnableLengthMax = false
  EnableLengthMin = false
  JointType = 0 (Fixed)
  LengthMax = 0
  LengthMin = 0
  Offset2 = pos=(0,0,28) rot=(0,0,1;0rad)
  Placement1 = pos=(-15.0755,18.2895,1.59765) rot=(0.57735,-0.57735,-0.57735;2.0944rad)
  Placement2 = pos=(0.0937431,-42.1745,3.425) rot=(-1,0,0;4.71239rad)
  Reference1 = -> Assembly [RAK19003__Solid_.Face135,RAK19003__Solid_.Face135]
  Reference2 = -> Assembly [usb_c_male.Face35,usb_c_male.Face35]
FEATURE [Sketcher::SketchObject] Sketch047  label="on_off_sma"
  ArcFitTolerance = 1e-06
  AttachmentSupport = -> [Pad021]
  ExternalGeometry = -> [Pad021]
  ExternalTypes = [0,0]
  FullyConstrained = true
  MakeInternals = false
  MapMode = 5
  Placement = pos=(0,52,0) rot=(1,0,0;1.5708rad)
  expr: Constraints[10] = 13.2
  sketch-geometry (12):
    g0: LineSegment StartX=-5.59111 StartY=-5.25 StartZ=0 EndX=-5.59111 EndY=-13.55 EndZ=0
    g1: LineSegment StartX=-5.59111 StartY=-13.55 StartZ=0 EndX=7.60889 EndY=-13.55 EndZ=0
    g2: LineSegment StartX=7.60889 StartY=-13.55 StartZ=0 EndX=7.60889 EndY=-5.25 EndZ=0
    g3: LineSegment StartX=7.60889 StartY=-5.25 StartZ=0 EndX=-5.59111 EndY=-5.25 EndZ=0
    g4: GeomPoint [constr] X=1.00889 Y=-9.4 Z=0
    g5: LineSegment StartX=19.3671 StartY=-20.1 StartZ=0 EndX=21.7343 EndY=-16 EndZ=0
    g6: LineSegment StartX=21.7343 StartY=-16 StartZ=0 EndX=19.3671 EndY=-11.9 EndZ=0
    g7: LineSegment StartX=19.3671 StartY=-11.9 StartZ=0 EndX=14.6329 EndY=-11.9 EndZ=0
    g8: LineSegment StartX=14.6329 StartY=-11.9 StartZ=0 EndX=12.2657 EndY=-16 EndZ=0
    g9: LineSegment StartX=12.2657 StartY=-16 StartZ=0 EndX=14.6329 EndY=-20.1 EndZ=0
    g10: LineSegment StartX=14.6329 StartY=-20.1 StartZ=0 EndX=19.3671 EndY=-20.1 EndZ=0
    g11: Circle [constr] CenterX=17 CenterY=-16 CenterZ=0 NormalX=0 NormalY=0 NormalZ=1 AngleXU=0 Radius=4.73427
  constraints (28):
    c: Coincident(g0,g1)
    c: Coincident(g1,g2)
    c: Coincident(g2,g3)
    c: Coincident(g3,g0)
    c: Vertical(g0)
    c: Vertical(g2)
    c: Horizontal(g1)
    c: Horizontal(g3)
    c: Symmetric(g2,g0,g4)
    c: Coincident(g4,g-3)
    c: DistanceX(g0,g2) = 13.2
    c: DistanceY(g0,g0) = 8.3
    c: Coincident(g5,g6)
    c: Coincident(g6,g7)
    c: Coincident(g7,g8)
    c: Coincident(g8,g9)
    c: Coincident(g9,g10)
    c: Coincident(g10,g5)
    c: Equal(g5, g6-g10) x5
    c: PointOnObject(g5,g11)
    c: PointOnObject(g6,g11)
    c: PointOnObject(g7,g11)
    c: PointOnObject(g8,g11)
    c: PointOnObject(g9,g11)
    c: PointOnObject(g10,g11)
    c: Coincident(g11,g-4)
    c: Parallel(g7,g-1)
    c: DistanceY(g9,g7) = 8.2
FEATURE [PartDesign::Pocket] Pocket029  label="onff_sma_recess"
  BaseFeature = -> Pad021
  Direction = (0,1,-2e-16)
  Length = 0.6
  Length2 = 5
  Profile = -> Sketch047
  ReferenceAxis = -> Sketch047 [N_Axis]
  Refine = true
  Suppressed = false
  Type = 0
  expr: Length = VarSet.Base_case_thickness * 0.2
FEATURE [Sketcher::SketchObject] Sketch048  label="outside_clips"
  ArcFitTolerance = 1e-06
  AttachmentSupport = -> [XZ_Plane065]
  ExternalGeometry = -> [Pocket027]
  ExternalTypes = [0,0,0]
  FullyConstrained = true
  MakeInternals = false
  MapMode = 5
  Placement = pos=(0,0,0) rot=(1,0,0;1.5708rad)
  expr: Constraints[22] = VarSet.Base_connector_clip
  sketch-geometry (15):
    g0: GeomPoint X=-32.5 Y=-12.5 Z=0
    g1: GeomPoint X=32.5 Y=-12.5 Z=0
    g2: LineSegment [constr] StartX=-32.5 StartY=-12.5 StartZ=0 EndX=32.5 EndY=-12.5 EndZ=0
    g3: LineSegment StartX=-31.5 StartY=-8.5 StartZ=0 EndX=-31.5 EndY=-16.5 EndZ=0
    g4: LineSegment StartX=-31.5 StartY=-16.5 StartZ=0 EndX=-23.5 EndY=-16.5 EndZ=0
    g5: LineSegment StartX=-23.5 StartY=-16.5 StartZ=0 EndX=-23.5 EndY=-8.5 EndZ=0
    g6: LineSegment StartX=-23.5 StartY=-8.5 StartZ=0 EndX=-31.5 EndY=-8.5 EndZ=0
    g7: GeomPoint [constr] X=-27.5 Y=-12.5 Z=0
    g8: LineSegment StartX=23.5 StartY=-8.5 StartZ=0 EndX=23.5 EndY=-16.5 EndZ=0
    g9: LineSegment StartX=23.5 StartY=-16.5 StartZ=0 EndX=31.5 EndY=-16.5 EndZ=0
    g10: LineSegment StartX=31.5 StartY=-16.5 StartZ=0 EndX=31.5 EndY=-8.5 EndZ=0
    g11: LineSegment StartX=31.5 StartY=-8.5 StartZ=0 EndX=23.5 EndY=-8.5 EndZ=0
    g12: GeomPoint [constr] X=27.5 Y=-12.5 Z=0
    g13: GeomPoint [constr] X=-27.5 Y=-12.5 Z=0
    g14: GeomPoint [constr] X=27.5 Y=-12.5 Z=0
  constraints (31):
    c: Symmetric(g-6,g-6,g0)
    c: Symmetric(g-15,g-15,g1)
    c: Coincident(g2,g0)
    c: Coincident(g2,g1)
    c: Coincident(g3,g4)
    c: Coincident(g4,g5)
    c: Coincident(g5,g6)
    c: Coincident(g6,g3)
    c: Vertical(g3)
    c: Vertical(g5)
    c: Horizontal(g4)
    c: Horizontal(g6)
    c: Symmetric(g5,g3,g7)
    c: PointOnObject(g7,g2)
    c: Coincident(g8,g9)
    c: Coincident(g9,g10)
    c: Coincident(g10,g11)
    c: Coincident(g11,g8)
    c: Vertical(g8)
    c: Vertical(g10)
    c: Horizontal(g9)
    c: Symmetric(g10,g8,g12)
    c: DistanceX(g3,g5) = 8
    c: Equal(g6,g3)
    c: Equal(g3,g8)
    c: Equal(g8,g11)
    c: DistanceX(g0,g7) = 5
    c: Symmetric(g7,g12,g-2)
    c: Coincident(g13,g7)
    c: Coincident(g14,g12)
    c: Perpendicular(g10,g11)
FEATURE [Sketcher::SketchObject] Sketch049  label="inside_clips"
  ArcFitTolerance = 1e-06
  AttachmentOffset = pos=(0,0,1.6) rot=(0,0,1;0rad)
  AttachmentSupport = -> [XZ_Plane065]
  ExternalGeometry = -> [Sketch048]
  ExternalTypes = [0,0,0,0,0,0,0,0]
  FullyConstrained = true
  MakeInternals = false
  MapMode = 5
  Placement = pos=(0,-1.6,4e-16) rot=(1,0,0;1.5708rad)
  expr: .AttachmentOffset.Base.z = VarSet.Base_connector_clip_height
  expr: Constraints[27] = VarSet.Base_connector_clip * 0.5
  sketch-geometry (14):
    g0: LineSegment [constr] StartX=-31.5 StartY=-16.5 StartZ=0 EndX=-23.5 EndY=-8.5 EndZ=0
    g1: LineSegment [constr] StartX=23.5 StartY=-8.5 StartZ=0 EndX=31.5 EndY=-16.5 EndZ=0
    g2: GeomPoint X=-27.5 Y=-12.5 Z=0
    g3: GeomPoint X=27.5 Y=-12.5 Z=0
    g4: LineSegment StartX=-29.5 StartY=-10.5 StartZ=0 EndX=-29.5 EndY=-14.5 EndZ=0
    g5: LineSegment StartX=-29.5 StartY=-14.5 StartZ=0 EndX=-25.5 EndY=-14.5 EndZ=0
    g6: LineSegment StartX=-25.5 StartY=-14.5 StartZ=0 EndX=-25.5 EndY=-10.5 EndZ=0
    g7: LineSegment StartX=-25.5 StartY=-10.5 StartZ=0 EndX=-29.5 EndY=-10.5 EndZ=0
    g8: GeomPoint [constr] X=-27.5 Y=-12.5 Z=0
    g9: LineSegment StartX=25.5 StartY=-10.5 StartZ=0 EndX=25.5 EndY=-14.5 EndZ=0
    g10: LineSegment StartX=25.5 StartY=-14.5 StartZ=0 EndX=29.5 EndY=-14.5 EndZ=0
    g11: LineSegment StartX=29.5 StartY=-14.5 StartZ=0 EndX=29.5 EndY=-10.5 EndZ=0
    g12: LineSegment StartX=29.5 StartY=-10.5 StartZ=0 EndX=25.5 EndY=-10.5 EndZ=0
    g13: GeomPoint [constr] X=27.5 Y=-12.5 Z=0
  constraints (30):
    c: Coincident(g0,g-4)
    c: Coincident(g0,g-6)
    c: Coincident(g1,g-8)
    c: Coincident(g1,g-10)
    c: Symmetric(g0,g0,g2)
    c: Symmetric(g1,g1,g3)
    c: Coincident(g4,g5)
    c: Coincident(g5,g6)
    c: Coincident(g6,g7)
    c: Coincident(g7,g4)
    c: Vertical(g4)
    c: Vertical(g6)
    c: Horizontal(g5)
    c: Horizontal(g7)
    c: Symmetric(g6,g4,g8)
    c: Coincident(g8,g2)
    c: Coincident(g9,g10)
    c: Coincident(g10,g11)
    c: Coincident(g11,g12)
    c: Coincident(g12,g9)
    c: Vertical(g9)
    c: Vertical(g11)
    c: Horizontal(g10)
    c: Horizontal(g12)
    c: Symmetric(g11,g9,g13)
    c: Coincident(g13,g3)
    c: PointOnObject(g10,g1)
    c: DistanceX(g4,g6) = 4
    c: Equal(g7,g4)
    c: Equal(g4,g12)
FEATURE [PartDesign::AdditiveLoft] AdditiveLoft  label="clips"
  BaseFeature = -> Pocket027
  Closed = false
  Placement = pos=(0,0,0) rot=(1,0,0;1.5708rad)
  Profile = -> Sketch048
  Refine = true
  Ruled = false
  Sections = -> [Sketch049]
  Suppressed = false
FEATURE [Sketcher::SketchObject] Sketch051  label="clips_outside"
  ArcFitTolerance = 1e-06
  ExternalTypes = [0,0]
  FullyConstrained = true
  MakeInternals = false
  MapMode = 5
  Placement = pos=(0,-12,0) rot=(1,0,0;1.5708rad)
  expr: Constraints[23] = VarSet.Base_connector_clip
  sketch-geometry (13):
    g0: GeomPoint X=-32.5 Y=-12.5 Z=0
    g1: GeomPoint X=32.5 Y=-12.5 Z=0
    g2: LineSegment [constr] StartX=-32.5 StartY=-12.5 StartZ=0 EndX=32.5 EndY=-12.5 EndZ=0
    g3: LineSegment StartX=-31.5 StartY=-8.5 StartZ=0 EndX=-31.5 EndY=-16.5 EndZ=0
    g4: LineSegment StartX=-31.5 StartY=-16.5 StartZ=0 EndX=-23.5 EndY=-16.5 EndZ=0
    g5: LineSegment StartX=-23.5 StartY=-16.5 StartZ=0 EndX=-23.5 EndY=-8.5 EndZ=0
    g6: LineSegment StartX=-23.5 StartY=-8.5 StartZ=0 EndX=-31.5 EndY=-8.5 EndZ=0
    g7: GeomPoint [constr] X=-27.5 Y=-12.5 Z=0
    g8: LineSegment StartX=23.5 StartY=-8.5 StartZ=0 EndX=23.5 EndY=-16.5 EndZ=0
    g9: LineSegment StartX=23.5 StartY=-16.5 StartZ=0 EndX=31.5 EndY=-16.5 EndZ=0
    g10: LineSegment StartX=31.5 StartY=-16.5 StartZ=0 EndX=31.5 EndY=-8.5 EndZ=0
    g11: LineSegment StartX=31.5 StartY=-8.5 StartZ=0 EndX=23.5 EndY=-8.5 EndZ=0
    g12: GeomPoint [constr] X=27.5 Y=-12.5 Z=0
  constraints (29):
    c: Symmetric(g-3,g-3,g0)
    c: Symmetric(g-4,g-4,g1)
    c: Coincident(g2,g0)
    c: Coincident(g2,g1)
    c: Coincident(g3,g4)
    c: Coincident(g4,g5)
    c: Coincident(g5,g6)
    c: Coincident(g6,g3)
    c: Vertical(g3)
    c: Vertical(g5)
    c: Horizontal(g4)
    c: Horizontal(g6)
    c: Symmetric(g5,g3,g7)
    c: PointOnObject(g7,g2)
    c: Coincident(g8,g9)
    c: Coincident(g9,g10)
    c: Coincident(g10,g11)
    c: Coincident(g11,g8)
    c: Vertical(g8)
    c: Vertical(g10)
    c: Horizontal(g9)
    c: Horizontal(g11)
    c: Symmetric(g10,g8,g12)
    c: DistanceX(g3,g5) = 8
    c: Equal(g6,g3)
    c: Equal(g3,g8)
    c: Equal(g8,g11)
    c: Symmetric(g7,g12,g-2)
    c: DistanceX(g0,g7) = 5
FEATURE [Sketcher::SketchObject] Sketch052  label="clips_inside"
  ArcFitTolerance = 1e-06
  AttachmentOffset = pos=(0,0,-1.6) rot=(0,0,1;0rad)
  ExternalGeometry = -> [Sketch051]
  ExternalTypes = [0,0,0,0]
  FullyConstrained = true
  MakeInternals = false
  MapMode = 5
  Placement = pos=(0,-10.4,0) rot=(1,0,0;1.5708rad)
  expr: .AttachmentOffset.Base.z = -1 * VarSet.Base_connector_clip_height
  expr: .Placement.Base.y = -1 * (VarSet.Base_connector_height_lug - VarSet.Base_connector_clip_height)
  expr: Constraints[26] = VarSet.Base_connector_clip * 0.5
  sketch-geometry (14):
    g0: LineSegment [constr] StartX=-31.5 StartY=-16.5 StartZ=0 EndX=-23.5 EndY=-8.5 EndZ=0
    g1: LineSegment [constr] StartX=23.5 StartY=-16.5 StartZ=0 EndX=31.5 EndY=-8.5 EndZ=0
    g2: GeomPoint [constr] X=-27.5 Y=-12.5 Z=0
    g3: GeomPoint [constr] X=27.5 Y=-12.5 Z=0
    g4: LineSegment StartX=-29.5 StartY=-10.5 StartZ=0 EndX=-29.5 EndY=-14.5 EndZ=0
    g5: LineSegment StartX=-29.5 StartY=-14.5 StartZ=0 EndX=-25.5 EndY=-14.5 EndZ=0
    g6: LineSegment StartX=-25.5 StartY=-14.5 StartZ=0 EndX=-25.5 EndY=-10.5 EndZ=0
    g7: LineSegment StartX=-25.5 StartY=-10.5 StartZ=0 EndX=-29.5 EndY=-10.5 EndZ=0
    g8: GeomPoint [constr] X=-27.5 Y=-12.5 Z=0
    g9: LineSegment StartX=25.5 StartY=-10.5 StartZ=0 EndX=25.5 EndY=-14.5 EndZ=0
    g10: LineSegment StartX=25.5 StartY=-14.5 StartZ=0 EndX=29.5 EndY=-14.5 EndZ=0
    g11: LineSegment StartX=29.5 StartY=-14.5 StartZ=0 EndX=29.5 EndY=-10.5 EndZ=0
    g12: LineSegment StartX=29.5 StartY=-10.5 StartZ=0 EndX=25.5 EndY=-10.5 EndZ=0
    g13: GeomPoint [constr] X=27.5 Y=-12.5 Z=0
  constraints (30):
    c: Coincident(g0,g-3)
    c: Coincident(g0,g-4)
    c: Coincident(g1,g-5)
    c: Coincident(g1,g-6)
    c: Symmetric(g0,g0,g2)
    c: Symmetric(g1,g1,g3)
    c: Coincident(g4,g5)
    c: Coincident(g5,g6)
    c: Coincident(g6,g7)
    c: Coincident(g7,g4)
    c: Vertical(g4)
    c: Vertical(g6)
    c: Horizontal(g5)
    c: Horizontal(g7)
    c: Symmetric(g6,g4,g8)
    c: Coincident(g8,g2)
    c: Coincident(g9,g10)
    c: Coincident(g10,g11)
    c: Coincident(g11,g12)
    c: Coincident(g12,g9)
    c: Vertical(g9)
    c: Vertical(g11)
    c: Horizontal(g10)
    c: Horizontal(g12)
    c: Symmetric(g11,g9,g13)
    c: Coincident(g13,g3)
    c: DistanceX(g4,g6) = 4
    c: Equal(g7,g4)
    c: Equal(g4,g12)
    c: Equal(g12,g11)
FEATURE [PartDesign::SubtractiveLoft] SubtractiveLoft  label="clips_battery"
  BaseFeature = -> Fillet
  Closed = false
  Placement = pos=(0,0,0) rot=(1,0,0;1.5708rad)
  Profile = -> Sketch051
  Refine = true
  Ruled = false
  Sections = -> [Sketch052]
  Suppressed = false
FEATURE [Sketcher::SketchObject] Sketch053  label="oring_diameer"
  ArcFitTolerance = 1e-06
  AttachmentSupport = -> [XZ_Plane065]
  ExternalGeometry = -> [Sketch011]
  ExternalTypes = [0]
  FullyConstrained = true
  MakeInternals = false
  MapMode = 5
  Placement = pos=(0,0,0) rot=(1,0,0;1.5708rad)
  expr: Constraints[1] = VarSet.Base_connector_oring_outside_diameter - VarSet.Base_connector_oring_cross_section
  sketch-geometry (1):
    g0: Circle CenterX=0 CenterY=-12.5 CenterZ=0 NormalX=0 NormalY=0 NormalZ=1 AngleXU=0 Radius=9.5
  constraints (2):
    c: Coincident(g0,g-3)
    c: Diameter(g0) = 19
FEATURE [App::Point] Origin158
  Role = Origin
FEATURE [App::Point] Origin160
  Role = Origin
FEATURE [Sketcher::SketchObject] Sketch055
  ArcFitTolerance = 1e-06
  AttachmentSupport = -> [XY_Plane079]
  ExternalTypes = [0]
  FullyConstrained = false
  MakeInternals = false
  MapMode = 5
  expr: Constraints[0] = VarSet.Base_connector_oring_cross_section
  expr: Constraints[1] = (VarSet.Base_connector_oring_outside_diameter - VarSet.Base_connector_oring_cross_section) / 2
  expr: Constraints[4] = VarSet.Base_connector_oring_outside_diameter / 2
  sketch-geometry (2):
    g0: Circle CenterX=9.5 CenterY=0 CenterZ=0 NormalX=0 NormalY=0 NormalZ=1 AngleXU=0 Radius=1
    g1: LineSegment [constr] StartX=0 StartY=0 StartZ=0 EndX=10.5 EndY=0 EndZ=0
  constraints (5):
    c: Diameter(g0) = 2
    c: DistanceX(g-1,g0) = 9.5
    c: Coincident(g1,g-1)
    c: PointOnObject(g1,g-1)
    c: DistanceX(g1,g1) = 10.5
FEATURE [PartDesign::Revolution] Revolution002
  Angle = 360
  Angle2 = 60
  Axis = (0,1,0)
  Base = (0,0,0)
  Profile = -> Sketch055
  ReferenceAxis = -> Sketch055 [V_Axis]
  Refine = true
  Reversed = true
  Suppressed = false
  Type = 0
FEATURE [PartDesign::Body] Body013  label="oring001"
  AllowCompound = false
  Group = -> [Sketch055,Revolution002]
  Origin = -> Origin159
  Tip = -> Revolution002
FEATURE [App::Part] Part008  label="oring"
  Group = -> [Body013]
  Origin = -> Origin157
FEATURE [Sketcher::SketchObject] Sketch056  label="cross_section"
  ArcFitTolerance = 1e-06
  AttacherType = Attacher::AttachEngine3D
  AttachmentSupport = -> [SubtractiveLoft]
  ExternalTypes = [0]
  FullyConstrained = true
  MakeInternals = false
  MapMode = 5
  Placement = pos=(0,-12,0) rot=(1,0,0;1.5708rad)
  expr: Constraints[1] = VarSet.case_height / 2
  expr: Constraints[3] = VarSet.Base_connector_oring_outside_diameter - VarSet.Base_connector_oring_cross_section
  sketch-geometry (2):
    g0: GeomPoint X=0 Y=-12.5 Z=0
    g1: Circle CenterX=0 CenterY=-12.5 CenterZ=0 NormalX=0 NormalY=0 NormalZ=1 AngleXU=0 Radius=9.5
  constraints (4):
    c: PointOnObject(g0,g-2)
    c: DistanceY(g0,g-1) = 12.5
    c: Coincident(g1,g0)
    c: Diameter(g1) = 19
FEATURE [Sketcher::SketchObject] Sketch058  label="_oring_diameter"
  ArcFitTolerance = 1e-06
  AttachmentSupport = -> [YZ_Plane066]
  ExternalGeometry = -> [Sketch056]
  ExternalTypes = [0]
  FullyConstrained = false
  MakeInternals = false
  MapMode = 5
  Placement = pos=(0,0,0) rot=(0.57735,0.57735,0.57735;2.0944rad)
  expr: Constraints[0] = VarSet.Base_connector_oring_cross_section
  expr: Constraints[4] = VarSet.Base_connector_oring_offset
  sketch-geometry (2):
    g0: Circle CenterX=-12.2 CenterY=-3 CenterZ=0 NormalX=0 NormalY=0 NormalZ=1 AngleXU=0 Radius=1
    g1: LineSegment [constr] StartX=-16.3675 StartY=-3 StartZ=0 EndX=-7.63249 EndY=-3 EndZ=0
  constraints (5):
    c: Diameter(g0) = 2
    c: PointOnObject(g-3,g1)
    c: PointOnObject(g0,g1)
    c: Symmetric(g1,g1,g-3)
    c: Distance(g0,g-3) = 0.2
FEATURE [Sketcher::SketchObject] Sketch060  label="cross_section001"
  ArcFitTolerance = 1e-06
  AttachmentSupport = -> [YZ_Plane065]
  ExternalGeometry = -> [Sketch053]
  ExternalTypes = [0]
  FullyConstrained = true
  MakeInternals = false
  MapMode = 5
  Placement = pos=(0,0,0) rot=(0.57735,0.57735,0.57735;2.0944rad)
  expr: Constraints[0] = VarSet.Base_connector_oring_cross_section
  expr: Constraints[5] = VarSet.Base_connector_oring_offset
  sketch-geometry (2):
    g0: Circle CenterX=-0.2 CenterY=-3 CenterZ=0 NormalX=0 NormalY=0 NormalZ=1 AngleXU=0 Radius=1
    g1: LineSegment [constr] StartX=-5 StartY=-3 StartZ=0 EndX=5 EndY=-3 EndZ=0
  constraints (6):
    c: Diameter(g0) = 2
    c: Distance(g1) = 10
    c: Symmetric(g1,g1,g-2)
    c: PointOnObject(g0,g1)
    c: PointOnObject(g-3,g1)
    c: DistanceX(g0,g-3) = 0.2
FEATURE [PartDesign::SubtractivePipe] SubtractivePipe005  label="oring_grove"
  AuxilleryCurvelinear = true
  AuxillerySpineTangent = false
  BaseFeature = -> AdditiveLoft
  Binormal = (0,0,0)
  Mode = 0
  Placement = pos=(0,0,0) rot=(1,0,0;1.5708rad)
  Profile = -> Sketch060
  Refine = true
  Spine = -> Sketch053
  SpineTangent = false
  Suppressed = false
  Transformation = 0
  Transition = 0
FEATURE [App::Link] oring  label="oring002"
  LinkPlacement = pos=(3e-15,-12.2,-12.5) rot=(0,1,0;3.14159rad)
  LinkedObject = -> Part008
  Placement = pos=(3e-15,-12.2,-12.5) rot=(0,1,0;3.14159rad)
FEATURE [PartDesign::Fillet] Fillet002
  Base = -> SubtractivePipe005 [Edge67,Edge71,Edge60,Edge58,Edge65,Edge63,Edge62,Edge69,Edge51,Edge57]
  BaseFeature = -> SubtractivePipe005
  Placement = pos=(0,0,0) rot=(1,0,0;1.5708rad)
  Radius = 1
  Refine = true
  SupportTransform = false
  Suppressed = false
  UseAllEdges = false
FEATURE [PartDesign::Body] Body005  label="battery_connector"
  AllowCompound = false
  Group = -> [Sketch011,Pad008,Pad009,Sketch012,Pocket012,Sketch018,Pocket016,Sketch043,Pocket027,Sketch048,Sketch049,AdditiveLoft,Sketch053,Sketch060,SubtractivePipe005,Fillet002]
  Origin = -> Origin131
  Placement = pos=(0,-1.5,0) rot=(0,0,1;0rad)
  Tip = -> Fillet002
  expr: .Placement.Base.y = -1 * VarSet.Base_pogopin_cutout_height
FEATURE [Sketcher::SketchObject] Sketch061  label="pogopins001"
  ArcFitTolerance = 1e-06
  ExternalTypes = [0]
  FullyConstrained = true
  MakeInternals = false
  MapMode = 5
  Placement = pos=(0,0,0) rot=(1,0,0;1.5708rad)
  expr: Constraints[10] = VarSet.case_height / 2
  expr: Constraints[11] = VarSet.Base_pogoping_lenght
  expr: Constraints[12] = 2 * VarSet.Base_pogopins_r
  sketch-geometry (7):
    g0: LineSegment [constr] StartX=-7.55 StartY=-10.4 StartZ=0 EndX=-7.55 EndY=-14.6 EndZ=0
    g1: LineSegment StartX=-7.55 StartY=-14.6 StartZ=0 EndX=7.55 EndY=-14.6 EndZ=0
    g2: LineSegment [constr] StartX=7.55 StartY=-14.6 StartZ=0 EndX=7.55 EndY=-10.4 EndZ=0
    g3: LineSegment StartX=7.55 StartY=-10.4 StartZ=0 EndX=-7.55 EndY=-10.4 EndZ=0
    g4: GeomPoint [constr] X=0 Y=-12.5 Z=0
    g5: ArcOfCircle CenterX=7.55 CenterY=-12.5 CenterZ=0 NormalX=0 NormalY=0 NormalZ=1 AngleXU=0 Radius=2.1 StartAngle=4.71239 EndAngle=7.85398
    g6: ArcOfCircle CenterX=-7.55 CenterY=-12.5 CenterZ=0 NormalX=0 NormalY=0 NormalZ=1 AngleXU=0 Radius=2.1 StartAngle=1.5708 EndAngle=4.71239
  constraints (19):
    c: Coincident(g0,g1)
    c: Coincident(g1,g2)
    c: Coincident(g2,g3)
    c: Coincident(g3,g0)
    c: Vertical(g0)
    c: Vertical(g2)
    c: Horizontal(g1)
    c: Horizontal(g3)
    c: Symmetric(g2,g0,g4)
    c: PointOnObject(g4,g-2)
    c: DistanceY(g4,g-1) = 12.5
    c: Distance(g0,g2) = 15.1
    c: DistanceY(g1,g2) = 4.2
    c: Symmetric(g0,g0,g6)
    c: Coincident(g6,g0)
    c: Coincident(g6,g0)
    c: Coincident(g5,g1)
    c: Coincident(g5,g2)
    c: PointOnObject(g5,g2)
FEATURE [Sketcher::SketchObject] Sketch062  label="nuts001"
  ArcFitTolerance = 1e-06
  AttachmentOffset = pos=(0,0,-25) rot=(0,0,1;0rad)
  AttachmentSupport = -> [XY_Plane058]
  ExternalTypes = [0]
  FullyConstrained = true
  MakeInternals = false
  MapMode = 5
  Placement = pos=(0,0,-25) rot=(0,0,1;0rad)
  expr: .AttachmentOffset.Base.z = -1 * VarSet.case_height
  expr: Constraints[10] = VarSet.Base_battery_lenght - 2 * 3.6 mm
  expr: Constraints[8] = VarSet.base_width - 2 * 3.6 mm
  sketch-geometry (32):
    g0: LineSegment [constr] StartX=-28.9 StartY=81.4 StartZ=0 EndX=-28.9 EndY=3.6 EndZ=0
    g1: LineSegment [constr] StartX=-28.9 StartY=3.6 StartZ=0 EndX=28.9 EndY=3.6 EndZ=0
    g2: LineSegment [constr] StartX=28.9 StartY=3.6 StartZ=0 EndX=28.9 EndY=81.4 EndZ=0
    g3: LineSegment [constr] StartX=28.9 StartY=81.4 StartZ=0 EndX=-28.9 EndY=81.4 EndZ=0
    g4: LineSegment StartX=-25.7246 StartY=81.4 StartZ=0 EndX=-27.3123 EndY=84.15 EndZ=0
    g5: LineSegment StartX=-27.3123 StartY=84.15 StartZ=0 EndX=-30.4877 EndY=84.15 EndZ=0
    g6: LineSegment StartX=-30.4877 StartY=84.15 StartZ=0 EndX=-32.0754 EndY=81.4 EndZ=0
    g7: LineSegment StartX=-32.0754 StartY=81.4 StartZ=0 EndX=-30.4877 EndY=78.65 EndZ=0
    g8: LineSegment StartX=-30.4877 StartY=78.65 StartZ=0 EndX=-27.3123 EndY=78.65 EndZ=0
    g9: LineSegment StartX=-27.3123 StartY=78.65 StartZ=0 EndX=-25.7246 EndY=81.4 EndZ=0
    g10: Circle [constr] CenterX=-28.9 CenterY=81.4 CenterZ=0 NormalX=0 NormalY=0 NormalZ=1 AngleXU=0 Radius=3.17543
    g11: LineSegment StartX=32.0754 StartY=81.4 StartZ=0 EndX=30.4877 EndY=84.15 EndZ=0
    g12: LineSegment StartX=30.4877 StartY=84.15 StartZ=0 EndX=27.3123 EndY=84.15 EndZ=0
    g13: LineSegment StartX=27.3123 StartY=84.15 StartZ=0 EndX=25.7246 EndY=81.4 EndZ=0
    g14: LineSegment StartX=25.7246 StartY=81.4 StartZ=0 EndX=27.3123 EndY=78.65 EndZ=0
    g15: LineSegment StartX=27.3123 StartY=78.65 StartZ=0 EndX=30.4877 EndY=78.65 EndZ=0
    g16: LineSegment StartX=30.4877 StartY=78.65 StartZ=0 EndX=32.0754 EndY=81.4 EndZ=0
    g17: Circle [constr] CenterX=28.9 CenterY=81.4 CenterZ=0 NormalX=0 NormalY=0 NormalZ=1 AngleXU=0 Radius=3.17543
    g18: LineSegment StartX=30.4877 StartY=6.35 StartZ=0 EndX=27.3123 EndY=6.35 EndZ=0
    g19: LineSegment StartX=27.3123 StartY=6.35 StartZ=0 EndX=25.7246 EndY=3.6 EndZ=0
    g20: LineSegment StartX=25.7246 StartY=3.6 StartZ=0 EndX=27.3123 EndY=0.85 EndZ=0
    g21: LineSegment StartX=27.3123 StartY=0.85 StartZ=0 EndX=30.4877 EndY=0.85 EndZ=0
    g22: LineSegment StartX=30.4877 StartY=0.85 StartZ=0 EndX=32.0754 EndY=3.6 EndZ=0
    g23: LineSegment StartX=32.0754 StartY=3.6 StartZ=0 EndX=30.4877 EndY=6.35 EndZ=0
    g24: Circle [constr] CenterX=28.9 CenterY=3.6 CenterZ=0 NormalX=0 NormalY=0 NormalZ=1 AngleXU=0 Radius=3.17543
    g25: LineSegment StartX=-30.4877 StartY=0.85 StartZ=0 EndX=-27.3123 EndY=0.85 EndZ=0
    g26: LineSegment StartX=-27.3123 StartY=0.85 StartZ=0 EndX=-25.7246 EndY=3.6 EndZ=0
    g27: LineSegment StartX=-25.7246 StartY=3.6 StartZ=0 EndX=-27.3123 EndY=6.35 EndZ=0
    g28: LineSegment StartX=-27.3123 StartY=6.35 StartZ=0 EndX=-30.4877 EndY=6.35 EndZ=0
    g29: LineSegment StartX=-30.4877 StartY=6.35 StartZ=0 EndX=-32.0754 EndY=3.6 EndZ=0
    g30: LineSegment StartX=-32.0754 StartY=3.6 StartZ=0 EndX=-30.4877 EndY=0.85 EndZ=0
    g31: Circle [constr] CenterX=-28.9 CenterY=3.6 CenterZ=0 NormalX=0 NormalY=0 NormalZ=1 AngleXU=0 Radius=3.17543
  constraints (75):
    c: Coincident(g0,g1)
    c: Coincident(g1,g2)
    c: Coincident(g2,g3)
    c: Coincident(g3,g0)
    c: Vertical(g0)
    c: Vertical(g2)
    c: Horizontal(g1)
    c: Symmetric(g0,g2,g-2)
    c: DistanceX(g0,g2) = 57.8
    c: Distance(g1,g-1) = 3.6
    c: DistanceY(g1,g2) = 77.8
    c: Coincident(g4,g5)
    c: Coincident(g5,g6)
    c: Coincident(g6,g7)
    c: Coincident(g7,g8)
    c: Coincident(g8,g9)
    c: Coincident(g9,g4)
    c: Equal(g4, g5-g9) x5
    c: PointOnObject(g4,g10)
    c: PointOnObject(g5,g10)
    c: PointOnObject(g6,g10)
    c: PointOnObject(g7,g10)
    c: PointOnObject(g8,g10)
    c: PointOnObject(g9,g10)
    c: Coincident(g10,g0)
    c: PointOnObject(g9,g3)
    c: Coincident(g11,g12)
    c: Coincident(g12,g13)
    c: Coincident(g13,g14)
    c: Coincident(g14,g15)
    c: Coincident(g15,g16)
    c: Coincident(g16,g11)
    c: Equal(g11, g12-g16) x5
    c: PointOnObject(g11,g17)
    c: PointOnObject(g12,g17)
    c: PointOnObject(g13,g17)
    c: PointOnObject(g14,g17)
    c: PointOnObject(g15,g17)
    c: PointOnObject(g16,g17)
    c: Coincident(g17,g2)
    c: Coincident(g18,g19)
    c: Coincident(g19,g20)
    c: Coincident(g20,g21)
    c: Coincident(g21,g22)
    c: Coincident(g22,g23)
    c: Coincident(g23,g18)
    c: Equal(g18, g19-g23) x5
    c: PointOnObject(g18,g24)
    c: PointOnObject(g19,g24)
    c: PointOnObject(g20,g24)
    c: PointOnObject(g21,g24)
    c: PointOnObject(g22,g24)
    c: PointOnObject(g23,g24)
    c: Coincident(g24,g1)
    c: Coincident(g25,g26)
    c: Coincident(g26,g27)
    c: Coincident(g27,g28)
    c: Coincident(g28,g29)
    c: Coincident(g29,g30)
    c: Coincident(g30,g25)
    c: Equal(g25, g26-g30) x5
    c: PointOnObject(g25,g31)
    c: PointOnObject(g26,g31)
    c: PointOnObject(g27,g31)
    c: PointOnObject(g28,g31)
    c: PointOnObject(g29,g31)
    c: PointOnObject(g30,g31)
    c: Parallel(g-1,g21)
    c: Parallel(g15,g-1)
    c: Equal(g10,g17)
    c: Equal(g31,g24)
    c: DistanceY(g7,g5) = 5.5
    c: Coincident(g31,g0)
    c: Parallel(g25,g-1)
    c: Equal(g10,g31)
FEATURE [PartDesign::Pocket] Pocket030  label="nuts_"
  BaseFeature = -> SubtractivePipe001
  Direction = (0,0,-1)
  Length = 20
  Length2 = 5
  Midplane = true
  Profile = -> Sketch062
  ReferenceAxis = -> Sketch062 [N_Axis]
  Refine = true
  Suppressed = false
  Type = 0
  expr: Length = VarSet.case_height * 0.8
FEATURE [PartDesign::LinearPattern] LinearPattern
  BaseFeature = -> Pocket030
  Direction = -> Sketch007 [N_Axis]
  Length = 50
  Mode = 0
  Occurrences = 3
  Offset = 25
  Originals = -> [Pad005]
  Refine = true
  Reversed = true
  Suppressed = false
  TransformMode = 0
FEATURE [PartDesign::Body] Body002  label="battery_body"
  AllowCompound = false
  Group = -> [Sketch006,Pad004,Pocket005,Pocket006,Sketch007,Pad005,Sketch022,Pocket020,Sketch033,SubtractivePipe001,Sketch061,Sketch062,Pocket030,LinearPattern]
  Origin = -> Origin116
  Tip = -> LinearPattern
FEATURE [App::Part] Part002  label="battery"
  Group = -> [Body002,Body005]
  Origin = -> Origin114
FEATURE [App::FeaturePython] Joint020  label="pogopins_battery"  # Assembly joint (typed FeaturePython)
  Activated = true
  AngleMax = 0
  AngleMin = 0
  Detach1 = false
  Detach2 = false
  Distance = 0
  Distance2 = 0
  EnableAngleMax = false
  EnableAngleMin = false
  EnableLengthMax = false
  EnableLengthMin = false
  JointType = 0 (Fixed)
  LengthMax = 0
  LengthMin = 0
  Offset2 = pos=(0,0,0) rot=(0,0,-1;1.5708rad)
  Placement1 = pos=(-5.5,2.8,0) rot=(0.57735,0.57735,0.57735;4.18879rad)
  Placement2 = pos=(-5.45,0.75,-12.5) rot=(0.57735,0.57735,-0.57735;2.0944rad)
  Reference1 = -> Assembly [Magnetic_Pogo_Connector_3_Pin__Type_1_006.Part__Feature.Face3,Magnetic_Pogo_Connector_3_Pin__Type_1_006.Part__Feature.Face3]
  Reference2 = -> Assembly [battery.Body005.Face48,battery.Body005.Face48]
FEATURE [PartDesign::SubtractivePipe] SubtractivePipe006
  AuxilleryCurvelinear = true
  AuxillerySpineTangent = false
  BaseFeature = -> SubtractiveLoft
  Binormal = (0,0,0)
  Mode = 0
  Placement = pos=(0,0,0) rot=(1,0,0;1.5708rad)
  Profile = -> Sketch058
  Refine = true
  Spine = -> Sketch056 [Edge1]
  SpineTangent = false
  Suppressed = false
  Transformation = 0
  Transition = 0
FEATURE [PartDesign::Fillet] Fillet003
  Base = -> SubtractivePipe006 [Edge62,Edge49,Edge87,Edge45,Edge56,Edge53,Edge64,Edge51]
  BaseFeature = -> SubtractivePipe006
  Placement = pos=(0,0,0) rot=(1,0,0;1.5708rad)
  Radius = 1
  Refine = true
  SupportTransform = false
  Suppressed = false
  UseAllEdges = false
FEATURE [PartDesign::Body] Body006  label="main_connector001"
  AllowCompound = false
  Group = -> [Sketch013,Sketch014,Sketch016,Sketch017,Pad010,Pocket021,Pocket022,Pocket023,Sketch023,Pocket024,Fillet,Sketch051,Sketch052,SubtractiveLoft,Sketch056,Sketch058,SubtractivePipe006,Fillet003]
  Origin = -> Origin133
  Placement = pos=(3.1e-15,0,-25) rot=(0,1,0;3.14159rad)
  Tip = -> Fillet003
FEATURE [Sketcher::SketchObject] Sketch063  label="strap"
  ArcFitTolerance = 1e-06
  AttachmentOffset = pos=(0,0,-25) rot=(0,0,1;0rad)
  AttachmentSupport = -> [XY_Plane053]
  ExternalTypes = [0]
  FullyConstrained = true
  MakeInternals = false
  MapMode = 5
  Placement = pos=(0,0,-25) rot=(0,0,1;0rad)
  expr: .AttachmentOffset.Base.z = -1 * VarSet.case_height
  expr: Constraints[10] = VarSet.Base_base_lenght
  expr: Constraints[9] = VarSet.base_width
  sketch-geometry (20):
    g0: LineSegment [constr] StartX=-32.5 StartY=0 StartZ=0 EndX=32.5 EndY=0 EndZ=0
    g1: LineSegment [constr] StartX=32.5 StartY=0 StartZ=0 EndX=32.5 EndY=55 EndZ=0
    g2: LineSegment [constr] StartX=32.5 StartY=55 StartZ=0 EndX=-32.5 EndY=55 EndZ=0
    g3: LineSegment [constr] StartX=-32.5 StartY=55 StartZ=0 EndX=-32.5 EndY=0 EndZ=0
    g4: LineSegment StartX=-7 StartY=55 StartZ=0 EndX=-7 EndY=59 EndZ=0
    g5: LineSegment StartX=-10 StartY=62 StartZ=0 EndX=-23 EndY=62 EndZ=0
    g6: LineSegment StartX=-26 StartY=59 StartZ=0 EndX=-26 EndY=55 EndZ=0
    g7: LineSegment StartX=-9 StartY=55 StartZ=0 EndX=-9 EndY=57 EndZ=0
    g8: LineSegment StartX=-12 StartY=60 StartZ=0 EndX=-21 EndY=60 EndZ=0
    g9: LineSegment StartX=-24 StartY=57 StartZ=0 EndX=-24 EndY=55 EndZ=0
    g10: ArcOfCircle CenterX=-23 CenterY=59 CenterZ=0 NormalX=0 NormalY=0 NormalZ=1 AngleXU=0 Radius=3 StartAngle=1.5708 EndAngle=3.14159
    g11: GeomPoint [constr] X=-26 Y=62 Z=0
    g12: ArcOfCircle CenterX=-21 CenterY=57 CenterZ=0 NormalX=0 NormalY=0 NormalZ=1 AngleXU=0 Radius=3 StartAngle=1.5708 EndAngle=3.14159
    g13: GeomPoint [constr] X=-24 Y=60 Z=0
    g14: ArcOfCircle CenterX=-12 CenterY=57 CenterZ=0 NormalX=0 NormalY=0 NormalZ=1 AngleXU=0 Radius=3 StartAngle=2e-16 EndAngle=1.5708
    g15: GeomPoint [constr] X=-9 Y=60 Z=0
    g16: ArcOfCircle CenterX=-10 CenterY=59 CenterZ=0 NormalX=0 NormalY=0 NormalZ=1 AngleXU=0 Radius=3 StartAngle=-9e-16 EndAngle=1.5708
    g17: GeomPoint [constr] X=-7 Y=62 Z=0
    g18: LineSegment StartX=-26 StartY=55 StartZ=0 EndX=-24 EndY=55 EndZ=0
    g19: LineSegment StartX=-9 StartY=55 StartZ=0 EndX=-7 EndY=55 EndZ=0
  constraints (51):
    c: Coincident(g0,g1)
    c: Coincident(g1,g2)
    c: Coincident(g2,g3)
    c: Coincident(g3,g0)
    c: Horizontal(g0)
    c: Vertical(g1)
    c: Vertical(g3)
    c: PointOnObject(g0,g-1)
    c: Symmetric(g2,g1,g-2)
    c: DistanceX(g2,g1) = 65
    c: DistanceY(g-1,g1) = 55
    c: Horizontal(g5)
    c: Vertical(g4)
    c: Vertical(g6)
    c: PointOnObject(g6,g2)
    c: Horizontal(g8)
    c: Vertical(g7)
    c: Vertical(g9)
    c: PointOnObject(g11,g6)
    c: PointOnObject(g11,g5)
    c: Tangent(g6,g10) = -1.5708
    c: Tangent(g5,g10) = -1.5708
    c: PointOnObject(g13,g9)
    c: PointOnObject(g13,g8)
    c: Tangent(g9,g12) = -1.5708
    c: Tangent(g8,g12) = -1.5708
    c: PointOnObject(g15,g7)
    c: PointOnObject(g15,g8)
    c: Tangent(g7,g14) = -1.5708
    c: Tangent(g8,g14) = -1.5708
    c: PointOnObject(g17,g5)
    c: PointOnObject(g17,g4)
    c: Tangent(g5,g16) = -1.5708
    c: Tangent(g4,g16) = -1.5708
    c: Equal(g10,g16)
    c: Equal(g12,g14)
    c: Distance(g6,g9) = 2
    c: Coincident(g18,g6)
    c: Coincident(g18,g9)
    c: Horizontal(g18)
    c: Coincident(g19,g7)
    c: Coincident(g19,g4)
    c: Horizontal(g19)
    c: Equal(g18,g19)
    c: Radius(g10) = 3
    c: Equal(g10,g12)
    c: Distance(g5,g8) = 2
    c: DistanceX(g9,g7) = 15
    c: Distance(g16,g2) = 4
    c: DistanceX(g4,g-1) = 7
    c: PointOnObject(g4,g2)
FEATURE [PartDesign::Pad] Pad022  label="strap001"
  BaseFeature = -> Pocket029
  Direction = (0,0,1)
  Length = 5
  Length2 = 10
  Profile = -> Sketch063
  ReferenceAxis = -> Sketch063 [N_Axis]
  Refine = true
  Suppressed = false
  Type = 0
FEATURE [Sketcher::SketchObject] Sketch064  label="on_off_grard_text"
  ArcFitTolerance = 1e-06
  AttachmentSupport = -> [XY_Plane053]
  ExternalTypes = [0,0]
  FullyConstrained = true
  MakeInternals = false
  MapMode = 5
  sketch-geometry (8):
    g0: LineSegment StartX=-3.99111 StartY=67.5 StartZ=0 EndX=-3.99111 EndY=57.5 EndZ=0
    g1: LineSegment StartX=-3.99111 StartY=57.5 StartZ=0 EndX=-1.99111 EndY=57.5 EndZ=0
    g2: LineSegment StartX=-1.99111 StartY=57.5 StartZ=0 EndX=-1.99111 EndY=67.5 EndZ=0
    g3: LineSegment StartX=-1.99111 StartY=67.5 StartZ=0 EndX=-3.99111 EndY=67.5 EndZ=0
    g4: GeomPoint [constr] X=-2.99111 Y=62.5 Z=0
    g5: GeomPoint X=-5.99111 Y=62.5 Z=0
    g6: GeomPoint X=8.00889 Y=62.5 Z=0
    g7: LineSegment [constr] StartX=-5.99111 StartY=62.5 StartZ=0 EndX=8.00889 EndY=62.5 EndZ=0
  constraints (17):
    c: Coincident(g0,g1)
    c: Coincident(g1,g2)
    c: Coincident(g2,g3)
    c: Coincident(g3,g0)
    c: Vertical(g0)
    c: Vertical(g2)
    c: Horizontal(g1)
    c: Horizontal(g3)
    c: Symmetric(g2,g0,g4)
    c: DistanceY(g0,g0) = 10
    c: DistanceX(g0,g2) = 2
    c: Symmetric(g-3,g-3,g5)
    c: Symmetric(g-4,g-4,g6)
    c: Coincident(g7,g5)
    c: Coincident(g7,g6)
    c: PointOnObject(g4,g7)
    c: Distance(g5,g0) = 2
FEATURE [PartDesign::Pocket] Pocket031  label="on_off_grard_text001"
  BaseFeature = -> Pad022
  Direction = (0,0,-1)
  Length = 0.4
  Length2 = 5
  Profile = -> Sketch064
  ReferenceAxis = -> Sketch064 [N_Axis]
  Refine = true
  Suppressed = false
  Type = 0
FEATURE [PartDesign::SubtractivePipe] SubtractivePipe003
  AuxilleryCurvelinear = true
  AuxillerySpineTangent = false
  BaseFeature = -> Hole001
  Binormal = (0,0,0)
  Mode = 0
  Profile = -> Sketch038
  Refine = true
  Spine = -> Sketch037 [Edge7,Edge6,Edge5,Edge4,Edge3,Edge2,Edge1,Edge16,Edge15,Edge14,Edge13,Edge12,Edge11,Edge10,Edge9,Edge8]
  SpineTangent = false
  Suppressed = false
  Transformation = 0
  Transition = 0
FEATURE [App::Link] mainbody_cover001  label="mainbody_cover002"
  LinkPlacement = pos=(-1.9e-15,-6e-16,1e-16) rot=(0,0,1;0rad)
  LinkedObject = -> Body007
  Placement = pos=(-1.9e-15,-6e-16,1e-16) rot=(0,0,1;0rad)
FEATURE [Sketcher::SketchObject] Sketch065  label="ble_antenna"
  ArcFitTolerance = 1e-06
  AttachmentOffset = pos=(0,0,-25) rot=(0,0,1;0rad)
  AttachmentSupport = -> [XY_Plane053]
  ExternalTypes = [0]
  FullyConstrained = true
  MakeInternals = false
  MapMode = 5
  Placement = pos=(0,0,-25) rot=(0,0,1;0rad)
  expr: .AttachmentOffset.Base.z = -VarSet.case_height
  expr: Constraints[3] = VarSet.base_width / 2 - 2.2 * VarSet.Base_case_thickness
  sketch-geometry (17):
    g0: LineSegment [constr] StartX=25.9 StartY=0 StartZ=0 EndX=25.9 EndY=60 EndZ=0
    g1: LineSegment StartX=25.9 StartY=45.5 StartZ=0 EndX=25.9 EndY=48.5 EndZ=0
    g2: LineSegment StartX=25.9 StartY=48.5 StartZ=0 EndX=20.9 EndY=48.5 EndZ=0
    g3: LineSegment StartX=20.9 StartY=48.5 StartZ=0 EndX=20.9 EndY=45.5 EndZ=0
    g4: LineSegment StartX=20.9 StartY=45.5 StartZ=0 EndX=22.4 EndY=45.5 EndZ=0
    g5: LineSegment StartX=22.4 StartY=45.5 StartZ=0 EndX=22.4 EndY=47 EndZ=0
    g6: LineSegment StartX=22.4 StartY=47 StartZ=0 EndX=24.4 EndY=47 EndZ=0
    g7: LineSegment StartX=24.4 StartY=47 StartZ=0 EndX=24.4 EndY=45.5 EndZ=0
    g8: LineSegment StartX=24.4 StartY=45.5 StartZ=0 EndX=25.9 EndY=45.5 EndZ=0
    g9: LineSegment StartX=25.9 StartY=8 StartZ=0 EndX=25.9 EndY=5 EndZ=0
    g10: LineSegment StartX=25.9 StartY=5 StartZ=0 EndX=20.9 EndY=5 EndZ=0
    g11: LineSegment StartX=20.9 StartY=5 StartZ=0 EndX=20.9 EndY=8 EndZ=0
    g12: LineSegment StartX=20.9 StartY=8 StartZ=0 EndX=22.4 EndY=8 EndZ=0
    g13: LineSegment StartX=22.4 StartY=8 StartZ=0 EndX=22.4 EndY=6.5 EndZ=0
    g14: LineSegment StartX=22.4 StartY=6.5 StartZ=0 EndX=24.4 EndY=6.5 EndZ=0
    g15: LineSegment StartX=24.4 StartY=6.5 StartZ=0 EndX=24.4 EndY=8 EndZ=0
    g16: LineSegment StartX=24.4 StartY=8 StartZ=0 EndX=25.9 EndY=8 EndZ=0
  constraints (52):
    c: Distance(g0) = 60
    c: Vertical(g0)
    c: PointOnObject(g0,g-1)
    c: Distance(g0,g-2) = 25.9
    c: Vertical(g1)
    c: Coincident(g1,g2)
    c: Horizontal(g2)
    c: Coincident(g2,g3)
    c: Vertical(g3)
    c: Coincident(g3,g4)
    c: Horizontal(g4)
    c: Coincident(g4,g5)
    c: Coincident(g5,g6)
    c: Horizontal(g6)
    c: Coincident(g6,g7)
    c: Vertical(g7)
    c: Coincident(g7,g8)
    c: Coincident(g1,g8)
    c: Perpendicular(g1,g8)
    c: DistanceX(g5,g6) = 2
    c: Perpendicular(g4,g5)
    c: DistanceY(g3,g2) = 3
    c: Distance(g4,g3) = 1.5
    c: Equal(g4,g5)
    c: Equal(g5,g7)
    c: Equal(g7,g8)
    c: PointOnObject(g1,g0)
    c: PointOnObject(g9,g0)
    c: PointOnObject(g9,g0)
    c: Coincident(g9,g10)
    c: Horizontal(g10)
    c: Coincident(g10,g11)
    c: Vertical(g11)
    c: Coincident(g11,g12)
    c: Horizontal(g12)
    c: Coincident(g12,g13)
    c: Vertical(g13)
    c: Coincident(g13,g14)
    c: Horizontal(g14)
    c: Coincident(g14,g15)
    c: Coincident(g15,g16)
    c: Coincident(g16,g9)
    c: Horizontal(g16)
    c: Parallel(g15,g0)
    c: Equal(g6,g14)
    c: Equal(g4,g12)
    c: Equal(g12,g13)
    c: Equal(g13,g15)
    c: Equal(g15,g16)
    c: Equal(g3,g11)
    c: DistanceY(g14,g6) = 40.5
    c: Distance(g9,g-1) = 5
FEATURE [PartDesign::Pad] Pad023  label="ble_antenna001"
  BaseFeature = -> Pocket031
  Direction = (0,0,1)
  Length = 12
  Length2 = 10
  Profile = -> Sketch065
  ReferenceAxis = -> Sketch065 [N_Axis]
  Refine = true
  Suppressed = false
  Type = 0
FEATURE [Sketcher::SketchObject] Sketch066  label="water_dranage"
  ArcFitTolerance = 1e-06
  AttachmentSupport = -> [XY_Plane053]
  ExternalGeometry = -> [Pad023]
  ExternalTypes = [0]
  FullyConstrained = true
  MakeInternals = false
  MapMode = 5
  sketch-geometry (3):
    g0: ArcOfCircle CenterX=17 CenterY=55 CenterZ=0 NormalX=0 NormalY=0 NormalZ=1 AngleXU=0 Radius=1 StartAngle=1.61e-14 EndAngle=3.14159
    g1: LineSegment StartX=16 StartY=55 StartZ=0 EndX=18 EndY=55 EndZ=0
    g2: GeomPoint X=17 Y=55 Z=0
  constraints (7):
    c: Coincident(g1,g0)
    c: Coincident(g1,g0)
    c: Horizontal(g1)
    c: PointOnObject(g0,g1)
    c: Symmetric(g-3,g-3,g2)
    c: Coincident(g0,g2)
    c: Radius(g0) = 1
FEATURE [PartDesign::Pocket] Pocket032  label="water_dranage001"
  BaseFeature = -> Pad023
  Direction = (0,0,-1)
  Length = 16
  Length2 = 5
  Profile = -> Sketch066
  ReferenceAxis = -> Sketch066 [N_Axis]
  Refine = true
  Suppressed = false
  Type = 0
FEATURE [PartDesign::PolarPattern] PolarPattern  label="water_dranage002"
  Angle = 360
  Axis = -> Pocket032 [Edge443]
  BaseFeature = -> Pocket032
  Mode = 0
  Occurrences = 3
  Offset = 120
  Originals = -> [Pocket032]
  Refine = true
  Suppressed = false
  TransformMode = 0
FEATURE [PartDesign::Fillet] Fillet004
  Base = -> SubtractivePipe003 [Edge4,Edge10,Edge7,Edge35,Edge36,Edge34]
  BaseFeature = -> SubtractivePipe003
  Radius = 1
  Refine = true
  SupportTransform = false
  Suppressed = false
  UseAllEdges = false
FEATURE [PartDesign::Pocket] Pocket033
  BaseFeature = -> Fillet004
  Direction = (0,0,-1)
  Length = 0.6
  Length2 = 5
  Profile = -> Sketch039
  ReferenceAxis = -> Sketch039 [N_Axis]
  Refine = true
  Suppressed = false
  Type = 0
  expr: Length = 0.2 * VarSet.Base_case_thickness
FEATURE [PartDesign::Body] Body011  label="battery_cover001"
  AllowCompound = false
  Group = -> [Sketch030,Binder003,Pad013,Sketch036,Hole001,Sketch037,Sketch038,SubtractivePipe003,Sketch039,Fillet004,Pocket033]
  Origin = -> Origin151
  Tip = -> Pocket033
FEATURE [App::Part] Part006  label="battery_cover"
  Group = -> [Body011]
  Origin = -> Origin149
FEATURE [Sketcher::SketchObject] Sketch067  label="seses"
  ArcFitTolerance = 1e-06
  AttachmentSupport = -> [XY_Plane070]
  ExternalGeometry = -> [Binder001]
  ExternalTypes = [0,0,0,0,0,0,0,0]
  FullyConstrained = true
  MakeInternals = false
  MapMode = 5
FEATURE [PartDesign::Pocket] Pocket034
  BaseFeature = -> SubtractivePipe002
  Direction = (0,0,-1)
  Length = 0.6
  Length2 = 5
  Profile = -> Sketch067
  ReferenceAxis = -> Sketch067 [N_Axis]
  Refine = true
  Reversed = true
  Suppressed = false
  Type = 0
  expr: Length = 0.2 * VarSet.Base_case_thickness
FEATURE [PartDesign::Fillet] Fillet005
  Base = -> Pocket034 [Edge4,Edge7,Edge34,Edge35,Edge10,Edge36]
  BaseFeature = -> Pocket034
  Radius = 1
  Refine = true
  SupportTransform = false
  Suppressed = false
  UseAllEdges = false
FEATURE [PartDesign::Body] Body007  label="mainbody_cover001"
  AllowCompound = false
  Group = -> [Sketch025,Binder001,Pad011,Sketch026,Hole,Sketch034,Sketch035,SubtractivePipe002,Sketch067,Pocket034,Fillet005]
  Origin = -> Origin141
  Tip = -> Fillet005
FEATURE [App::Point] Origin162
  Role = Origin
FEATURE [Sketcher::SketchObject] Sketch068
  ArcFitTolerance = 1e-06
  AttachmentSupport = -> [XY_Plane080]
  ExternalTypes = [0]
  FullyConstrained = true
  MakeInternals = false
  MapMode = 5
  expr: Constraints[11] = 0.95 * VarSet.Base_pogopin_outside
  expr: Constraints[12] = VarSet.Base_pogopins_r * 2.9
  sketch-geometry (15):
    g0: Circle CenterX=-5.5 CenterY=0 CenterZ=0 NormalX=0 NormalY=0 NormalZ=1 AngleXU=0 Radius=1.45
    g1: Circle CenterX=5.5 CenterY=0 CenterZ=0 NormalX=0 NormalY=0 NormalZ=1 AngleXU=0 Radius=1.45
    g2: LineSegment StartX=-9.975 StartY=1.245 StartZ=0 EndX=-9.975 EndY=-1.245 EndZ=0
    g3: LineSegment StartX=-8.175 StartY=-3.045 StartZ=0 EndX=8.175 EndY=-3.045 EndZ=0
    g4: LineSegment StartX=9.975 StartY=-1.245 StartZ=0 EndX=9.975 EndY=1.245 EndZ=0
    g5: LineSegment StartX=8.175 StartY=3.045 StartZ=0 EndX=-8.175 EndY=3.045 EndZ=0
    g6: GeomPoint [constr] X=0 Y=0 Z=0
    g7: ArcOfCircle CenterX=-8.175 CenterY=1.245 CenterZ=0 NormalX=0 NormalY=0 NormalZ=1 AngleXU=0 Radius=1.8 StartAngle=1.5708 EndAngle=3.14159
    g8: GeomPoint [constr] X=-9.975 Y=3.045 Z=0
    g9: ArcOfCircle CenterX=-8.175 CenterY=-1.245 CenterZ=0 NormalX=0 NormalY=0 NormalZ=1 AngleXU=0 Radius=1.8 StartAngle=3.14159 EndAngle=4.71239
    g10: GeomPoint [constr] X=-9.975 Y=-3.045 Z=0
    g11: ArcOfCircle CenterX=8.175 CenterY=-1.245 CenterZ=0 NormalX=0 NormalY=0 NormalZ=1 AngleXU=0 Radius=1.8 StartAngle=4.71239 EndAngle=6.28319
    g12: GeomPoint [constr] X=9.975 Y=-3.045 Z=0
    g13: ArcOfCircle CenterX=8.175 CenterY=1.245 CenterZ=0 NormalX=0 NormalY=0 NormalZ=1 AngleXU=0 Radius=1.8 StartAngle=0 EndAngle=1.5708
    g14: GeomPoint [constr] X=9.975 Y=3.045 Z=0
  constraints (33):
    c: PointOnObject(g0,g-1)
    c: Symmetric(g0,g1,g-2)
    c: Diameter(g0) = 2.9
    c: Equal(g0,g1)
    c: DistanceX(g0,g1) = 11
    c: Vertical(g2)
    c: Vertical(g4)
    c: Horizontal(g3)
    c: Horizontal(g5)
    c: Symmetric(g12,g8,g6)
    c: Coincident(g6,g-1)
    c: DistanceX(g8,g14) = 19.95
    c: DistanceY(g10,g8) = 6.09
    c: PointOnObject(g8,g2)
    c: PointOnObject(g8,g5)
    c: Tangent(g2,g7) = -1.5708
    c: Tangent(g5,g7) = -1.5708
    c: PointOnObject(g10,g2)
    c: PointOnObject(g10,g3)
    c: Tangent(g2,g9) = -1.5708
    c: Tangent(g3,g9) = -1.5708
    c: PointOnObject(g12,g3)
    c: PointOnObject(g12,g4)
    c: Tangent(g3,g11) = -1.5708
    c: Tangent(g4,g11) = -1.5708
    c: PointOnObject(g14,g5)
    c: PointOnObject(g14,g4)
    c: Tangent(g5,g13) = -1.5708
    c: Tangent(g4,g13) = -1.5708
    c: Equal(g9,g11)
    c: Equal(g11,g13)
    c: Equal(g13,g7)
    c: Radius(g7) = 1.8
FEATURE [PartDesign::Pad] Pad024
  Direction = (0,0,1)
  Length = 15
  Length2 = 10
  Profile = -> Sketch068 [Edge3,Edge4,Edge5,Edge6,Edge7,Edge8,Edge9,Edge10]
  ReferenceAxis = -> Sketch068 [N_Axis]
  Refine = true
  Suppressed = false
  Type = 0
FEATURE [PartDesign::Pad] Pad025
  BaseFeature = -> Pad024
  Direction = (0,0,1)
  Length = 8
  Length2 = 10
  Profile = -> Sketch068 [Edge1,Edge2]
  ReferenceAxis = -> Sketch068 [N_Axis]
  Refine = true
  Reversed = true
  Suppressed = false
  Type = 0
FEATURE [PartDesign::Body] Body014  label="instalation_tool_pogopins"
  AllowCompound = false
  Group = -> [Sketch068,Pad024,Pad025]
  Origin = -> Origin161
  Tip = -> Pad025
FEATURE [Sketcher::SketchObject] Sketch069  label="profile"
  ArcFitTolerance = 1e-06
  AttachmentSupport = -> [YZ_Plane055]
  ExternalGeometry = -> [Sketch027]
  ExternalTypes = [0]
  FullyConstrained = true
  MakeInternals = false
  MapMode = 5
  Placement = pos=(0,0,0) rot=(0.57735,0.57735,0.57735;2.0944rad)
  expr: Constraints[10] = VarSet.Base_gasket_width
  expr: Constraints[11] = VarSet.Base_gasket_height
  sketch-geometry (5):
    g0: LineSegment StartX=1 StartY=1 StartZ=0 EndX=1 EndY=-1 EndZ=0
    g1: LineSegment StartX=1 StartY=-1 StartZ=0 EndX=2 EndY=-1 EndZ=0
    g2: LineSegment StartX=2 StartY=-1 StartZ=0 EndX=2 EndY=1 EndZ=0
    g3: LineSegment StartX=2 StartY=1 StartZ=0 EndX=1 EndY=1 EndZ=0
    g4: GeomPoint [constr] X=1.5 Y=0 Z=0
  constraints (12):
    c: Coincident(g0,g1)
    c: Coincident(g1,g2)
    c: Coincident(g2,g3)
    c: Coincident(g3,g0)
    c: Vertical(g0)
    c: Vertical(g2)
    c: Horizontal(g1)
    c: Horizontal(g3)
    c: Symmetric(g2,g0,g4)
    c: Coincident(g4,g-3)
    c: Distance(g3,g3) = 1
    c: DistanceY(g0,g0) = 2
FEATURE [PartDesign::AdditivePipe] AdditivePipe
  AuxilleryCurvelinear = true
  AuxillerySpineTangent = false
  Binormal = (0,0,0)
  Mode = 0
  Placement = pos=(0,0,0) rot=(1,1,1;2.0944rad)
  Profile = -> Sketch069
  Refine = true
  Spine = -> Sketch027 [Edge1,Edge16,Edge15,Edge14,Edge13,Edge12,Edge11,Edge10,Edge9,Edge8,Edge7,Edge6,Edge5,Edge4,Edge3,Edge2]
  SpineTangent = false
  Suppressed = false
  Transformation = 0
  Transition = 0
FEATURE [PartDesign::Body] Body001  label="gasket_main_body001"
  AllowCompound = false
  Group = -> [Binder,Sketch027,Sketch069,AdditivePipe]
  Origin = -> Origin110
  Tip = -> AdditivePipe
FEATURE [Sketcher::SketchObject] Sketch070  label="profile002"
  ArcFitTolerance = 1e-06
  AttachmentSupport = -> [YZ_Plane073]
  ExternalGeometry = -> [Sketch040]
  ExternalTypes = [0]
  FullyConstrained = true
  MakeInternals = false
  MapMode = 5
  Placement = pos=(0,0,0) rot=(0.57735,0.57735,0.57735;2.0944rad)
  expr: Constraints[10] = VarSet.Base_gasket_width
  expr: Constraints[11] = VarSet.Base_gasket_height
  sketch-geometry (5):
    g0: LineSegment StartX=1 StartY=1 StartZ=0 EndX=1 EndY=-1 EndZ=0
    g1: LineSegment StartX=1 StartY=-1 StartZ=0 EndX=2 EndY=-1 EndZ=0
    g2: LineSegment StartX=2 StartY=-1 StartZ=0 EndX=2 EndY=1 EndZ=0
    g3: LineSegment StartX=2 StartY=1 StartZ=0 EndX=1 EndY=1 EndZ=0
    g4: GeomPoint [constr] X=1.5 Y=-1e-16 Z=0
  constraints (12):
    c: Coincident(g0,g1)
    c: Coincident(g1,g2)
    c: Coincident(g2,g3)
    c: Coincident(g3,g0)
    c: Vertical(g0)
    c: Vertical(g2)
    c: Horizontal(g1)
    c: Horizontal(g3)
    c: Symmetric(g2,g0,g4)
    c: Coincident(g4,g-3)
    c: Distance(g3,g3) = 1
    c: Distance(g0,g0) = 2
FEATURE [PartDesign::AdditivePipe] AdditivePipe001
  AuxilleryCurvelinear = true
  AuxillerySpineTangent = false
  Binormal = (0,0,0)
  Mode = 0
  Placement = pos=(0,0,0) rot=(1,1,1;2.0944rad)
  Profile = -> Sketch070
  Refine = true
  Spine = -> Sketch040 [Edge1,Edge16,Edge15,Edge14,Edge13,Edge12,Edge11,Edge10,Edge9,Edge8,Edge7,Edge6,Edge5,Edge4,Edge3,Edge2]
  SpineTangent = false
  Suppressed = false
  Transformation = 0
  Transition = 0
FEATURE [PartDesign::Body] Body010  label="battery_cover_gasket001"
  AllowCompound = false
  Group = -> [Binder004,Sketch040,Sketch070,AdditivePipe001]
  Origin = -> Origin147
  Tip = -> AdditivePipe001
FEATURE [App::Part] Part005  label="battery_cover_gasket"
  Group = -> [Body010]
  Origin = -> Origin139
FEATURE [PartDesign::Fillet] Fillet006
  Base = -> PolarPattern [Edge476,Edge177,Edge172,Edge478]
  BaseFeature = -> PolarPattern
  Radius = 5
  Refine = true
  SupportTransform = false
  Suppressed = false
  UseAllEdges = false
FEATURE [PartDesign::Body] Body  label="main_body001"
  AllowCompound = false
  Group = -> [Sketch,Pad,Pocket,Pocket001,Sketch003,Pad002,Pocket002,Sketch004,Sketch005,Pocket007,Pocket008,Pocket010,Pad007,Sketch019,Sketch020,Pocket018,Sketch024,Pocket025,Sketch032,SubtractivePipe,Pocket028,Pad020,Sketch046,Pad021,Sketch047,Pocket029,Sketch063,Pad022,Sketch064,Pocket031,Sketch065,Pad023,Sketch066,Pocket032,PolarPattern,Fillet006]
  Origin = -> Origin106
  Tip = -> Fillet006
FEATURE [App::Part] Part  label="main_body"
  Group = -> [Body,Body006]
  Origin = -> Origin104
  Placement = pos=(0,0,43) rot=(0,0,1;0rad)
FEATURE [App::FeaturePython] Joint025  label="battery_gasket"  # Assembly joint (typed FeaturePython)
  Activated = true
  AngleMax = 0
  AngleMin = 0
  Detach1 = false
  Detach2 = false
  Distance = 0
  Distance2 = 0
  EnableAngleMax = false
  EnableAngleMin = false
  EnableLengthMax = false
  EnableLengthMin = false
  JointType = 0 (Fixed)
  LengthMax = 0
  LengthMin = 0
  Placement1 = pos=(8.9e-15,1,-1) rot=(-0.707107,0,0.707107;3.14159rad)
  Placement2 = pos=(1.24e-14,1,-1) rot=(-0.707107,0,0.707107;3.14159rad)
  Reference1 = -> Assembly [battery.Body002.Edge112,battery.Body002.Edge112]
  Reference2 = -> Assembly [battery_cover_gasket.Body010.Edge3,battery_cover_gasket.Body010.Edge3]
FEATURE [App::Point] Origin164
  Role = Origin
FEATURE [App::Point] Origin166
  Role = Origin
FEATURE [PartDesign::SubShapeBinder] Binder005
  BindCopyOnChange = 0
  BindMode = 0
  ClaimChildren = false
  Context = -> Part009 [Body015.Binder005.]
  Fuse = false
  MakeFace = true
  OffsetFill = false
  OffsetIntersection = false
  OffsetJoinType = 0
  OffsetOpenResult = false
  PartialLoad = false
  Refine = true
  Relative = true
  Support = -> [Part002[Body002.Sketch007.]]
  _Version = 2
FEATURE [Sketcher::SketchObject] Sketch071  label="battery_holder"
  ArcFitTolerance = 1e-06
  AttachmentSupport = -> [XZ_Plane082]
  ExternalGeometry = -> [Binder005]
  ExternalTypes = [0,0,0,0,0,0,0,0,0,0,0]
  FullyConstrained = true
  MakeInternals = false
  MapMode = 5
  Placement = pos=(0,0,0) rot=(1,0,0;1.5708rad)
  sketch-geometry (3):
    g0: LineSegment StartX=-29.4 StartY=-12 StartZ=0 EndX=-29.4 EndY=-24.5 EndZ=0
    g1: LineSegment StartX=-29.4 StartY=-24.5 StartZ=0 EndX=29.5 EndY=-24.5 EndZ=0
    g2: LineSegment StartX=29.5 StartY=-24.5 StartZ=0 EndX=29.5 EndY=-12 EndZ=0
  constraints (8):
    c: Coincident(g-4,g0)
    c: Vertical(g0)
    c: Coincident(g0,g1)
    c: Horizontal(g1)
    c: Coincident(g1,g2)
    c: Coincident(g2,g-10)
    c: Parallel(g2,g-2)
    c: Distance(g-5,g1) = 3
FEATURE [App::Link] battery_top  label="battery_top001"
  LinkPlacement = pos=(0.216708,-60,-23.8449) rot=(0,1,0;3.14159rad)
  LinkedObject = -> Part009
  Placement = pos=(0.216708,-60,-23.8449) rot=(0,1,0;3.14159rad)
FEATURE [PartDesign::Pad] Pad026  label="battery_holder001"
  Direction = (0,-1,2e-16)
  Length = 5
  Length2 = 10
  Placement = pos=(0,0,0) rot=(1,0,0;1.5708rad)
  Profile = -> Sketch071 [Edge2,Edge3,Vertex4,Edge4,Edge5,Edge6,Edge7,Edge8,Edge9,Edge10,Edge1]
  ReferenceAxis = -> Sketch071 [N_Axis]
  Refine = true
  Suppressed = false
  Type = 0
FEATURE [Sketcher::SketchObject] Sketch072
  ArcFitTolerance = 1e-06
  AttachmentSupport = -> [XZ_Plane082]
  ExternalGeometry = -> [Sketch071]
  ExternalTypes = [0]
  FullyConstrained = true
  MakeInternals = false
  MapMode = 5
  Placement = pos=(0,0,0) rot=(1,0,0;1.5708rad)
  sketch-geometry (3):
    g0: LineSegment StartX=-29.4 StartY=-24.5 StartZ=0 EndX=-29.4 EndY=-22.5 EndZ=0
    g1: LineSegment StartX=-29.4 StartY=-22.5 StartZ=0 EndX=29.5 EndY=-22.5 EndZ=0
    g2: LineSegment StartX=29.5 StartY=-22.5 StartZ=0 EndX=29.5 EndY=-24.5 EndZ=0
  constraints (8):
    c: Coincident(g0,g-3)
    c: Coincident(g0,g1)
    c: Horizontal(g1)
    c: Coincident(g1,g2)
    c: Coincident(g2,g-3)
    c: Parallel(g2,g-2)
    c: Parallel(g0,g-2)
    c: Distance(g0,g0) = 2
FEATURE [PartDesign::Pad] Pad027
  BaseFeature = -> Pad026
  Direction = (0,-1,2e-16)
  Length = 20
  Length2 = 10
  Placement = pos=(0,0,0) rot=(1,0,0;1.5708rad)
  Profile = -> Sketch072
  ReferenceAxis = -> Sketch072 [N_Axis]
  Refine = true
  Suppressed = false
  Type = 0
FEATURE [PartDesign::Mirrored] Mirrored
  BaseFeature = -> Pad027
  MirrorPlane = -> Pad027 [Face1]
  Originals = -> [Pad027]
  Placement = pos=(0,0,0) rot=(1,0,0;1.5708rad)
  Refine = true
  Suppressed = false
  TransformMode = 1
FEATURE [PartDesign::Body] Body015  label="Body"
  AllowCompound = false
  Group = -> [Binder005,Sketch071,Pad026,Sketch072,Pad027,Mirrored]
  Origin = -> Origin165
  Tip = -> Mirrored
FEATURE [App::Part] Part009  label="battery_top"
  Group = -> [Body015]
  Origin = -> Origin163
FEATURE [App::FeaturePython] Joint026  label="battery_top002"  # Assembly joint (typed FeaturePython)
  Activated = true
  AngleMax = 0
  AngleMin = 0
  Detach1 = false
  Detach2 = false
  Distance = 0
  Distance2 = 0
  EnableAngleMax = false
  EnableAngleMin = false
  EnableLengthMax = false
  EnableLengthMin = false
  JointType = 0 (Fixed)
  LengthMax = 0
  LengthMin = 0
  Offset2 = pos=(0,0,-24) rot=(0,0,1;0rad)
  Placement1 = pos=(0,34.4664,0) rot=(0.57735,0.57735,0.57735;4.18879rad)
  Placement2 = pos=(0.1,-13.5,-12) rot=(1,0,0;1.5708rad)
  Reference1 = -> Assembly [_8650_v1.Face34,_8650_v1.Face34]
  Reference2 = -> Assembly [battery_top.Body015.Face16,battery_top.Body015.Face16]
FEATURE [App::Point] Origin168
  Role = Origin
FEATURE [App::Point] Origin170
  Role = Origin
FEATURE [Sketcher::SketchObject] Sketch073
  ArcFitTolerance = 1e-06
  AttachmentSupport = -> [XY_Plane084]
  ExternalTypes = [0]
  FullyConstrained = true
  MakeInternals = false
  MapMode = 5
  sketch-geometry (1):
    g0: Circle CenterX=0 CenterY=0 CenterZ=0 NormalX=0 NormalY=0 NormalZ=1 AngleXU=0 Radius=9.5
  constraints (2):
    c: Coincident(g0,g-1)
    c: Diameter(g0) = 19
FEATURE [PartDesign::Pad] Pad028
  Direction = (0,0,1)
  Length = 1
  Length2 = 10
  Profile = -> Sketch073
  ReferenceAxis = -> Sketch073 [N_Axis]
  Refine = true
  Suppressed = false
  Type = 0
FEATURE [PartDesign::Body] Body016  label="usb_screw_gasket001"
  AllowCompound = false
  Group = -> [Sketch073,Pad028]
  Origin = -> Origin169
  Tip = -> Pad028
FEATURE [App::Part] Part010  label="usb_screw_gasket"
  Group = -> [Body016]
  Origin = -> Origin167
FEATURE [App::Link] usb_screw_gasket  label="usb_screw_gasket002"
  LinkPlacement = pos=(-38.75,26,-13) rot=(0.57735,0.57735,-0.57735;4.18879rad)
  LinkedObject = -> Part010
  Placement = pos=(-38.75,26,-13) rot=(0.57735,0.57735,-0.57735;4.18879rad)
FEATURE [App::FeaturePython] Joint027  label="usb_screw_to_gasket"  # Assembly joint (typed FeaturePython)
  Activated = true
  AngleMax = 0
  AngleMin = 0
  Detach1 = false
  Detach2 = false
  Distance = 0
  Distance2 = 0
  EnableAngleMax = false
  EnableAngleMin = false
  EnableLengthMax = false
  EnableLengthMin = false
  JointType = 0 (Fixed)
  LengthMax = 0
  LengthMin = 0
  Placement1 = pos=(-0.58879,7.41078e-07,9) rot=(0,1,0;3.14159rad)
  Placement2 = pos=(-1.8e-15,-3e-16,1) rot=(0,0,1;0rad)
  Reference1 = -> Assembly [usb_screw.Body004.Face34,usb_screw.Body004.Face34]
  Reference2 = -> Assembly [usb_screw_gasket.Body016.Face3,usb_screw_gasket.Body016.Face3]
FEATURE [App::FeaturePython] Joint028  label="usb_gasket_to_body"  # Assembly joint (typed FeaturePython)
  Activated = true
  AngleMax = 0
  AngleMin = 0
  Detach1 = false
  Detach2 = false
  Distance = 0
  Distance2 = 0
  EnableAngleMax = false
  EnableAngleMin = false
  EnableLengthMax = false
  EnableLengthMin = false
  JointType = 0 (Fixed)
  LengthMax = 0
  LengthMin = 0
  Offset2 = pos=(0,0,-4) rot=(0,0,1;0rad)
  Placement1 = pos=(0,1.7e-15,3.75) rot=(0,0,1;3.14159rad)
  Placement2 = pos=(-1.8e-15,-3e-16,-4) rot=(0,0,1;0rad)
  Reference1 = -> Assembly [usb_cover_base.Body003.Face4,usb_cover_base.Body003.Face4]
  Reference2 = -> Assembly [usb_screw_gasket.Body016.Face2,usb_screw_gasket.Body016.Face2]
FEATURE [App::FeaturePython] Joint029  label="pogoping_main"  # Assembly joint (typed FeaturePython)
  Activated = true
  AngleMax = 0
  AngleMin = 0
  Detach1 = false
  Detach2 = false
  Distance = 0
  Distance2 = 0
  EnableAngleMax = false
  EnableAngleMin = false
  EnableLengthMax = false
  EnableLengthMin = false
  JointType = 0 (Fixed)
  LengthMax = 0
  LengthMin = 0
  Offset2 = pos=(0,0,0) rot=(0,0,-1;1.5708rad)
  Placement1 = pos=(5.5,1.8,-2e-15) rot=(0.57735,-0.57735,0.57735;2.0944rad)
  Placement2 = pos=(5.45,-10.5,-12.5) rot=(-0.57735,-0.57735,0.57735;4.18879rad)
  Reference1 = -> Assembly [Magnetic_Pogo_Connector_3_Pin__Type_2_006.Part__Feature084.Edge27,Magnetic_Pogo_Connector_3_Pin__Type_2_006.Part__Feature084.Edge27]
  Reference2 = -> Assembly [base.Body006.Edge121,base.Body006.Edge121]
FEATURE [App::FeaturePython] Joint030  label="oring003"  # Assembly joint (typed FeaturePython)
  Activated = true
  AngleMax = 0
  AngleMin = 0
  Detach1 = false
  Detach2 = false
  Distance = 0
  Distance2 = 0
  EnableAngleMax = false
  EnableAngleMin = false
  EnableLengthMax = false
  EnableLengthMin = false
  JointType = 0 (Fixed)
  LengthMax = 0
  LengthMin = 0
  Placement1 = pos=(9.5,0,0) rot=(0,0,1;0rad)
  Placement2 = pos=(9.5,-12.2,-12.5) rot=(-1,0,0;3.14159rad)
  Reference1 = -> Assembly [oring.Body013.Edge2,oring.Body013.Edge2]
  Reference2 = -> Assembly [base.Body006.Edge124,base.Body006.Edge124]
FEATURE [App::FeaturePython] Joint031  label="main_body_cover"  # Assembly joint (typed FeaturePython)
  Activated = true
  AngleMax = 0
  AngleMin = 0
  Detach1 = false
  Detach2 = false
  Distance = 0
  Distance2 = 0
  EnableAngleMax = false
  EnableAngleMin = false
  EnableLengthMax = false
  EnableLengthMin = false
  JointType = 0 (Fixed)
  LengthMax = 0
  LengthMin = 0
  Placement1 = pos=(3.7e-15,54,1) rot=(0.707107,0,0.707107;3.14159rad)
  Placement2 = pos=(-1.4e-15,54,1) rot=(0.707107,0,0.707107;3.14159rad)
  Reference1 = -> Assembly [mainbody_cover001.Edge88,mainbody_cover001.Edge88]
  Reference2 = -> Assembly [gasket_main_body001.Edge26,gasket_main_body001.Edge26]
FEATURE [App::FeaturePython] Move  # WARN: FeaturePython — macro-defined, semantics opaque (R4)
  MoveType = 0
  MovementTransform = pos=(0.14081,21.995,-0.44545) rot=(0,0,1;0rad)
  References = -> Assembly [usb_c_male.]
FEATURE [App::FeaturePython] Move001  # WARN: FeaturePython — macro-defined, semantics opaque (R4)
  MoveType = 0
  MovementTransform = pos=(-53.0423,0.13452,-10.1238) rot=(0,-0.710187,0.710187;0rad)
  References = -> Assembly [usb_screw.]
FEATURE [App::FeaturePython] Move002  # WARN: FeaturePython — macro-defined, semantics opaque (R4)
  MoveType = 0
  MovementTransform = pos=(-25.5389,0.06477,-4.87441) rot=(0,-1.00068,0;0rad)
  References = -> Assembly [usb_screw_gasket.]
FEATURE [App::FeaturePython] Move003  # WARN: FeaturePython — macro-defined, semantics opaque (R4)
  MoveType = 0
  MovementTransform = pos=(-40.4751,4.55506,212.125) rot=(0,0,-1.00436;0rad)
  References = -> Assembly [mainbody_cover001.]
FEATURE [App::FeaturePython] Move004  # WARN: FeaturePython — macro-defined, semantics opaque (R4)
  MoveType = 0
  MovementTransform = pos=(51.0779,-0.12956,9.74884) rot=(0,0,1;0rad)
  References = -> Assembly [mainbody_cover001.]
FEATURE [App::FeaturePython] Move005  # WARN: FeaturePython — macro-defined, semantics opaque (R4)
  MoveType = 0
  MovementTransform = pos=(-11.9926,1.34965,62.8519) rot=(0,0,-1.00436;0rad)
  References = -> Assembly [gasket_main_body001.]
FEATURE [App::FeaturePython] Move006  # WARN: FeaturePython — macro-defined, semantics opaque (R4)
  MoveType = 0
  MovementTransform = pos=(26.5212,-0.06727,5.06188) rot=(0,0,1;0rad)
  References = -> Assembly [gasket_main_body001.]
FEATURE [App::FeaturePython] Move007  # WARN: FeaturePython — macro-defined, semantics opaque (R4)
  MoveType = 0
  MovementTransform = pos=(29.4194,-3.31086,-154.183) rot=(0,0,1;0rad)
  References = -> Assembly [mainbody_cover001.]
FEATURE [App::FeaturePython] Move008  # WARN: FeaturePython — macro-defined, semantics opaque (R4)
  MoveType = 0
  MovementTransform = pos=(7.12062,-0.80134,-37.3183) rot=(0,0,1.00436;0rad)
  References = -> Assembly [gasket_main_body001.]
FEATURE [App::FeaturePython] Move009  # WARN: FeaturePython — macro-defined, semantics opaque (R4)
  MoveType = 0
  MovementTransform = pos=(-0.0384,-5.99865,0.12148) rot=(0,0,1;0rad)
  References = -> Assembly [oring.]
FEATURE [App::FeaturePython] Move011  # WARN: FeaturePython — macro-defined, semantics opaque (R4)
  MoveType = 0
  MovementTransform = pos=(-17.9889,2.02446,94.2779) rot=(0,0,1;0rad)
  References = -> Assembly [battery_cover.]
FEATURE [App::FeaturePython] Move012  # WARN: FeaturePython — macro-defined, semantics opaque (R4)
  MoveType = 0
  MovementTransform = pos=(-74.6523,0.18927,-14.2483) rot=(0,0,1;0rad)
  References = -> Assembly [battery_cover.]
FEATURE [App::FeaturePython] Move013  # WARN: FeaturePython — macro-defined, semantics opaque (R4)
  MoveType = 0
  MovementTransform = pos=(0.32002,49.9888,-1.01237) rot=(0,0,1;0rad)
  References = -> Assembly [battery_top.]
FEATURE [App::FeaturePython] Move014  # WARN: FeaturePython — macro-defined, semantics opaque (R4)
  MoveType = 0
  MovementTransform = pos=(83.4927,-0.2117,15.9356) rot=(0,0,1;0rad)
  References = -> Assembly [battery_top.]
FEATURE [App::FeaturePython] Move015  # WARN: FeaturePython — macro-defined, semantics opaque (R4)
  MoveType = 0
  MovementTransform = pos=(13.8665,-1.56054,-72.6725) rot=(0,0,1;0rad)
  References = -> Assembly [battery_top.]
FEATURE [App::FeaturePython] Move016  # WARN: FeaturePython — macro-defined, semantics opaque (R4)
  MoveType = 0
  MovementTransform = pos=(-5.24677,0.59048,27.4977) rot=(0,0,1;0rad)
  References = -> Assembly [battery_cover_gasket.]
FEATURE [App::FeaturePython] Move017  # WARN: FeaturePython — macro-defined, semantics opaque (R4)
  MoveType = 0
  MovementTransform = pos=(-35.3616,0.08971,-6.74919) rot=(0,0,1;0rad)
  References = -> Assembly [battery_cover_gasket.]
FEATURE [App::FeaturePython] Move018  # WARN: FeaturePython — macro-defined, semantics opaque (R4)
  MoveType = 0
  MovementTransform = pos=(-14.9907,1.68708,78.5648) rot=(0,0,1;0rad)
  References = -> Assembly [battery_top.]
FEATURE [App::FeaturePython] Move019  # WARN: FeaturePython — macro-defined, semantics opaque (R4)
  MoveType = 0
  MovementTransform = pos=(-0.30082,-46.9896,0.95164) rot=(0,1.00436,0;0rad)
  References = -> Assembly [battery_top.]
FEATURE [App::FeaturePython] Exploded_View  # WARN: FeaturePython — macro-defined, semantics opaque (R4)
  Group = -> [Move,Move001,Move002,Move003,Move004,Move005,Move006,Move007,Move008,Move009,Move011,Move012,Move013,Move014,Move015,Move016,Move017,Move018,Move019]
FEATURE [Assembly::ViewGroup] Exploded_Views
  Group = -> [Exploded_View]
FEATURE [App::FeaturePython] Joint032  label="gasket_main001"  # Assembly joint (typed FeaturePython)
  Activated = true
  AngleMax = 0
  AngleMin = 0
  Detach1 = false
  Detach2 = false
  Distance = 0
  Distance2 = 0
  EnableAngleMax = false
  EnableAngleMin = false
  EnableLengthMax = false
  EnableLengthMin = false
  JointType = 0 (Fixed)
  LengthMax = 0
  LengthMin = 0
  Placement1 = pos=(-1.4e-15,54,-1) rot=(0.707107,0,0.707107;3.14159rad)
  Placement2 = pos=(1.8e-15,54,-1) rot=(0.707107,0,0.707107;3.14159rad)
  Reference1 = -> Assembly [gasket_main_body001.Edge27,gasket_main_body001.Edge27]
  Reference2 = -> Assembly [base.Body.Edge131,base.Body.Edge131]
FEATURE [Assembly::JointGroup] Joints
  Group = -> [GroundedJoint,Joint,Joint003,Joint004,Joint005,Joint006,Joint007,Joint008,Joint009,Joint010,Joint011,Joint016,Joint017,Joint018,Joint020,Joint025,Joint026,Joint027,Joint028,Joint029,Joint030,Joint031,Joint032]
FEATURE [Assembly::AssemblyObject] Assembly
  Group = -> [Joints,Group001,base,GroundedJoint,battery,usb_cover_base,usb_screw,Magnetic_Pogo_Connector_3_Pin__Type_1_006,Magnetic_Pogo_Connector_3_Pin__Type_2_006,_8650_v002,RAK4631__Solid_,_8650_v1,_053072_1,RAK19003__Solid_,antenna_WiFi_RP_SMA_conn_v003,on_off_switch,switch_cover,Joint,Joint003,Joint004,Joint005,Joint006,Joint007,Joint008,Joint009,Joint010,Joint011,gasket_main_body001,battery_cover,+40 more]
  Origin = -> Origin112
  Type = Assembly
